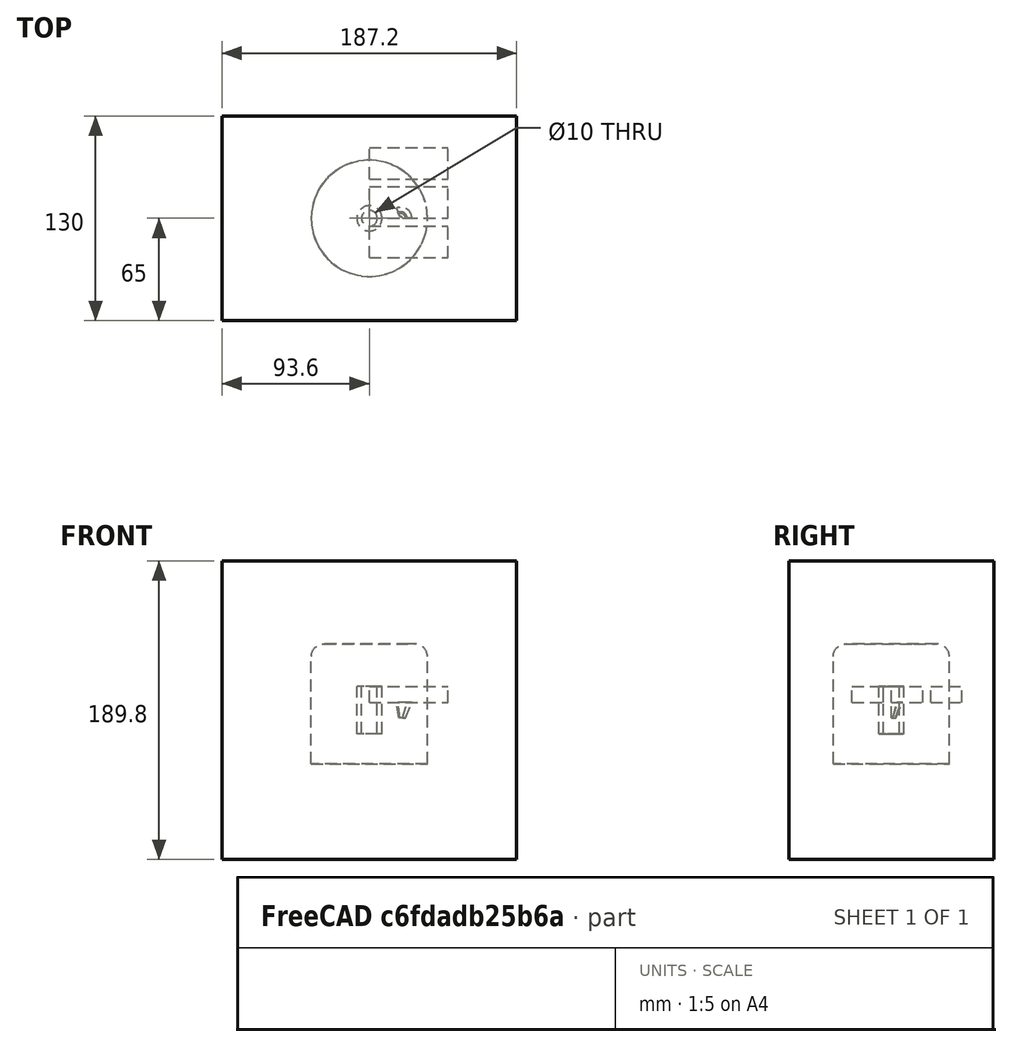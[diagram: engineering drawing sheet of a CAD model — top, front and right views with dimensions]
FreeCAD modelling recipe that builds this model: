
FCSTD DOCUMENT  (FreeCAD 1.0R39109 (Git))
Label: AssemblyTest
License: All rights reserved
LicenseURL: http://en.wikipedia.org/wiki/All_rights_reserved
objects: App::DocumentObjectGroupPython×1251, Part::FeaturePython×6, App::Part×5, Part::Box×3, Part::Fuse×2
note: 11 computed .brp shape members not serialized (recipe doc carries the construction recipe); baked Part::Feature solids carry a one-line shape summary decoded from their .brp

FEATURE [App::DocumentObjectGroupPython] HALFPI  # scripted group (container) (typed FeaturePython)
  name = HALFPI
  value = pi/2.
FEATURE [App::DocumentObjectGroupPython] PI  # scripted group (container) (typed FeaturePython)
  name = PI
  value = 1.*pi
FEATURE [App::DocumentObjectGroupPython] TWOPI  # scripted group (container) (typed FeaturePython)
  name = TWOPI
  value = 2.*pi
FEATURE [App::DocumentObjectGroupPython] Constants  # scripted group (container) (typed FeaturePython)
  Group = -> [HALFPI,PI,TWOPI]
FEATURE [App::DocumentObjectGroupPython] Variables  # scripted group (container) (typed FeaturePython)
FEATURE [App::DocumentObjectGroupPython] Quantities  # scripted group (container) (typed FeaturePython)
FEATURE [App::DocumentObjectGroupPython] Isotopes  # scripted group (container) (typed FeaturePython)
FEATURE [App::DocumentObjectGroupPython] Elements  # scripted group (container) (typed FeaturePython)
FEATURE [App::DocumentObjectGroupPython] Matrix  # scripted group (container) (typed FeaturePython)
FEATURE [App::DocumentObjectGroupPython] Surfaces  # scripted group (container) (typed FeaturePython)
FEATURE [App::DocumentObjectGroupPython] Opticals  # scripted group (container) (typed FeaturePython)
  Group = -> [Matrix,Surfaces]
FEATURE [App::DocumentObjectGroupPython] G4Isotopes  # scripted group (container) (typed FeaturePython)
FEATURE [App::DocumentObjectGroupPython] H_element  # scripted group (container) (typed FeaturePython)
  Z = 1
  atom_value = 1.008
  formula = H
  name = H_element
FEATURE [App::DocumentObjectGroupPython] He_element  # scripted group (container) (typed FeaturePython)
  Z = 2
  atom_value = 4.0026
  formula = He
  name = He_element
FEATURE [App::DocumentObjectGroupPython] Li_element  # scripted group (container) (typed FeaturePython)
  Z = 3
  atom_value = 6.94
  formula = Li
  name = Li_element
FEATURE [App::DocumentObjectGroupPython] Be_element  # scripted group (container) (typed FeaturePython)
  Z = 4
  atom_value = 9.01218
  formula = Be
  name = Be_element
FEATURE [App::DocumentObjectGroupPython] B_element  # scripted group (container) (typed FeaturePython)
  Z = 5
  atom_value = 10.81
  formula = B
  name = B_element
FEATURE [App::DocumentObjectGroupPython] C_element  # scripted group (container) (typed FeaturePython)
  Z = 6
  atom_value = 12.011
  formula = C
  name = C_element
FEATURE [App::DocumentObjectGroupPython] N_element  # scripted group (container) (typed FeaturePython)
  Z = 7
  atom_value = 14.007
  formula = N
  name = N_element
FEATURE [App::DocumentObjectGroupPython] O_element  # scripted group (container) (typed FeaturePython)
  Z = 8
  atom_value = 15.999
  formula = O
  name = O_element
FEATURE [App::DocumentObjectGroupPython] F_element  # scripted group (container) (typed FeaturePython)
  Z = 9
  atom_value = 18.9984
  formula = F
  name = F_element
FEATURE [App::DocumentObjectGroupPython] Ne_element  # scripted group (container) (typed FeaturePython)
  Z = 10
  atom_value = 20.1797
  formula = Ne
  name = Ne_element
FEATURE [App::DocumentObjectGroupPython] Na_element  # scripted group (container) (typed FeaturePython)
  Z = 11
  atom_value = 22.9898
  formula = Na
  name = Na_element
FEATURE [App::DocumentObjectGroupPython] Mg_element  # scripted group (container) (typed FeaturePython)
  Z = 12
  atom_value = 24.305
  formula = Mg
  name = Mg_element
FEATURE [App::DocumentObjectGroupPython] Al_element  # scripted group (container) (typed FeaturePython)
  Z = 13
  atom_value = 26.9815
  formula = Al
  name = Al_element
FEATURE [App::DocumentObjectGroupPython] Si_element  # scripted group (container) (typed FeaturePython)
  Z = 14
  atom_value = 28.085
  formula = Si
  name = Si_element
FEATURE [App::DocumentObjectGroupPython] P_element  # scripted group (container) (typed FeaturePython)
  Z = 15
  atom_value = 30.9738
  formula = P
  name = P_element
FEATURE [App::DocumentObjectGroupPython] S_element  # scripted group (container) (typed FeaturePython)
  Z = 16
  atom_value = 32.06
  formula = S
  name = S_element
FEATURE [App::DocumentObjectGroupPython] Cl_element  # scripted group (container) (typed FeaturePython)
  Z = 17
  atom_value = 35.45
  formula = Cl
  name = Cl_element
FEATURE [App::DocumentObjectGroupPython] Ar_element  # scripted group (container) (typed FeaturePython)
  Z = 18
  atom_value = 39.95
  formula = Ar
  name = Ar_element
FEATURE [App::DocumentObjectGroupPython] K_element  # scripted group (container) (typed FeaturePython)
  Z = 19
  atom_value = 39.0983
  formula = K
  name = K_element
FEATURE [App::DocumentObjectGroupPython] Ca_element  # scripted group (container) (typed FeaturePython)
  Z = 20
  atom_value = 40.078
  formula = Ca
  name = Ca_element
FEATURE [App::DocumentObjectGroupPython] Sc_element  # scripted group (container) (typed FeaturePython)
  Z = 21
  atom_value = 44.9559
  formula = Sc
  name = Sc_element
FEATURE [App::DocumentObjectGroupPython] Ti_element  # scripted group (container) (typed FeaturePython)
  Z = 22
  atom_value = 47.867
  formula = Ti
  name = Ti_element
FEATURE [App::DocumentObjectGroupPython] V_element  # scripted group (container) (typed FeaturePython)
  Z = 23
  atom_value = 50.9415
  formula = V
  name = V_element
FEATURE [App::DocumentObjectGroupPython] Cr_element  # scripted group (container) (typed FeaturePython)
  Z = 24
  atom_value = 51.9961
  formula = Cr
  name = Cr_element
FEATURE [App::DocumentObjectGroupPython] Mn_element  # scripted group (container) (typed FeaturePython)
  Z = 25
  atom_value = 54.938
  formula = Mn
  name = Mn_element
FEATURE [App::DocumentObjectGroupPython] Fe_element  # scripted group (container) (typed FeaturePython)
  Z = 26
  atom_value = 55.845
  formula = Fe
  name = Fe_element
FEATURE [App::DocumentObjectGroupPython] Co_element  # scripted group (container) (typed FeaturePython)
  Z = 27
  atom_value = 58.9332
  formula = Co
  name = Co_element
FEATURE [App::DocumentObjectGroupPython] Ni_element  # scripted group (container) (typed FeaturePython)
  Z = 28
  atom_value = 58.6934
  formula = Ni
  name = Ni_element
FEATURE [App::DocumentObjectGroupPython] Cu_element  # scripted group (container) (typed FeaturePython)
  Z = 29
  atom_value = 63.546
  formula = Cu
  name = Cu_element
FEATURE [App::DocumentObjectGroupPython] Zn_element  # scripted group (container) (typed FeaturePython)
  Z = 30
  atom_value = 65.38
  formula = Zn
  name = Zn_element
FEATURE [App::DocumentObjectGroupPython] Ga_element  # scripted group (container) (typed FeaturePython)
  Z = 31
  atom_value = 69.723
  formula = Ga
  name = Ga_element
FEATURE [App::DocumentObjectGroupPython] Ge_element  # scripted group (container) (typed FeaturePython)
  Z = 32
  atom_value = 72.63
  formula = Ge
  name = Ge_element
FEATURE [App::DocumentObjectGroupPython] As_element  # scripted group (container) (typed FeaturePython)
  Z = 33
  atom_value = 74.9216
  formula = As
  name = As_element
FEATURE [App::DocumentObjectGroupPython] Se_element  # scripted group (container) (typed FeaturePython)
  Z = 34
  atom_value = 78.971
  formula = Se
  name = Se_element
FEATURE [App::DocumentObjectGroupPython] Br_element  # scripted group (container) (typed FeaturePython)
  Z = 35
  atom_value = 79.904
  formula = Br
  name = Br_element
FEATURE [App::DocumentObjectGroupPython] Kr_element  # scripted group (container) (typed FeaturePython)
  Z = 36
  atom_value = 83.798
  formula = Kr
  name = Kr_element
FEATURE [App::DocumentObjectGroupPython] Rb_element  # scripted group (container) (typed FeaturePython)
  Z = 37
  atom_value = 85.4678
  formula = Rb
  name = Rb_element
FEATURE [App::DocumentObjectGroupPython] Sr_element  # scripted group (container) (typed FeaturePython)
  Z = 38
  atom_value = 87.62
  formula = Sr
  name = Sr_element
FEATURE [App::DocumentObjectGroupPython] Y_element  # scripted group (container) (typed FeaturePython)
  Z = 39
  atom_value = 88.9058
  formula = Y
  name = Y_element
FEATURE [App::DocumentObjectGroupPython] Zr_element  # scripted group (container) (typed FeaturePython)
  Z = 40
  atom_value = 91.224
  formula = Zr
  name = Zr_element
FEATURE [App::DocumentObjectGroupPython] Nb_element  # scripted group (container) (typed FeaturePython)
  Z = 41
  atom_value = 92.9064
  formula = Nb
  name = Nb_element
FEATURE [App::DocumentObjectGroupPython] Mo_element  # scripted group (container) (typed FeaturePython)
  Z = 42
  atom_value = 95.95
  formula = Mo
  name = Mo_element
FEATURE [App::DocumentObjectGroupPython] Tc_element  # scripted group (container) (typed FeaturePython)
  Z = 43
  atom_value = 97
  formula = Tc
  name = Tc_element
FEATURE [App::DocumentObjectGroupPython] Ru_element  # scripted group (container) (typed FeaturePython)
  Z = 44
  atom_value = 101.07
  formula = Ru
  name = Ru_element
FEATURE [App::DocumentObjectGroupPython] Rh_element  # scripted group (container) (typed FeaturePython)
  Z = 45
  atom_value = 102.905
  formula = Rh
  name = Rh_element
FEATURE [App::DocumentObjectGroupPython] Pd_element  # scripted group (container) (typed FeaturePython)
  Z = 46
  atom_value = 106.42
  formula = Pd
  name = Pd_element
FEATURE [App::DocumentObjectGroupPython] Ag_element  # scripted group (container) (typed FeaturePython)
  Z = 47
  atom_value = 107.868
  formula = Ag
  name = Ag_element
FEATURE [App::DocumentObjectGroupPython] Cd_element  # scripted group (container) (typed FeaturePython)
  Z = 48
  atom_value = 112.414
  formula = Cd
  name = Cd_element
FEATURE [App::DocumentObjectGroupPython] In_element  # scripted group (container) (typed FeaturePython)
  Z = 49
  atom_value = 114.818
  formula = In
  name = In_element
FEATURE [App::DocumentObjectGroupPython] Sn_element  # scripted group (container) (typed FeaturePython)
  Z = 50
  atom_value = 118.71
  formula = Sn
  name = Sn_element
FEATURE [App::DocumentObjectGroupPython] Sb_element  # scripted group (container) (typed FeaturePython)
  Z = 51
  atom_value = 121.76
  formula = Sb
  name = Sb_element
FEATURE [App::DocumentObjectGroupPython] Te_element  # scripted group (container) (typed FeaturePython)
  Z = 52
  atom_value = 127.6
  formula = Te
  name = Te_element
FEATURE [App::DocumentObjectGroupPython] I_element  # scripted group (container) (typed FeaturePython)
  Z = 53
  atom_value = 126.904
  formula = I
  name = I_element
FEATURE [App::DocumentObjectGroupPython] Xe_element  # scripted group (container) (typed FeaturePython)
  Z = 54
  atom_value = 131.293
  formula = Xe
  name = Xe_element
FEATURE [App::DocumentObjectGroupPython] Cs_element  # scripted group (container) (typed FeaturePython)
  Z = 55
  atom_value = 132.905
  formula = Cs
  name = Cs_element
FEATURE [App::DocumentObjectGroupPython] Ba_element  # scripted group (container) (typed FeaturePython)
  Z = 56
  atom_value = 137.327
  formula = Ba
  name = Ba_element
FEATURE [App::DocumentObjectGroupPython] La_element  # scripted group (container) (typed FeaturePython)
  Z = 57
  atom_value = 138.905
  formula = La
  name = La_element
FEATURE [App::DocumentObjectGroupPython] Ce_element  # scripted group (container) (typed FeaturePython)
  Z = 58
  atom_value = 140.116
  formula = Ce
  name = Ce_element
FEATURE [App::DocumentObjectGroupPython] Pr_element  # scripted group (container) (typed FeaturePython)
  Z = 59
  atom_value = 140.908
  formula = Pr
  name = Pr_element
FEATURE [App::DocumentObjectGroupPython] Nd_element  # scripted group (container) (typed FeaturePython)
  Z = 60
  atom_value = 144.242
  formula = Nd
  name = Nd_element
FEATURE [App::DocumentObjectGroupPython] Pm_element  # scripted group (container) (typed FeaturePython)
  Z = 61
  atom_value = 145
  formula = Pm
  name = Pm_element
FEATURE [App::DocumentObjectGroupPython] Sm_element  # scripted group (container) (typed FeaturePython)
  Z = 62
  atom_value = 150.36
  formula = Sm
  name = Sm_element
FEATURE [App::DocumentObjectGroupPython] Eu_element  # scripted group (container) (typed FeaturePython)
  Z = 63
  atom_value = 151.964
  formula = Eu
  name = Eu_element
FEATURE [App::DocumentObjectGroupPython] Gd_element  # scripted group (container) (typed FeaturePython)
  Z = 64
  atom_value = 157.25
  formula = Gd
  name = Gd_element
FEATURE [App::DocumentObjectGroupPython] Tb_element  # scripted group (container) (typed FeaturePython)
  Z = 65
  atom_value = 158.925
  formula = Tb
  name = Tb_element
FEATURE [App::DocumentObjectGroupPython] Dy_element  # scripted group (container) (typed FeaturePython)
  Z = 66
  atom_value = 162.5
  formula = Dy
  name = Dy_element
FEATURE [App::DocumentObjectGroupPython] Ho_element  # scripted group (container) (typed FeaturePython)
  Z = 67
  atom_value = 164.93
  formula = Ho
  name = Ho_element
FEATURE [App::DocumentObjectGroupPython] Er_element  # scripted group (container) (typed FeaturePython)
  Z = 68
  atom_value = 167.259
  formula = Er
  name = Er_element
FEATURE [App::DocumentObjectGroupPython] Tm_element  # scripted group (container) (typed FeaturePython)
  Z = 69
  atom_value = 168.934
  formula = Tm
  name = Tm_element
FEATURE [App::DocumentObjectGroupPython] Yb_element  # scripted group (container) (typed FeaturePython)
  Z = 70
  atom_value = 173.045
  formula = Yb
  name = Yb_element
FEATURE [App::DocumentObjectGroupPython] Lu_element  # scripted group (container) (typed FeaturePython)
  Z = 71
  atom_value = 174.967
  formula = Lu
  name = Lu_element
FEATURE [App::DocumentObjectGroupPython] Hf_element  # scripted group (container) (typed FeaturePython)
  Z = 72
  atom_value = 178.49
  formula = Hf
  name = Hf_element
FEATURE [App::DocumentObjectGroupPython] Ta_element  # scripted group (container) (typed FeaturePython)
  Z = 73
  atom_value = 180.948
  formula = Ta
  name = Ta_element
FEATURE [App::DocumentObjectGroupPython] W_element  # scripted group (container) (typed FeaturePython)
  Z = 74
  atom_value = 183.84
  formula = W
  name = W_element
FEATURE [App::DocumentObjectGroupPython] Re_element  # scripted group (container) (typed FeaturePython)
  Z = 75
  atom_value = 186.207
  formula = Re
  name = Re_element
FEATURE [App::DocumentObjectGroupPython] Os_element  # scripted group (container) (typed FeaturePython)
  Z = 76
  atom_value = 190.23
  formula = Os
  name = Os_element
FEATURE [App::DocumentObjectGroupPython] Ir_element  # scripted group (container) (typed FeaturePython)
  Z = 77
  atom_value = 192.217
  formula = Ir
  name = Ir_element
FEATURE [App::DocumentObjectGroupPython] Pt_element  # scripted group (container) (typed FeaturePython)
  Z = 78
  atom_value = 195.084
  formula = Pt
  name = Pt_element
FEATURE [App::DocumentObjectGroupPython] Au_element  # scripted group (container) (typed FeaturePython)
  Z = 79
  atom_value = 196.967
  formula = Au
  name = Au_element
FEATURE [App::DocumentObjectGroupPython] Hg_element  # scripted group (container) (typed FeaturePython)
  Z = 80
  atom_value = 200.592
  formula = Hg
  name = Hg_element
FEATURE [App::DocumentObjectGroupPython] Tl_element  # scripted group (container) (typed FeaturePython)
  Z = 81
  atom_value = 204.38
  formula = Tl
  name = Tl_element
FEATURE [App::DocumentObjectGroupPython] Pb_element  # scripted group (container) (typed FeaturePython)
  Z = 82
  atom_value = 207.2
  formula = Pb
  name = Pb_element
FEATURE [App::DocumentObjectGroupPython] Bi_element  # scripted group (container) (typed FeaturePython)
  Z = 83
  atom_value = 208.98
  formula = Bi
  name = Bi_element
FEATURE [App::DocumentObjectGroupPython] Po_element  # scripted group (container) (typed FeaturePython)
  Z = 84
  atom_value = 209
  formula = Po
  name = Po_element
FEATURE [App::DocumentObjectGroupPython] At_element  # scripted group (container) (typed FeaturePython)
  Z = 85
  atom_value = 210
  formula = At
  name = At_element
FEATURE [App::DocumentObjectGroupPython] Rn_element  # scripted group (container) (typed FeaturePython)
  Z = 86
  atom_value = 222
  formula = Rn
  name = Rn_element
FEATURE [App::DocumentObjectGroupPython] Fr_element  # scripted group (container) (typed FeaturePython)
  Z = 87
  atom_value = 223
  formula = Fr
  name = Fr_element
FEATURE [App::DocumentObjectGroupPython] Ra_element  # scripted group (container) (typed FeaturePython)
  Z = 88
  atom_value = 226
  formula = Ra
  name = Ra_element
FEATURE [App::DocumentObjectGroupPython] Ac_element  # scripted group (container) (typed FeaturePython)
  Z = 89
  atom_value = 227
  formula = Ac
  name = Ac_element
FEATURE [App::DocumentObjectGroupPython] Th_element  # scripted group (container) (typed FeaturePython)
  Z = 90
  atom_value = 232.038
  formula = Th
  name = Th_element
FEATURE [App::DocumentObjectGroupPython] Pa_element  # scripted group (container) (typed FeaturePython)
  Z = 91
  atom_value = 231.036
  formula = Pa
  name = Pa_element
FEATURE [App::DocumentObjectGroupPython] U_element  # scripted group (container) (typed FeaturePython)
  Z = 92
  atom_value = 238.029
  formula = U
  name = U_element
FEATURE [App::DocumentObjectGroupPython] Np_element  # scripted group (container) (typed FeaturePython)
  Z = 93
  atom_value = 237
  formula = Np
  name = Np_element
FEATURE [App::DocumentObjectGroupPython] Pu_element  # scripted group (container) (typed FeaturePython)
  Z = 94
  atom_value = 244
  formula = Pu
  name = Pu_element
FEATURE [App::DocumentObjectGroupPython] Am_element  # scripted group (container) (typed FeaturePython)
  Z = 95
  atom_value = 243
  formula = Am
  name = Am_element
FEATURE [App::DocumentObjectGroupPython] Cm_element  # scripted group (container) (typed FeaturePython)
  Z = 96
  atom_value = 247
  formula = Cm
  name = Cm_element
FEATURE [App::DocumentObjectGroupPython] Bk_element  # scripted group (container) (typed FeaturePython)
  Z = 97
  atom_value = 247
  formula = Bk
  name = Bk_element
FEATURE [App::DocumentObjectGroupPython] Cf_element  # scripted group (container) (typed FeaturePython)
  Z = 98
  atom_value = 251
  formula = Cf
  name = Cf_element
FEATURE [App::DocumentObjectGroupPython] G4Elements  # scripted group (container) (typed FeaturePython)
  Group = -> [H_element,He_element,Li_element,Be_element,B_element,C_element,N_element,O_element,F_element,Ne_element,Na_element,Mg_element,Al_element,Si_element,P_element,S_element,Cl_element,Ar_element,K_element,Ca_element,Sc_element,Ti_element,V_element,Cr_element,Mn_element,Fe_element,Co_element,Ni_element,Cu_element,Zn_element,Ga_element,Ge_element,As_element,Se_element,Br_element,Kr_element,Rb_element,+61 more]
FEATURE [App::DocumentObjectGroupPython] H_element001  label="H_element : 0.101"  # scripted group (container) (typed FeaturePython)
  n = 0.101327
FEATURE [App::DocumentObjectGroupPython] C_element001  label="C_element : 0.775"  # scripted group (container) (typed FeaturePython)
  n = 0.7755
FEATURE [App::DocumentObjectGroupPython] N_element001  label="N_element : 0.035"  # scripted group (container) (typed FeaturePython)
  n = 0.035057
FEATURE [App::DocumentObjectGroupPython] O_element001  label="O_element : 0.052"  # scripted group (container) (typed FeaturePython)
  n = 0.0523159
FEATURE [App::DocumentObjectGroupPython] F_element001  label="F_element : 0.017"  # scripted group (container) (typed FeaturePython)
  n = 0.017422
FEATURE [App::DocumentObjectGroupPython] Ca_element001  label="Ca_element : 0.018"  # scripted group (container) (typed FeaturePython)
  n = 0.018378
FEATURE [App::DocumentObjectGroupPython] G4_A_150_TISSUE  label="G4_A-150_TISSUE"  # scripted group (container) (typed FeaturePython)
  Dunit = g/cm3
  Dvalue = 1.127
  Group = -> [H_element001,C_element001,N_element001,O_element001,F_element001,Ca_element001]
  conduct = 2
  density = 1
  expand = 3
  formula = G4_A-150_TISSUE
  name = G4_A-150_TISSUE
  specific = 4
FEATURE [App::DocumentObjectGroupPython] C_element002  label="C_element : 3"  # scripted group (container) (typed FeaturePython)
  n = 3
  ref = C_element
FEATURE [App::DocumentObjectGroupPython] H_element002  label="H_element : 6"  # scripted group (container) (typed FeaturePython)
  n = 6
  ref = H_element
FEATURE [App::DocumentObjectGroupPython] O_element002  label="O_element : 1"  # scripted group (container) (typed FeaturePython)
  n = 1
  ref = O_element
FEATURE [App::DocumentObjectGroupPython] G4_ACETONE  # scripted group (container) (typed FeaturePython)
  Dunit = g/cm3
  Dvalue = 0.7899
  Group = -> [C_element002,H_element002,O_element002]
  conduct = 2
  density = 1
  expand = 3
  formula = G4_ACETONE
  name = G4_ACETONE
  specific = 4
FEATURE [App::DocumentObjectGroupPython] C_element003  label="C_element : 2"  # scripted group (container) (typed FeaturePython)
  n = 2
  ref = C_element
FEATURE [App::DocumentObjectGroupPython] H_element003  label="H_element : 2"  # scripted group (container) (typed FeaturePython)
  n = 2
  ref = H_element
FEATURE [App::DocumentObjectGroupPython] G4_ACETYLENE  # scripted group (container) (typed FeaturePython)
  Dunit = g/cm3
  Dvalue = 0.0010967
  Group = -> [C_element003,H_element003]
  conduct = 2
  density = 1
  expand = 3
  formula = G4_ACETYLENE
  name = G4_ACETYLENE
  specific = 4
FEATURE [App::DocumentObjectGroupPython] C_element004  label="C_element : 5"  # scripted group (container) (typed FeaturePython)
  n = 5
  ref = C_element
FEATURE [App::DocumentObjectGroupPython] H_element004  label="H_element : 5"  # scripted group (container) (typed FeaturePython)
  n = 5
  ref = H_element
FEATURE [App::DocumentObjectGroupPython] N_element002  label="N_element : 5"  # scripted group (container) (typed FeaturePython)
  n = 5
  ref = N_element
FEATURE [App::DocumentObjectGroupPython] G4_ADENINE  # scripted group (container) (typed FeaturePython)
  Dunit = g/cm3
  Dvalue = 1.6
  Group = -> [C_element004,H_element004,N_element002]
  conduct = 2
  density = 1
  expand = 3
  formula = G4_ADENINE
  name = G4_ADENINE
  specific = 4
FEATURE [App::DocumentObjectGroupPython] H_element005  label="H_element : 0.114"  # scripted group (container) (typed FeaturePython)
  n = 0.114
FEATURE [App::DocumentObjectGroupPython] C_element005  label="C_element : 0.598"  # scripted group (container) (typed FeaturePython)
  n = 0.598
FEATURE [App::DocumentObjectGroupPython] N_element003  label="N_element : 0.007"  # scripted group (container) (typed FeaturePython)
  n = 0.007
FEATURE [App::DocumentObjectGroupPython] O_element003  label="O_element : 0.278"  # scripted group (container) (typed FeaturePython)
  n = 0.278
FEATURE [App::DocumentObjectGroupPython] Na_element001  label="Na_element : 0.001"  # scripted group (container) (typed FeaturePython)
  n = 0.001
FEATURE [App::DocumentObjectGroupPython] S_element001  label="S_element : 0.001"  # scripted group (container) (typed FeaturePython)
  n = 0.001
FEATURE [App::DocumentObjectGroupPython] Cl_element001  label="Cl_element : 0.001"  # scripted group (container) (typed FeaturePython)
  n = 0.001
FEATURE [App::DocumentObjectGroupPython] G4_ADIPOSE_TISSUE_ICRP  # scripted group (container) (typed FeaturePython)
  Dunit = g/cm3
  Dvalue = 0.95
  Group = -> [H_element005,C_element005,N_element003,O_element003,Na_element001,S_element001,Cl_element001]
  conduct = 2
  density = 1
  expand = 3
  formula = G4_ADIPOSE_TISSUE_ICRP
  name = G4_ADIPOSE_TISSUE_ICRP
  specific = 4
FEATURE [App::DocumentObjectGroupPython] C_element006  label="C_element : 0.000"  # scripted group (container) (typed FeaturePython)
  n = 0.000124
FEATURE [App::DocumentObjectGroupPython] N_element004  label="N_element : 0.755"  # scripted group (container) (typed FeaturePython)
  n = 0.755268
FEATURE [App::DocumentObjectGroupPython] O_element004  label="O_element : 0.232"  # scripted group (container) (typed FeaturePython)
  n = 0.231781
FEATURE [App::DocumentObjectGroupPython] Ar_element001  label="Ar_element : 0.013"  # scripted group (container) (typed FeaturePython)
  n = 0.012827
FEATURE [App::DocumentObjectGroupPython] G4_AIR  # scripted group (container) (typed FeaturePython)
  Dunit = g/cm3
  Dvalue = 0.00120479
  Group = -> [C_element006,N_element004,O_element004,Ar_element001]
  conduct = 2
  density = 1
  expand = 3
  formula = G4_AIR
  name = G4_AIR
  specific = 4
FEATURE [App::DocumentObjectGroupPython] C_element007  label="C_element : 006"  # scripted group (container) (typed FeaturePython)
  n = 3
  ref = C_element
FEATURE [App::DocumentObjectGroupPython] H_element006  label="H_element : 7"  # scripted group (container) (typed FeaturePython)
  n = 7
  ref = H_element
FEATURE [App::DocumentObjectGroupPython] N_element005  label="N_element : 1"  # scripted group (container) (typed FeaturePython)
  n = 1
  ref = N_element
FEATURE [App::DocumentObjectGroupPython] O_element005  label="O_element : 2"  # scripted group (container) (typed FeaturePython)
  n = 2
  ref = O_element
FEATURE [App::DocumentObjectGroupPython] G4_ALANINE  # scripted group (container) (typed FeaturePython)
  Dunit = g/cm3
  Dvalue = 1.42
  Group = -> [C_element007,H_element006,N_element005,O_element005]
  conduct = 2
  density = 1
  expand = 3
  formula = G4_ALANINE
  name = G4_ALANINE
  specific = 4
FEATURE [App::DocumentObjectGroupPython] Al_element001  label="Al_element : 2"  # scripted group (container) (typed FeaturePython)
  n = 2
  ref = Al_element
FEATURE [App::DocumentObjectGroupPython] O_element006  label="O_element : 3"  # scripted group (container) (typed FeaturePython)
  n = 3
  ref = O_element
FEATURE [App::DocumentObjectGroupPython] G4_ALUMINUM_OXIDE  # scripted group (container) (typed FeaturePython)
  Dunit = g/cm3
  Dvalue = 3.97
  Group = -> [Al_element001,O_element006]
  conduct = 2
  density = 1
  expand = 3
  formula = G4_ALUMINUM_OXIDE
  name = G4_ALUMINUM_OXIDE
  specific = 4
FEATURE [App::DocumentObjectGroupPython] H_element007  label="H_element : 0.106"  # scripted group (container) (typed FeaturePython)
  n = 0.10593
FEATURE [App::DocumentObjectGroupPython] C_element008  label="C_element : 0.789"  # scripted group (container) (typed FeaturePython)
  n = 0.788974
FEATURE [App::DocumentObjectGroupPython] O_element007  label="O_element : 0.105"  # scripted group (container) (typed FeaturePython)
  n = 0.105096
FEATURE [App::DocumentObjectGroupPython] G4_AMBER  # scripted group (container) (typed FeaturePython)
  Dunit = g/cm3
  Dvalue = 1.1
  Group = -> [H_element007,C_element008,O_element007]
  conduct = 2
  density = 1
  expand = 3
  formula = G4_AMBER
  name = G4_AMBER
  specific = 4
FEATURE [App::DocumentObjectGroupPython] N_element006  label="N_element : 006"  # scripted group (container) (typed FeaturePython)
  n = 1
  ref = N_element
FEATURE [App::DocumentObjectGroupPython] H_element008  label="H_element : 3"  # scripted group (container) (typed FeaturePython)
  n = 3
  ref = H_element
FEATURE [App::DocumentObjectGroupPython] G4_AMMONIA  # scripted group (container) (typed FeaturePython)
  Dunit = g/cm3
  Dvalue = 0.000826019
  Group = -> [N_element006,H_element008]
  conduct = 2
  density = 1
  expand = 3
  formula = G4_AMMONIA
  name = G4_AMMONIA
  specific = 4
FEATURE [App::DocumentObjectGroupPython] C_element009  label="C_element : 6"  # scripted group (container) (typed FeaturePython)
  n = 6
  ref = C_element
FEATURE [App::DocumentObjectGroupPython] H_element009  label="H_element : 008"  # scripted group (container) (typed FeaturePython)
  n = 7
  ref = H_element
FEATURE [App::DocumentObjectGroupPython] N_element007  label="N_element : 007"  # scripted group (container) (typed FeaturePython)
  n = 1
  ref = N_element
FEATURE [App::DocumentObjectGroupPython] G4_ANILINE  # scripted group (container) (typed FeaturePython)
  Dunit = g/cm3
  Dvalue = 1.0235
  Group = -> [C_element009,H_element009,N_element007]
  conduct = 2
  density = 1
  expand = 3
  formula = G4_ANILINE
  name = G4_ANILINE
  specific = 4
FEATURE [App::DocumentObjectGroupPython] C_element010  label="C_element : 14"  # scripted group (container) (typed FeaturePython)
  n = 14
  ref = C_element
FEATURE [App::DocumentObjectGroupPython] H_element010  label="H_element : 10"  # scripted group (container) (typed FeaturePython)
  n = 10
  ref = H_element
FEATURE [App::DocumentObjectGroupPython] G4_ANTHRACENE  # scripted group (container) (typed FeaturePython)
  Dunit = g/cm3
  Dvalue = 1.283
  Group = -> [C_element010,H_element010]
  conduct = 2
  density = 1
  expand = 3
  formula = G4_ANTHRACENE
  name = G4_ANTHRACENE
  specific = 4
FEATURE [App::DocumentObjectGroupPython] H_element011  label="H_element : 0.065"  # scripted group (container) (typed FeaturePython)
  n = 0.0654709
FEATURE [App::DocumentObjectGroupPython] C_element011  label="C_element : 0.537"  # scripted group (container) (typed FeaturePython)
  n = 0.536944
FEATURE [App::DocumentObjectGroupPython] N_element008  label="N_element : 0.021"  # scripted group (container) (typed FeaturePython)
  n = 0.0215
FEATURE [App::DocumentObjectGroupPython] O_element008  label="O_element : 0.032"  # scripted group (container) (typed FeaturePython)
  n = 0.032085
FEATURE [App::DocumentObjectGroupPython] F_element002  label="F_element : 0.167"  # scripted group (container) (typed FeaturePython)
  n = 0.167411
FEATURE [App::DocumentObjectGroupPython] Ca_element002  label="Ca_element : 0.177"  # scripted group (container) (typed FeaturePython)
  n = 0.176589
FEATURE [App::DocumentObjectGroupPython] G4_B_100_BONE  label="G4_B-100_BONE"  # scripted group (container) (typed FeaturePython)
  Dunit = g/cm3
  Dvalue = 1.45
  Group = -> [H_element011,C_element011,N_element008,O_element008,F_element002,Ca_element002]
  conduct = 2
  density = 1
  expand = 3
  formula = G4_B-100_BONE
  name = G4_B-100_BONE
  specific = 4
FEATURE [App::DocumentObjectGroupPython] H_element012  label="H_element : 0.057"  # scripted group (container) (typed FeaturePython)
  n = 0.057441
FEATURE [App::DocumentObjectGroupPython] C_element012  label="C_element : 0.790"  # scripted group (container) (typed FeaturePython)
  n = 0.774591
FEATURE [App::DocumentObjectGroupPython] O_element009  label="O_element : 0.168"  # scripted group (container) (typed FeaturePython)
  n = 0.167968
FEATURE [App::DocumentObjectGroupPython] G4_BAKELITE  # scripted group (container) (typed FeaturePython)
  Dunit = g/cm3
  Dvalue = 1.25
  Group = -> [H_element012,C_element012,O_element009]
  conduct = 2
  density = 1
  expand = 3
  formula = G4_BAKELITE
  name = G4_BAKELITE
  specific = 4
FEATURE [App::DocumentObjectGroupPython] Ba_element001  label="Ba_element : 1"  # scripted group (container) (typed FeaturePython)
  n = 1
  ref = Ba_element
FEATURE [App::DocumentObjectGroupPython] F_element003  label="F_element : 2"  # scripted group (container) (typed FeaturePython)
  n = 2
  ref = F_element
FEATURE [App::DocumentObjectGroupPython] G4_BARIUM_FLUORIDE  # scripted group (container) (typed FeaturePython)
  Dunit = g/cm3
  Dvalue = 4.89
  Group = -> [Ba_element001,F_element003]
  conduct = 2
  density = 1
  expand = 3
  formula = G4_BARIUM_FLUORIDE
  name = G4_BARIUM_FLUORIDE
  specific = 4
FEATURE [App::DocumentObjectGroupPython] Ba_element002  label="Ba_element : 002"  # scripted group (container) (typed FeaturePython)
  n = 1
  ref = Ba_element
FEATURE [App::DocumentObjectGroupPython] S_element002  label="S_element : 1"  # scripted group (container) (typed FeaturePython)
  n = 1
  ref = S_element
FEATURE [App::DocumentObjectGroupPython] O_element010  label="O_element : 4"  # scripted group (container) (typed FeaturePython)
  n = 4
  ref = O_element
FEATURE [App::DocumentObjectGroupPython] G4_BARIUM_SULFATE  # scripted group (container) (typed FeaturePython)
  Dunit = g/cm3
  Dvalue = 4.5
  Group = -> [Ba_element002,S_element002,O_element010]
  conduct = 2
  density = 1
  expand = 3
  formula = G4_BARIUM_SULFATE
  name = G4_BARIUM_SULFATE
  specific = 4
FEATURE [App::DocumentObjectGroupPython] C_element013  label="C_element : 007"  # scripted group (container) (typed FeaturePython)
  n = 6
  ref = C_element
FEATURE [App::DocumentObjectGroupPython] H_element013  label="H_element : 009"  # scripted group (container) (typed FeaturePython)
  n = 6
  ref = H_element
FEATURE [App::DocumentObjectGroupPython] G4_BENZENE  # scripted group (container) (typed FeaturePython)
  Dunit = g/cm3
  Dvalue = 0.87865
  Group = -> [C_element013,H_element013]
  conduct = 2
  density = 1
  expand = 3
  formula = G4_BENZENE
  name = G4_BENZENE
  specific = 4
FEATURE [App::DocumentObjectGroupPython] Be_element001  label="Be_element : 1"  # scripted group (container) (typed FeaturePython)
  n = 1
  ref = Be_element
FEATURE [App::DocumentObjectGroupPython] O_element011  label="O_element : 005"  # scripted group (container) (typed FeaturePython)
  n = 1
  ref = O_element
FEATURE [App::DocumentObjectGroupPython] G4_BERYLLIUM_OXIDE  # scripted group (container) (typed FeaturePython)
  Dunit = g/cm3
  Dvalue = 3.01
  Group = -> [Be_element001,O_element011]
  conduct = 2
  density = 1
  expand = 3
  formula = G4_BERYLLIUM_OXIDE
  name = G4_BERYLLIUM_OXIDE
  specific = 4
FEATURE [App::DocumentObjectGroupPython] Bi_element001  label="Bi_element : 4"  # scripted group (container) (typed FeaturePython)
  n = 4
  ref = Bi_element
FEATURE [App::DocumentObjectGroupPython] Ge_element001  label="Ge_element : 3"  # scripted group (container) (typed FeaturePython)
  n = 3
  ref = Ge_element
FEATURE [App::DocumentObjectGroupPython] O_element012  label="O_element : 12"  # scripted group (container) (typed FeaturePython)
  n = 12
  ref = O_element
FEATURE [App::DocumentObjectGroupPython] G4_BGO  # scripted group (container) (typed FeaturePython)
  Dunit = g/cm3
  Dvalue = 7.13
  Group = -> [Bi_element001,Ge_element001,O_element012]
  conduct = 2
  density = 1
  expand = 3
  formula = G4_BGO
  name = G4_BGO
  specific = 4
FEATURE [App::DocumentObjectGroupPython] H_element014  label="H_element : 0.102"  # scripted group (container) (typed FeaturePython)
  n = 0.102
FEATURE [App::DocumentObjectGroupPython] C_element014  label="C_element : 0.110"  # scripted group (container) (typed FeaturePython)
  n = 0.11
FEATURE [App::DocumentObjectGroupPython] N_element009  label="N_element : 0.033"  # scripted group (container) (typed FeaturePython)
  n = 0.033
FEATURE [App::DocumentObjectGroupPython] O_element013  label="O_element : 0.745"  # scripted group (container) (typed FeaturePython)
  n = 0.745
FEATURE [App::DocumentObjectGroupPython] Na_element002  label="Na_element : 0.002"  # scripted group (container) (typed FeaturePython)
  n = 0.001
FEATURE [App::DocumentObjectGroupPython] P_element001  label="P_element : 0.001"  # scripted group (container) (typed FeaturePython)
  n = 0.001
FEATURE [App::DocumentObjectGroupPython] S_element003  label="S_element : 0.002"  # scripted group (container) (typed FeaturePython)
  n = 0.002
FEATURE [App::DocumentObjectGroupPython] Cl_element002  label="Cl_element : 0.003"  # scripted group (container) (typed FeaturePython)
  n = 0.003
FEATURE [App::DocumentObjectGroupPython] K_element001  label="K_element : 0.002"  # scripted group (container) (typed FeaturePython)
  n = 0.002
FEATURE [App::DocumentObjectGroupPython] Fe_element001  label="Fe_element : 0.001"  # scripted group (container) (typed FeaturePython)
  n = 0.001
FEATURE [App::DocumentObjectGroupPython] G4_BLOOD_ICRP  # scripted group (container) (typed FeaturePython)
  Dunit = g/cm3
  Dvalue = 1.06
  Group = -> [H_element014,C_element014,N_element009,O_element013,Na_element002,P_element001,S_element003,Cl_element002,K_element001,Fe_element001]
  conduct = 2
  density = 1
  expand = 3
  formula = G4_BLOOD_ICRP
  name = G4_BLOOD_ICRP
  specific = 4
FEATURE [App::DocumentObjectGroupPython] H_element015  label="H_element : 0.064"  # scripted group (container) (typed FeaturePython)
  n = 0.064
FEATURE [App::DocumentObjectGroupPython] C_element015  label="C_element : 0.278"  # scripted group (container) (typed FeaturePython)
  n = 0.278
FEATURE [App::DocumentObjectGroupPython] N_element010  label="N_element : 0.027"  # scripted group (container) (typed FeaturePython)
  n = 0.027
FEATURE [App::DocumentObjectGroupPython] O_element014  label="O_element : 0.410"  # scripted group (container) (typed FeaturePython)
  n = 0.41
FEATURE [App::DocumentObjectGroupPython] Mg_element001  label="Mg_element : 0.002"  # scripted group (container) (typed FeaturePython)
  n = 0.002
FEATURE [App::DocumentObjectGroupPython] P_element002  label="P_element : 0.070"  # scripted group (container) (typed FeaturePython)
  n = 0.07
FEATURE [App::DocumentObjectGroupPython] S_element004  label="S_element : 0.003"  # scripted group (container) (typed FeaturePython)
  n = 0.002
FEATURE [App::DocumentObjectGroupPython] Ca_element003  label="Ca_element : 0.147"  # scripted group (container) (typed FeaturePython)
  n = 0.147
FEATURE [App::DocumentObjectGroupPython] G4_BONE_COMPACT_ICRU  # scripted group (container) (typed FeaturePython)
  Dunit = g/cm3
  Dvalue = 1.85
  Group = -> [H_element015,C_element015,N_element010,O_element014,Mg_element001,P_element002,S_element004,Ca_element003]
  conduct = 2
  density = 1
  expand = 3
  formula = G4_BONE_COMPACT_ICRU
  name = G4_BONE_COMPACT_ICRU
  specific = 4
FEATURE [App::DocumentObjectGroupPython] H_element016  label="H_element : 0.034"  # scripted group (container) (typed FeaturePython)
  n = 0.034
FEATURE [App::DocumentObjectGroupPython] C_element016  label="C_element : 0.155"  # scripted group (container) (typed FeaturePython)
  n = 0.155
FEATURE [App::DocumentObjectGroupPython] N_element011  label="N_element : 0.042"  # scripted group (container) (typed FeaturePython)
  n = 0.042
FEATURE [App::DocumentObjectGroupPython] O_element015  label="O_element : 0.435"  # scripted group (container) (typed FeaturePython)
  n = 0.435
FEATURE [App::DocumentObjectGroupPython] Na_element003  label="Na_element : 0.003"  # scripted group (container) (typed FeaturePython)
  n = 0.001
FEATURE [App::DocumentObjectGroupPython] Mg_element002  label="Mg_element : 0.003"  # scripted group (container) (typed FeaturePython)
  n = 0.002
FEATURE [App::DocumentObjectGroupPython] P_element003  label="P_element : 0.103"  # scripted group (container) (typed FeaturePython)
  n = 0.103
FEATURE [App::DocumentObjectGroupPython] S_element005  label="S_element : 0.004"  # scripted group (container) (typed FeaturePython)
  n = 0.003
FEATURE [App::DocumentObjectGroupPython] Ca_element004  label="Ca_element : 0.225"  # scripted group (container) (typed FeaturePython)
  n = 0.225
FEATURE [App::DocumentObjectGroupPython] G4_BONE_CORTICAL_ICRP  # scripted group (container) (typed FeaturePython)
  Dunit = g/cm3
  Dvalue = 1.92
  Group = -> [H_element016,C_element016,N_element011,O_element015,Na_element003,Mg_element002,P_element003,S_element005,Ca_element004]
  conduct = 2
  density = 1
  expand = 3
  formula = G4_BONE_CORTICAL_ICRP
  name = G4_BONE_CORTICAL_ICRP
  specific = 4
FEATURE [App::DocumentObjectGroupPython] B_element001  label="B_element : 4"  # scripted group (container) (typed FeaturePython)
  n = 4
  ref = B_element
FEATURE [App::DocumentObjectGroupPython] C_element017  label="C_element : 1"  # scripted group (container) (typed FeaturePython)
  n = 1
  ref = C_element
FEATURE [App::DocumentObjectGroupPython] G4_BORON_CARBIDE  # scripted group (container) (typed FeaturePython)
  Dunit = g/cm3
  Dvalue = 2.52
  Group = -> [B_element001,C_element017]
  conduct = 2
  density = 1
  expand = 3
  formula = G4_BORON_CARBIDE
  name = G4_BORON_CARBIDE
  specific = 4
FEATURE [App::DocumentObjectGroupPython] B_element002  label="B_element : 2"  # scripted group (container) (typed FeaturePython)
  n = 2
  ref = B_element
FEATURE [App::DocumentObjectGroupPython] O_element016  label="O_element : 006"  # scripted group (container) (typed FeaturePython)
  n = 3
  ref = O_element
FEATURE [App::DocumentObjectGroupPython] G4_BORON_OXIDE  # scripted group (container) (typed FeaturePython)
  Dunit = g/cm3
  Dvalue = 1.812
  Group = -> [B_element002,O_element016]
  conduct = 2
  density = 1
  expand = 3
  formula = G4_BORON_OXIDE
  name = G4_BORON_OXIDE
  specific = 4
FEATURE [App::DocumentObjectGroupPython] H_element017  label="H_element : 0.107"  # scripted group (container) (typed FeaturePython)
  n = 0.107
FEATURE [App::DocumentObjectGroupPython] C_element018  label="C_element : 0.145"  # scripted group (container) (typed FeaturePython)
  n = 0.145
FEATURE [App::DocumentObjectGroupPython] N_element012  label="N_element : 0.022"  # scripted group (container) (typed FeaturePython)
  n = 0.022
FEATURE [App::DocumentObjectGroupPython] O_element017  label="O_element : 0.712"  # scripted group (container) (typed FeaturePython)
  n = 0.712
FEATURE [App::DocumentObjectGroupPython] Na_element004  label="Na_element : 0.004"  # scripted group (container) (typed FeaturePython)
  n = 0.002
FEATURE [App::DocumentObjectGroupPython] P_element004  label="P_element : 0.004"  # scripted group (container) (typed FeaturePython)
  n = 0.004
FEATURE [App::DocumentObjectGroupPython] S_element006  label="S_element : 0.005"  # scripted group (container) (typed FeaturePython)
  n = 0.002
FEATURE [App::DocumentObjectGroupPython] Cl_element003  label="Cl_element : 0.004"  # scripted group (container) (typed FeaturePython)
  n = 0.003
FEATURE [App::DocumentObjectGroupPython] K_element002  label="K_element : 0.003"  # scripted group (container) (typed FeaturePython)
  n = 0.003
FEATURE [App::DocumentObjectGroupPython] G4_BRAIN_ICRP  # scripted group (container) (typed FeaturePython)
  Dunit = g/cm3
  Dvalue = 1.04
  Group = -> [H_element017,C_element018,N_element012,O_element017,Na_element004,P_element004,S_element006,Cl_element003,K_element002]
  conduct = 2
  density = 1
  expand = 3
  formula = G4_BRAIN_ICRP
  name = G4_BRAIN_ICRP
  specific = 4
FEATURE [App::DocumentObjectGroupPython] C_element019  label="C_element : 4"  # scripted group (container) (typed FeaturePython)
  n = 4
  ref = C_element
FEATURE [App::DocumentObjectGroupPython] H_element018  label="H_element : 010"  # scripted group (container) (typed FeaturePython)
  n = 10
  ref = H_element
FEATURE [App::DocumentObjectGroupPython] G4_BUTANE  # scripted group (container) (typed FeaturePython)
  Dunit = g/cm3
  Dvalue = 0.00249343
  Group = -> [C_element019,H_element018]
  conduct = 2
  density = 1
  expand = 3
  formula = G4_BUTANE
  name = G4_BUTANE
  specific = 4
FEATURE [App::DocumentObjectGroupPython] C_element020  label="C_element : 008"  # scripted group (container) (typed FeaturePython)
  n = 4
  ref = C_element
FEATURE [App::DocumentObjectGroupPython] H_element019  label="H_element : 011"  # scripted group (container) (typed FeaturePython)
  n = 10
  ref = H_element
FEATURE [App::DocumentObjectGroupPython] O_element018  label="O_element : 007"  # scripted group (container) (typed FeaturePython)
  n = 1
  ref = O_element
FEATURE [App::DocumentObjectGroupPython] G4_N_BUTYL_ALCOHOL  label="G4_N-BUTYL_ALCOHOL"  # scripted group (container) (typed FeaturePython)
  Dunit = g/cm3
  Dvalue = 0.8098
  Group = -> [C_element020,H_element019,O_element018]
  conduct = 2
  density = 1
  expand = 3
  formula = G4_N-BUTYL_ALCOHOL
  name = G4_N-BUTYL_ALCOHOL
  specific = 4
FEATURE [App::DocumentObjectGroupPython] H_element020  label="H_element : 0.025"  # scripted group (container) (typed FeaturePython)
  n = 0.02468
FEATURE [App::DocumentObjectGroupPython] C_element021  label="C_element : 0.502"  # scripted group (container) (typed FeaturePython)
  n = 0.501611
FEATURE [App::DocumentObjectGroupPython] O_element019  label="O_element : 0.005"  # scripted group (container) (typed FeaturePython)
  n = 0.004527
FEATURE [App::DocumentObjectGroupPython] F_element004  label="F_element : 0.465"  # scripted group (container) (typed FeaturePython)
  n = 0.465209
FEATURE [App::DocumentObjectGroupPython] Si_element001  label="Si_element : 0.004"  # scripted group (container) (typed FeaturePython)
  n = 0.003973
FEATURE [App::DocumentObjectGroupPython] G4_C_552  label="G4_C-552"  # scripted group (container) (typed FeaturePython)
  Dunit = g/cm3
  Dvalue = 1.76
  Group = -> [H_element020,C_element021,O_element019,F_element004,Si_element001]
  conduct = 2
  density = 1
  expand = 3
  formula = G4_C-552
  name = G4_C-552
  specific = 4
FEATURE [App::DocumentObjectGroupPython] Cd_element001  label="Cd_element : 1"  # scripted group (container) (typed FeaturePython)
  n = 1
  ref = Cd_element
FEATURE [App::DocumentObjectGroupPython] Te_element001  label="Te_element : 1"  # scripted group (container) (typed FeaturePython)
  n = 1
  ref = Te_element
FEATURE [App::DocumentObjectGroupPython] G4_CADMIUM_TELLURIDE  # scripted group (container) (typed FeaturePython)
  Dunit = g/cm3
  Dvalue = 6.2
  Group = -> [Cd_element001,Te_element001]
  conduct = 2
  density = 1
  expand = 3
  formula = G4_CADMIUM_TELLURIDE
  name = G4_CADMIUM_TELLURIDE
  specific = 4
FEATURE [App::DocumentObjectGroupPython] Cd_element002  label="Cd_element : 002"  # scripted group (container) (typed FeaturePython)
  n = 1
  ref = Cd_element
FEATURE [App::DocumentObjectGroupPython] W_element001  label="W_element : 1"  # scripted group (container) (typed FeaturePython)
  n = 1
  ref = W_element
FEATURE [App::DocumentObjectGroupPython] O_element020  label="O_element : 008"  # scripted group (container) (typed FeaturePython)
  n = 4
  ref = O_element
FEATURE [App::DocumentObjectGroupPython] G4_CADMIUM_TUNGSTATE  # scripted group (container) (typed FeaturePython)
  Dunit = g/cm3
  Dvalue = 7.9
  Group = -> [Cd_element002,W_element001,O_element020]
  conduct = 2
  density = 1
  expand = 3
  formula = G4_CADMIUM_TUNGSTATE
  name = G4_CADMIUM_TUNGSTATE
  specific = 4
FEATURE [App::DocumentObjectGroupPython] Ca_element005  label="Ca_element : 1"  # scripted group (container) (typed FeaturePython)
  n = 1
  ref = Ca_element
FEATURE [App::DocumentObjectGroupPython] C_element022  label="C_element : 009"  # scripted group (container) (typed FeaturePython)
  n = 1
  ref = C_element
FEATURE [App::DocumentObjectGroupPython] O_element021  label="O_element : 009"  # scripted group (container) (typed FeaturePython)
  n = 3
  ref = O_element
FEATURE [App::DocumentObjectGroupPython] G4_CALCIUM_CARBONATE  # scripted group (container) (typed FeaturePython)
  Dunit = g/cm3
  Dvalue = 2.8
  Group = -> [Ca_element005,C_element022,O_element021]
  conduct = 2
  density = 1
  expand = 3
  formula = G4_CALCIUM_CARBONATE
  name = G4_CALCIUM_CARBONATE
  specific = 4
FEATURE [App::DocumentObjectGroupPython] Ca_element006  label="Ca_element : 002"  # scripted group (container) (typed FeaturePython)
  n = 1
  ref = Ca_element
FEATURE [App::DocumentObjectGroupPython] F_element005  label="F_element : 003"  # scripted group (container) (typed FeaturePython)
  n = 2
  ref = F_element
FEATURE [App::DocumentObjectGroupPython] G4_CALCIUM_FLUORIDE  # scripted group (container) (typed FeaturePython)
  Dunit = g/cm3
  Dvalue = 3.18
  Group = -> [Ca_element006,F_element005]
  conduct = 2
  density = 1
  expand = 3
  formula = G4_CALCIUM_FLUORIDE
  name = G4_CALCIUM_FLUORIDE
  specific = 4
FEATURE [App::DocumentObjectGroupPython] Ca_element007  label="Ca_element : 003"  # scripted group (container) (typed FeaturePython)
  n = 1
  ref = Ca_element
FEATURE [App::DocumentObjectGroupPython] O_element022  label="O_element : 010"  # scripted group (container) (typed FeaturePython)
  n = 1
  ref = O_element
FEATURE [App::DocumentObjectGroupPython] G4_CALCIUM_OXIDE  # scripted group (container) (typed FeaturePython)
  Dunit = g/cm3
  Dvalue = 3.3
  Group = -> [Ca_element007,O_element022]
  conduct = 2
  density = 1
  expand = 3
  formula = G4_CALCIUM_OXIDE
  name = G4_CALCIUM_OXIDE
  specific = 4
FEATURE [App::DocumentObjectGroupPython] Ca_element008  label="Ca_element : 004"  # scripted group (container) (typed FeaturePython)
  n = 1
  ref = Ca_element
FEATURE [App::DocumentObjectGroupPython] S_element007  label="S_element : 002"  # scripted group (container) (typed FeaturePython)
  n = 1
  ref = S_element
FEATURE [App::DocumentObjectGroupPython] O_element023  label="O_element : 011"  # scripted group (container) (typed FeaturePython)
  n = 4
  ref = O_element
FEATURE [App::DocumentObjectGroupPython] G4_CALCIUM_SULFATE  # scripted group (container) (typed FeaturePython)
  Dunit = g/cm3
  Dvalue = 2.96
  Group = -> [Ca_element008,S_element007,O_element023]
  conduct = 2
  density = 1
  expand = 3
  formula = G4_CALCIUM_SULFATE
  name = G4_CALCIUM_SULFATE
  specific = 4
FEATURE [App::DocumentObjectGroupPython] Ca_element009  label="Ca_element : 005"  # scripted group (container) (typed FeaturePython)
  n = 1
  ref = Ca_element
FEATURE [App::DocumentObjectGroupPython] W_element002  label="W_element : 002"  # scripted group (container) (typed FeaturePython)
  n = 1
  ref = W_element
FEATURE [App::DocumentObjectGroupPython] O_element024  label="O_element : 012"  # scripted group (container) (typed FeaturePython)
  n = 4
  ref = O_element
FEATURE [App::DocumentObjectGroupPython] G4_CALCIUM_TUNGSTATE  # scripted group (container) (typed FeaturePython)
  Dunit = g/cm3
  Dvalue = 6.062
  Group = -> [Ca_element009,W_element002,O_element024]
  conduct = 2
  density = 1
  expand = 3
  formula = G4_CALCIUM_TUNGSTATE
  name = G4_CALCIUM_TUNGSTATE
  specific = 4
FEATURE [App::DocumentObjectGroupPython] C_element023  label="C_element : 010"  # scripted group (container) (typed FeaturePython)
  n = 1
  ref = C_element
FEATURE [App::DocumentObjectGroupPython] O_element025  label="O_element : 013"  # scripted group (container) (typed FeaturePython)
  n = 2
  ref = O_element
FEATURE [App::DocumentObjectGroupPython] G4_CARBON_DIOXIDE  # scripted group (container) (typed FeaturePython)
  Dunit = g/cm3
  Dvalue = 0.00184212
  Group = -> [C_element023,O_element025]
  conduct = 2
  density = 1
  expand = 3
  formula = G4_CARBON_DIOXIDE
  name = G4_CARBON_DIOXIDE
  specific = 4
FEATURE [App::DocumentObjectGroupPython] C_element024  label="C_element : 011"  # scripted group (container) (typed FeaturePython)
  n = 1
  ref = C_element
FEATURE [App::DocumentObjectGroupPython] Cl_element004  label="Cl_element : 4"  # scripted group (container) (typed FeaturePython)
  n = 4
  ref = Cl_element
FEATURE [App::DocumentObjectGroupPython] G4_CARBON_TETRACHLORIDE  # scripted group (container) (typed FeaturePython)
  Dunit = g/cm3
  Dvalue = 1.594
  Group = -> [C_element024,Cl_element004]
  conduct = 2
  density = 1
  expand = 3
  formula = G4_CARBON_TETRACHLORIDE
  name = G4_CARBON_TETRACHLORIDE
  specific = 4
FEATURE [App::DocumentObjectGroupPython] C_element025  label="C_element : 012"  # scripted group (container) (typed FeaturePython)
  n = 6
  ref = C_element
FEATURE [App::DocumentObjectGroupPython] H_element021  label="H_element : 012"  # scripted group (container) (typed FeaturePython)
  n = 10
  ref = H_element
FEATURE [App::DocumentObjectGroupPython] O_element026  label="O_element : 5"  # scripted group (container) (typed FeaturePython)
  n = 5
  ref = O_element
FEATURE [App::DocumentObjectGroupPython] G4_CELLULOSE_CELLOPHANE  # scripted group (container) (typed FeaturePython)
  Dunit = g/cm3
  Dvalue = 1.42
  Group = -> [C_element025,H_element021,O_element026]
  conduct = 2
  density = 1
  expand = 3
  formula = G4_CELLULOSE_CELLOPHANE
  name = G4_CELLULOSE_CELLOPHANE
  specific = 4
FEATURE [App::DocumentObjectGroupPython] H_element022  label="H_element : 0.067"  # scripted group (container) (typed FeaturePython)
  n = 0.067125
FEATURE [App::DocumentObjectGroupPython] C_element026  label="C_element : 0.545"  # scripted group (container) (typed FeaturePython)
  n = 0.545403
FEATURE [App::DocumentObjectGroupPython] O_element027  label="O_element : 0.387"  # scripted group (container) (typed FeaturePython)
  n = 0.387472
FEATURE [App::DocumentObjectGroupPython] G4_CELLULOSE_BUTYRATE  # scripted group (container) (typed FeaturePython)
  Dunit = g/cm3
  Dvalue = 1.2
  Group = -> [H_element022,C_element026,O_element027]
  conduct = 2
  density = 1
  expand = 3
  formula = G4_CELLULOSE_BUTYRATE
  name = G4_CELLULOSE_BUTYRATE
  specific = 4
FEATURE [App::DocumentObjectGroupPython] H_element023  label="H_element : 0.029"  # scripted group (container) (typed FeaturePython)
  n = 0.029216
FEATURE [App::DocumentObjectGroupPython] C_element027  label="C_element : 0.271"  # scripted group (container) (typed FeaturePython)
  n = 0.271296
FEATURE [App::DocumentObjectGroupPython] N_element013  label="N_element : 0.121"  # scripted group (container) (typed FeaturePython)
  n = 0.121276
FEATURE [App::DocumentObjectGroupPython] O_element028  label="O_element : 0.578"  # scripted group (container) (typed FeaturePython)
  n = 0.578212
FEATURE [App::DocumentObjectGroupPython] G4_CELLULOSE_NITRATE  # scripted group (container) (typed FeaturePython)
  Dunit = g/cm3
  Dvalue = 1.49
  Group = -> [H_element023,C_element027,N_element013,O_element028]
  conduct = 2
  density = 1
  expand = 3
  formula = G4_CELLULOSE_NITRATE
  name = G4_CELLULOSE_NITRATE
  specific = 4
FEATURE [App::DocumentObjectGroupPython] H_element024  label="H_element : 0.108"  # scripted group (container) (typed FeaturePython)
  n = 0.107596
FEATURE [App::DocumentObjectGroupPython] N_element014  label="N_element : 0.001"  # scripted group (container) (typed FeaturePython)
  n = 0.0008
FEATURE [App::DocumentObjectGroupPython] O_element029  label="O_element : 0.875"  # scripted group (container) (typed FeaturePython)
  n = 0.874976
FEATURE [App::DocumentObjectGroupPython] S_element008  label="S_element : 0.015"  # scripted group (container) (typed FeaturePython)
  n = 0.014627
FEATURE [App::DocumentObjectGroupPython] Ce_element001  label="Ce_element : 0.002"  # scripted group (container) (typed FeaturePython)
  n = 0.002001
FEATURE [App::DocumentObjectGroupPython] G4_CERIC_SULFATE  # scripted group (container) (typed FeaturePython)
  Dunit = g/cm3
  Dvalue = 1.03
  Group = -> [H_element024,N_element014,O_element029,S_element008,Ce_element001]
  conduct = 2
  density = 1
  expand = 3
  formula = G4_CERIC_SULFATE
  name = G4_CERIC_SULFATE
  specific = 4
FEATURE [App::DocumentObjectGroupPython] Cs_element001  label="Cs_element : 1"  # scripted group (container) (typed FeaturePython)
  n = 1
  ref = Cs_element
FEATURE [App::DocumentObjectGroupPython] F_element006  label="F_element : 1"  # scripted group (container) (typed FeaturePython)
  n = 1
  ref = F_element
FEATURE [App::DocumentObjectGroupPython] G4_CESIUM_FLUORIDE  # scripted group (container) (typed FeaturePython)
  Dunit = g/cm3
  Dvalue = 4.115
  Group = -> [Cs_element001,F_element006]
  conduct = 2
  density = 1
  expand = 3
  formula = G4_CESIUM_FLUORIDE
  name = G4_CESIUM_FLUORIDE
  specific = 4
FEATURE [App::DocumentObjectGroupPython] Cs_element002  label="Cs_element : 002"  # scripted group (container) (typed FeaturePython)
  n = 1
  ref = Cs_element
FEATURE [App::DocumentObjectGroupPython] I_element001  label="I_element : 1"  # scripted group (container) (typed FeaturePython)
  n = 1
  ref = I_element
FEATURE [App::DocumentObjectGroupPython] G4_CESIUM_IODIDE  # scripted group (container) (typed FeaturePython)
  Dunit = g/cm3
  Dvalue = 4.51
  Group = -> [Cs_element002,I_element001]
  conduct = 2
  density = 1
  expand = 3
  formula = G4_CESIUM_IODIDE
  name = G4_CESIUM_IODIDE
  specific = 4
FEATURE [App::DocumentObjectGroupPython] C_element028  label="C_element : 013"  # scripted group (container) (typed FeaturePython)
  n = 6
  ref = C_element
FEATURE [App::DocumentObjectGroupPython] H_element025  label="H_element : 013"  # scripted group (container) (typed FeaturePython)
  n = 5
  ref = H_element
FEATURE [App::DocumentObjectGroupPython] Cl_element005  label="Cl_element : 1"  # scripted group (container) (typed FeaturePython)
  n = 1
  ref = Cl_element
FEATURE [App::DocumentObjectGroupPython] G4_CHLOROBENZENE  # scripted group (container) (typed FeaturePython)
  Dunit = g/cm3
  Dvalue = 1.1058
  Group = -> [C_element028,H_element025,Cl_element005]
  conduct = 2
  density = 1
  expand = 3
  formula = G4_CHLOROBENZENE
  name = G4_CHLOROBENZENE
  specific = 4
FEATURE [App::DocumentObjectGroupPython] C_element029  label="C_element : 014"  # scripted group (container) (typed FeaturePython)
  n = 1
  ref = C_element
FEATURE [App::DocumentObjectGroupPython] H_element026  label="H_element : 1"  # scripted group (container) (typed FeaturePython)
  n = 1
  ref = H_element
FEATURE [App::DocumentObjectGroupPython] Cl_element006  label="Cl_element : 3"  # scripted group (container) (typed FeaturePython)
  n = 3
  ref = Cl_element
FEATURE [App::DocumentObjectGroupPython] G4_CHLOROFORM  # scripted group (container) (typed FeaturePython)
  Dunit = g/cm3
  Dvalue = 1.4832
  Group = -> [C_element029,H_element026,Cl_element006]
  conduct = 2
  density = 1
  expand = 3
  formula = G4_CHLOROFORM
  name = G4_CHLOROFORM
  specific = 4
FEATURE [App::DocumentObjectGroupPython] H_element027  label="H_element : 0.010"  # scripted group (container) (typed FeaturePython)
  n = 0.01
FEATURE [App::DocumentObjectGroupPython] C_element030  label="C_element : 0.001"  # scripted group (container) (typed FeaturePython)
  n = 0.001
FEATURE [App::DocumentObjectGroupPython] O_element030  label="O_element : 0.529"  # scripted group (container) (typed FeaturePython)
  n = 0.529107
FEATURE [App::DocumentObjectGroupPython] Na_element005  label="Na_element : 0.016"  # scripted group (container) (typed FeaturePython)
  n = 0.016
FEATURE [App::DocumentObjectGroupPython] Mg_element003  label="Mg_element : 0.004"  # scripted group (container) (typed FeaturePython)
  n = 0.002
FEATURE [App::DocumentObjectGroupPython] Al_element002  label="Al_element : 0.034"  # scripted group (container) (typed FeaturePython)
  n = 0.033872
FEATURE [App::DocumentObjectGroupPython] Si_element002  label="Si_element : 0.337"  # scripted group (container) (typed FeaturePython)
  n = 0.337021
FEATURE [App::DocumentObjectGroupPython] K_element003  label="K_element : 0.013"  # scripted group (container) (typed FeaturePython)
  n = 0.013
FEATURE [App::DocumentObjectGroupPython] Ca_element010  label="Ca_element : 0.044"  # scripted group (container) (typed FeaturePython)
  n = 0.044
FEATURE [App::DocumentObjectGroupPython] Fe_element002  label="Fe_element : 0.014"  # scripted group (container) (typed FeaturePython)
  n = 0.014
FEATURE [App::DocumentObjectGroupPython] G4_CONCRETE  # scripted group (container) (typed FeaturePython)
  Dunit = g/cm3
  Dvalue = 2.3
  Group = -> [H_element027,C_element030,O_element030,Na_element005,Mg_element003,Al_element002,Si_element002,K_element003,Ca_element010,Fe_element002]
  conduct = 2
  density = 1
  expand = 3
  formula = G4_CONCRETE
  name = G4_CONCRETE
  specific = 4
FEATURE [App::DocumentObjectGroupPython] C_element031  label="C_element : 015"  # scripted group (container) (typed FeaturePython)
  n = 6
  ref = C_element
FEATURE [App::DocumentObjectGroupPython] H_element028  label="H_element : 12"  # scripted group (container) (typed FeaturePython)
  n = 12
  ref = H_element
FEATURE [App::DocumentObjectGroupPython] G4_CYCLOHEXANE  # scripted group (container) (typed FeaturePython)
  Dunit = g/cm3
  Dvalue = 0.779
  Group = -> [C_element031,H_element028]
  conduct = 2
  density = 1
  expand = 3
  formula = G4_CYCLOHEXANE
  name = G4_CYCLOHEXANE
  specific = 4
FEATURE [App::DocumentObjectGroupPython] C_element032  label="C_element : 016"  # scripted group (container) (typed FeaturePython)
  n = 6
  ref = C_element
FEATURE [App::DocumentObjectGroupPython] H_element029  label="H_element : 4"  # scripted group (container) (typed FeaturePython)
  n = 4
  ref = H_element
FEATURE [App::DocumentObjectGroupPython] Cl_element007  label="Cl_element : 2"  # scripted group (container) (typed FeaturePython)
  n = 2
  ref = Cl_element
FEATURE [App::DocumentObjectGroupPython] G4_1_2_DICHLOROBENZENE  label="G4_1.2-DICHLOROBENZENE"  # scripted group (container) (typed FeaturePython)
  Dunit = g/cm3
  Dvalue = 1.3048
  Group = -> [C_element032,H_element029,Cl_element007]
  conduct = 2
  density = 1
  expand = 3
  formula = G4_1.2-DICHLOROBENZENE
  name = G4_1.2-DICHLOROBENZENE
  specific = 4
FEATURE [App::DocumentObjectGroupPython] C_element033  label="C_element : 017"  # scripted group (container) (typed FeaturePython)
  n = 4
  ref = C_element
FEATURE [App::DocumentObjectGroupPython] H_element030  label="H_element : 8"  # scripted group (container) (typed FeaturePython)
  n = 8
  ref = H_element
FEATURE [App::DocumentObjectGroupPython] O_element031  label="O_element : 014"  # scripted group (container) (typed FeaturePython)
  n = 1
  ref = O_element
FEATURE [App::DocumentObjectGroupPython] Cl_element008  label="Cl_element : 005"  # scripted group (container) (typed FeaturePython)
  n = 2
  ref = Cl_element
FEATURE [App::DocumentObjectGroupPython] G4_DICHLORODIETHYL_ETHER  # scripted group (container) (typed FeaturePython)
  Dunit = g/cm3
  Dvalue = 1.2199
  Group = -> [C_element033,H_element030,O_element031,Cl_element008]
  conduct = 2
  density = 1
  expand = 3
  formula = G4_DICHLORODIETHYL_ETHER
  name = G4_DICHLORODIETHYL_ETHER
  specific = 4
FEATURE [App::DocumentObjectGroupPython] C_element034  label="C_element : 018"  # scripted group (container) (typed FeaturePython)
  n = 2
  ref = C_element
FEATURE [App::DocumentObjectGroupPython] H_element031  label="H_element : 014"  # scripted group (container) (typed FeaturePython)
  n = 4
  ref = H_element
FEATURE [App::DocumentObjectGroupPython] Cl_element009  label="Cl_element : 006"  # scripted group (container) (typed FeaturePython)
  n = 2
  ref = Cl_element
FEATURE [App::DocumentObjectGroupPython] G4_1_2_DICHLOROETHANE  label="G4_1.2-DICHLOROETHANE"  # scripted group (container) (typed FeaturePython)
  Dunit = g/cm3
  Dvalue = 1.2351
  Group = -> [C_element034,H_element031,Cl_element009]
  conduct = 2
  density = 1
  expand = 3
  formula = G4_1.2-DICHLOROETHANE
  name = G4_1.2-DICHLOROETHANE
  specific = 4
FEATURE [App::DocumentObjectGroupPython] C_element035  label="C_element : 019"  # scripted group (container) (typed FeaturePython)
  n = 4
  ref = C_element
FEATURE [App::DocumentObjectGroupPython] H_element032  label="H_element : 015"  # scripted group (container) (typed FeaturePython)
  n = 10
  ref = H_element
FEATURE [App::DocumentObjectGroupPython] O_element032  label="O_element : 015"  # scripted group (container) (typed FeaturePython)
  n = 1
  ref = O_element
FEATURE [App::DocumentObjectGroupPython] G4_DIETHYL_ETHER  # scripted group (container) (typed FeaturePython)
  Dunit = g/cm3
  Dvalue = 0.71378
  Group = -> [C_element035,H_element032,O_element032]
  conduct = 2
  density = 1
  expand = 3
  formula = G4_DIETHYL_ETHER
  name = G4_DIETHYL_ETHER
  specific = 4
FEATURE [App::DocumentObjectGroupPython] C_element036  label="C_element : 020"  # scripted group (container) (typed FeaturePython)
  n = 3
  ref = C_element
FEATURE [App::DocumentObjectGroupPython] H_element033  label="H_element : 016"  # scripted group (container) (typed FeaturePython)
  n = 7
  ref = H_element
FEATURE [App::DocumentObjectGroupPython] N_element015  label="N_element : 008"  # scripted group (container) (typed FeaturePython)
  n = 1
  ref = N_element
FEATURE [App::DocumentObjectGroupPython] O_element033  label="O_element : 016"  # scripted group (container) (typed FeaturePython)
  n = 1
  ref = O_element
FEATURE [App::DocumentObjectGroupPython] G4_N_N_DIMETHYL_FORMAMIDE  label="G4_N.N-DIMETHYL_FORMAMIDE"  # scripted group (container) (typed FeaturePython)
  Dunit = g/cm3
  Dvalue = 0.9487
  Group = -> [C_element036,H_element033,N_element015,O_element033]
  conduct = 2
  density = 1
  expand = 3
  formula = G4_N.N-DIMETHYL_FORMAMIDE
  name = G4_N.N-DIMETHYL_FORMAMIDE
  specific = 4
FEATURE [App::DocumentObjectGroupPython] C_element037  label="C_element : 021"  # scripted group (container) (typed FeaturePython)
  n = 2
  ref = C_element
FEATURE [App::DocumentObjectGroupPython] H_element034  label="H_element : 017"  # scripted group (container) (typed FeaturePython)
  n = 6
  ref = H_element
FEATURE [App::DocumentObjectGroupPython] O_element034  label="O_element : 017"  # scripted group (container) (typed FeaturePython)
  n = 1
  ref = O_element
FEATURE [App::DocumentObjectGroupPython] S_element009  label="S_element : 003"  # scripted group (container) (typed FeaturePython)
  n = 1
  ref = S_element
FEATURE [App::DocumentObjectGroupPython] G4_DIMETHYL_SULFOXIDE  # scripted group (container) (typed FeaturePython)
  Dunit = g/cm3
  Dvalue = 1.1014
  Group = -> [C_element037,H_element034,O_element034,S_element009]
  conduct = 2
  density = 1
  expand = 3
  formula = G4_DIMETHYL_SULFOXIDE
  name = G4_DIMETHYL_SULFOXIDE
  specific = 4
FEATURE [App::DocumentObjectGroupPython] C_element038  label="C_element : 022"  # scripted group (container) (typed FeaturePython)
  n = 2
  ref = C_element
FEATURE [App::DocumentObjectGroupPython] H_element035  label="H_element : 018"  # scripted group (container) (typed FeaturePython)
  n = 6
  ref = H_element
FEATURE [App::DocumentObjectGroupPython] G4_ETHANE  # scripted group (container) (typed FeaturePython)
  Dunit = g/cm3
  Dvalue = 0.00125324
  Group = -> [C_element038,H_element035]
  conduct = 2
  density = 1
  expand = 3
  formula = G4_ETHANE
  name = G4_ETHANE
  specific = 4
FEATURE [App::DocumentObjectGroupPython] C_element039  label="C_element : 023"  # scripted group (container) (typed FeaturePython)
  n = 2
  ref = C_element
FEATURE [App::DocumentObjectGroupPython] H_element036  label="H_element : 019"  # scripted group (container) (typed FeaturePython)
  n = 6
  ref = H_element
FEATURE [App::DocumentObjectGroupPython] O_element035  label="O_element : 018"  # scripted group (container) (typed FeaturePython)
  n = 1
  ref = O_element
FEATURE [App::DocumentObjectGroupPython] G4_ETHYL_ALCOHOL  # scripted group (container) (typed FeaturePython)
  Dunit = g/cm3
  Dvalue = 0.7893
  Group = -> [C_element039,H_element036,O_element035]
  conduct = 2
  density = 1
  expand = 3
  formula = G4_ETHYL_ALCOHOL
  name = G4_ETHYL_ALCOHOL
  specific = 4
FEATURE [App::DocumentObjectGroupPython] H_element037  label="H_element : 0.090"  # scripted group (container) (typed FeaturePython)
  n = 0.090027
FEATURE [App::DocumentObjectGroupPython] C_element040  label="C_element : 0.585"  # scripted group (container) (typed FeaturePython)
  n = 0.585182
FEATURE [App::DocumentObjectGroupPython] O_element036  label="O_element : 0.325"  # scripted group (container) (typed FeaturePython)
  n = 0.324791
FEATURE [App::DocumentObjectGroupPython] G4_ETHYL_CELLULOSE  # scripted group (container) (typed FeaturePython)
  Dunit = g/cm3
  Dvalue = 1.13
  Group = -> [H_element037,C_element040,O_element036]
  conduct = 2
  density = 1
  expand = 3
  formula = G4_ETHYL_CELLULOSE
  name = G4_ETHYL_CELLULOSE
  specific = 4
FEATURE [App::DocumentObjectGroupPython] C_element041  label="C_element : 024"  # scripted group (container) (typed FeaturePython)
  n = 2
  ref = C_element
FEATURE [App::DocumentObjectGroupPython] H_element038  label="H_element : 020"  # scripted group (container) (typed FeaturePython)
  n = 4
  ref = H_element
FEATURE [App::DocumentObjectGroupPython] G4_ETHYLENE  # scripted group (container) (typed FeaturePython)
  Dunit = g/cm3
  Dvalue = 0.00117497
  Group = -> [C_element041,H_element038]
  conduct = 2
  density = 1
  expand = 3
  formula = G4_ETHYLENE
  name = G4_ETHYLENE
  specific = 4
FEATURE [App::DocumentObjectGroupPython] H_element039  label="H_element : 0.096"  # scripted group (container) (typed FeaturePython)
  n = 0.096
FEATURE [App::DocumentObjectGroupPython] C_element042  label="C_element : 0.195"  # scripted group (container) (typed FeaturePython)
  n = 0.195
FEATURE [App::DocumentObjectGroupPython] N_element016  label="N_element : 0.057"  # scripted group (container) (typed FeaturePython)
  n = 0.057
FEATURE [App::DocumentObjectGroupPython] O_element037  label="O_element : 0.646"  # scripted group (container) (typed FeaturePython)
  n = 0.646
FEATURE [App::DocumentObjectGroupPython] Na_element006  label="Na_element : 0.017"  # scripted group (container) (typed FeaturePython)
  n = 0.001
FEATURE [App::DocumentObjectGroupPython] P_element005  label="P_element : 0.104"  # scripted group (container) (typed FeaturePython)
  n = 0.001
FEATURE [App::DocumentObjectGroupPython] S_element010  label="S_element : 0.016"  # scripted group (container) (typed FeaturePython)
  n = 0.003
FEATURE [App::DocumentObjectGroupPython] Cl_element010  label="Cl_element : 0.005"  # scripted group (container) (typed FeaturePython)
  n = 0.001
FEATURE [App::DocumentObjectGroupPython] G4_EYE_LENS_ICRP  # scripted group (container) (typed FeaturePython)
  Dunit = g/cm3
  Dvalue = 1.07
  Group = -> [H_element039,C_element042,N_element016,O_element037,Na_element006,P_element005,S_element010,Cl_element010]
  conduct = 2
  density = 1
  expand = 3
  formula = G4_EYE_LENS_ICRP
  name = G4_EYE_LENS_ICRP
  specific = 4
FEATURE [App::DocumentObjectGroupPython] Fe_element003  label="Fe_element : 2"  # scripted group (container) (typed FeaturePython)
  n = 2
  ref = Fe_element
FEATURE [App::DocumentObjectGroupPython] O_element038  label="O_element : 019"  # scripted group (container) (typed FeaturePython)
  n = 3
  ref = O_element
FEATURE [App::DocumentObjectGroupPython] G4_FERRIC_OXIDE  # scripted group (container) (typed FeaturePython)
  Dunit = g/cm3
  Dvalue = 5.2
  Group = -> [Fe_element003,O_element038]
  conduct = 2
  density = 1
  expand = 3
  formula = G4_FERRIC_OXIDE
  name = G4_FERRIC_OXIDE
  specific = 4
FEATURE [App::DocumentObjectGroupPython] Fe_element004  label="Fe_element : 1"  # scripted group (container) (typed FeaturePython)
  n = 1
  ref = Fe_element
FEATURE [App::DocumentObjectGroupPython] B_element003  label="B_element : 1"  # scripted group (container) (typed FeaturePython)
  n = 1
  ref = B_element
FEATURE [App::DocumentObjectGroupPython] G4_FERROBORIDE  # scripted group (container) (typed FeaturePython)
  Dunit = g/cm3
  Dvalue = 7.15
  Group = -> [Fe_element004,B_element003]
  conduct = 2
  density = 1
  expand = 3
  formula = G4_FERROBORIDE
  name = G4_FERROBORIDE
  specific = 4
FEATURE [App::DocumentObjectGroupPython] Fe_element005  label="Fe_element : 003"  # scripted group (container) (typed FeaturePython)
  n = 1
  ref = Fe_element
FEATURE [App::DocumentObjectGroupPython] O_element039  label="O_element : 020"  # scripted group (container) (typed FeaturePython)
  n = 1
  ref = O_element
FEATURE [App::DocumentObjectGroupPython] G4_FERROUS_OXIDE  # scripted group (container) (typed FeaturePython)
  Dunit = g/cm3
  Dvalue = 5.7
  Group = -> [Fe_element005,O_element039]
  conduct = 2
  density = 1
  expand = 3
  formula = G4_FERROUS_OXIDE
  name = G4_FERROUS_OXIDE
  specific = 4
FEATURE [App::DocumentObjectGroupPython] H_element040  label="H_element : 0.115"  # scripted group (container) (typed FeaturePython)
  n = 0.108259
FEATURE [App::DocumentObjectGroupPython] N_element017  label="N_element : 0.000"  # scripted group (container) (typed FeaturePython)
  n = 2.7e-05
FEATURE [App::DocumentObjectGroupPython] O_element040  label="O_element : 0.879"  # scripted group (container) (typed FeaturePython)
  n = 0.878636
FEATURE [App::DocumentObjectGroupPython] Na_element007  label="Na_element : 0.000"  # scripted group (container) (typed FeaturePython)
  n = 2.2e-05
FEATURE [App::DocumentObjectGroupPython] S_element011  label="S_element : 0.013"  # scripted group (container) (typed FeaturePython)
  n = 0.012968
FEATURE [App::DocumentObjectGroupPython] Cl_element011  label="Cl_element : 0.000"  # scripted group (container) (typed FeaturePython)
  n = 3.4e-05
FEATURE [App::DocumentObjectGroupPython] Fe_element006  label="Fe_element : 0.000"  # scripted group (container) (typed FeaturePython)
  n = 5.4e-05
FEATURE [App::DocumentObjectGroupPython] G4_FERROUS_SULFATE  # scripted group (container) (typed FeaturePython)
  Dunit = g/cm3
  Dvalue = 1.024
  Group = -> [H_element040,N_element017,O_element040,Na_element007,S_element011,Cl_element011,Fe_element006]
  conduct = 2
  density = 1
  expand = 3
  formula = G4_FERROUS_SULFATE
  name = G4_FERROUS_SULFATE
  specific = 4
FEATURE [App::DocumentObjectGroupPython] C_element043  label="C_element : 0.099"  # scripted group (container) (typed FeaturePython)
  n = 0.099335
FEATURE [App::DocumentObjectGroupPython] F_element007  label="F_element : 0.314"  # scripted group (container) (typed FeaturePython)
  n = 0.314247
FEATURE [App::DocumentObjectGroupPython] Cl_element012  label="Cl_element : 0.586"  # scripted group (container) (typed FeaturePython)
  n = 0.586418
FEATURE [App::DocumentObjectGroupPython] G4_FREON_12  label="G4_FREON-12"  # scripted group (container) (typed FeaturePython)
  Dunit = g/cm3
  Dvalue = 1.12
  Group = -> [C_element043,F_element007,Cl_element012]
  conduct = 2
  density = 1
  expand = 3
  formula = G4_FREON-12
  name = G4_FREON-12
  specific = 4
FEATURE [App::DocumentObjectGroupPython] C_element044  label="C_element : 0.057"  # scripted group (container) (typed FeaturePython)
  n = 0.057245
FEATURE [App::DocumentObjectGroupPython] F_element008  label="F_element : 0.181"  # scripted group (container) (typed FeaturePython)
  n = 0.181096
FEATURE [App::DocumentObjectGroupPython] Br_element001  label="Br_element : 0.762"  # scripted group (container) (typed FeaturePython)
  n = 0.761659
FEATURE [App::DocumentObjectGroupPython] G4_FREON_12B2  label="G4_FREON-12B2"  # scripted group (container) (typed FeaturePython)
  Dunit = g/cm3
  Dvalue = 1.8
  Group = -> [C_element044,F_element008,Br_element001]
  conduct = 2
  density = 1
  expand = 3
  formula = G4_FREON-12B2
  name = G4_FREON-12B2
  specific = 4
FEATURE [App::DocumentObjectGroupPython] C_element045  label="C_element : 0.115"  # scripted group (container) (typed FeaturePython)
  n = 0.114983
FEATURE [App::DocumentObjectGroupPython] F_element009  label="F_element : 0.546"  # scripted group (container) (typed FeaturePython)
  n = 0.545621
FEATURE [App::DocumentObjectGroupPython] Cl_element013  label="Cl_element : 0.339"  # scripted group (container) (typed FeaturePython)
  n = 0.339396
FEATURE [App::DocumentObjectGroupPython] G4_FREON_13  label="G4_FREON-13"  # scripted group (container) (typed FeaturePython)
  Dunit = g/cm3
  Dvalue = 0.95
  Group = -> [C_element045,F_element009,Cl_element013]
  conduct = 2
  density = 1
  expand = 3
  formula = G4_FREON-13
  name = G4_FREON-13
  specific = 4
FEATURE [App::DocumentObjectGroupPython] C_element046  label="C_element : 025"  # scripted group (container) (typed FeaturePython)
  n = 1
  ref = C_element
FEATURE [App::DocumentObjectGroupPython] F_element010  label="F_element : 3"  # scripted group (container) (typed FeaturePython)
  n = 3
  ref = F_element
FEATURE [App::DocumentObjectGroupPython] Br_element002  label="Br_element : 1"  # scripted group (container) (typed FeaturePython)
  n = 1
  ref = Br_element
FEATURE [App::DocumentObjectGroupPython] G4_FREON_13B1  label="G4_FREON-13B1"  # scripted group (container) (typed FeaturePython)
  Dunit = g/cm3
  Dvalue = 1.5
  Group = -> [C_element046,F_element010,Br_element002]
  conduct = 2
  density = 1
  expand = 3
  formula = G4_FREON-13B1
  name = G4_FREON-13B1
  specific = 4
FEATURE [App::DocumentObjectGroupPython] C_element047  label="C_element : 0.061"  # scripted group (container) (typed FeaturePython)
  n = 0.061309
FEATURE [App::DocumentObjectGroupPython] F_element011  label="F_element : 0.291"  # scripted group (container) (typed FeaturePython)
  n = 0.290924
FEATURE [App::DocumentObjectGroupPython] I_element002  label="I_element : 0.648"  # scripted group (container) (typed FeaturePython)
  n = 0.647767
FEATURE [App::DocumentObjectGroupPython] G4_FREON_13I1  label="G4_FREON-13I1"  # scripted group (container) (typed FeaturePython)
  Dunit = g/cm3
  Dvalue = 1.8
  Group = -> [C_element047,F_element011,I_element002]
  conduct = 2
  density = 1
  expand = 3
  formula = G4_FREON-13I1
  name = G4_FREON-13I1
  specific = 4
FEATURE [App::DocumentObjectGroupPython] Gd_element001  label="Gd_element : 2"  # scripted group (container) (typed FeaturePython)
  n = 2
  ref = Gd_element
FEATURE [App::DocumentObjectGroupPython] O_element041  label="O_element : 021"  # scripted group (container) (typed FeaturePython)
  n = 2
  ref = O_element
FEATURE [App::DocumentObjectGroupPython] S_element012  label="S_element : 004"  # scripted group (container) (typed FeaturePython)
  n = 1
  ref = S_element
FEATURE [App::DocumentObjectGroupPython] G4_GADOLINIUM_OXYSULFIDE  # scripted group (container) (typed FeaturePython)
  Dunit = g/cm3
  Dvalue = 7.44
  Group = -> [Gd_element001,O_element041,S_element012]
  conduct = 2
  density = 1
  expand = 3
  formula = G4_GADOLINIUM_OXYSULFIDE
  name = G4_GADOLINIUM_OXYSULFIDE
  specific = 4
FEATURE [App::DocumentObjectGroupPython] Ga_element001  label="Ga_element : 1"  # scripted group (container) (typed FeaturePython)
  n = 1
  ref = Ga_element
FEATURE [App::DocumentObjectGroupPython] As_element001  label="As_element : 1"  # scripted group (container) (typed FeaturePython)
  n = 1
  ref = As_element
FEATURE [App::DocumentObjectGroupPython] G4_GALLIUM_ARSENIDE  # scripted group (container) (typed FeaturePython)
  Dunit = g/cm3
  Dvalue = 5.31
  Group = -> [Ga_element001,As_element001]
  conduct = 2
  density = 1
  expand = 3
  formula = G4_GALLIUM_ARSENIDE
  name = G4_GALLIUM_ARSENIDE
  specific = 4
FEATURE [App::DocumentObjectGroupPython] H_element041  label="H_element : 0.081"  # scripted group (container) (typed FeaturePython)
  n = 0.08118
FEATURE [App::DocumentObjectGroupPython] C_element048  label="C_element : 0.416"  # scripted group (container) (typed FeaturePython)
  n = 0.41606
FEATURE [App::DocumentObjectGroupPython] N_element018  label="N_element : 0.111"  # scripted group (container) (typed FeaturePython)
  n = 0.11124
FEATURE [App::DocumentObjectGroupPython] O_element042  label="O_element : 0.381"  # scripted group (container) (typed FeaturePython)
  n = 0.38064
FEATURE [App::DocumentObjectGroupPython] S_element013  label="S_element : 0.011"  # scripted group (container) (typed FeaturePython)
  n = 0.01088
FEATURE [App::DocumentObjectGroupPython] G4_GEL_PHOTO_EMULSION  # scripted group (container) (typed FeaturePython)
  Dunit = g/cm3
  Dvalue = 1.2914
  Group = -> [H_element041,C_element048,N_element018,O_element042,S_element013]
  conduct = 2
  density = 1
  expand = 3
  formula = G4_GEL_PHOTO_EMULSION
  name = G4_GEL_PHOTO_EMULSION
  specific = 4
FEATURE [App::DocumentObjectGroupPython] B_element004  label="B_element : 0.040"  # scripted group (container) (typed FeaturePython)
  n = 0.0400639
FEATURE [App::DocumentObjectGroupPython] O_element043  label="O_element : 0.540"  # scripted group (container) (typed FeaturePython)
  n = 0.539561
FEATURE [App::DocumentObjectGroupPython] Na_element008  label="Na_element : 0.028"  # scripted group (container) (typed FeaturePython)
  n = 0.0281909
FEATURE [App::DocumentObjectGroupPython] Al_element003  label="Al_element : 0.012"  # scripted group (container) (typed FeaturePython)
  n = 0.011644
FEATURE [App::DocumentObjectGroupPython] Si_element003  label="Si_element : 0.377"  # scripted group (container) (typed FeaturePython)
  n = 0.377219
FEATURE [App::DocumentObjectGroupPython] K_element004  label="K_element : 0.014"  # scripted group (container) (typed FeaturePython)
  n = 0.00332099
FEATURE [App::DocumentObjectGroupPython] G4_Pyrex_Glass  # scripted group (container) (typed FeaturePython)
  Dunit = g/cm3
  Dvalue = 2.23
  Group = -> [B_element004,O_element043,Na_element008,Al_element003,Si_element003,K_element004]
  conduct = 2
  density = 1
  expand = 3
  formula = G4_Pyrex_Glass
  name = G4_Pyrex_Glass
  specific = 4
FEATURE [App::DocumentObjectGroupPython] O_element044  label="O_element : 0.156"  # scripted group (container) (typed FeaturePython)
  n = 0.156453
FEATURE [App::DocumentObjectGroupPython] Si_element004  label="Si_element : 0.081"  # scripted group (container) (typed FeaturePython)
  n = 0.080866
FEATURE [App::DocumentObjectGroupPython] Ti_element001  label="Ti_element : 0.008"  # scripted group (container) (typed FeaturePython)
  n = 0.008092
FEATURE [App::DocumentObjectGroupPython] As_element002  label="As_element : 0.003"  # scripted group (container) (typed FeaturePython)
  n = 0.002651
FEATURE [App::DocumentObjectGroupPython] Pb_element001  label="Pb_element : 0.752"  # scripted group (container) (typed FeaturePython)
  n = 0.751938
FEATURE [App::DocumentObjectGroupPython] G4_GLASS_LEAD  # scripted group (container) (typed FeaturePython)
  Dunit = g/cm3
  Dvalue = 6.22
  Group = -> [O_element044,Si_element004,Ti_element001,As_element002,Pb_element001]
  conduct = 2
  density = 1
  expand = 3
  formula = G4_GLASS_LEAD
  name = G4_GLASS_LEAD
  specific = 4
FEATURE [App::DocumentObjectGroupPython] O_element045  label="O_element : 0.460"  # scripted group (container) (typed FeaturePython)
  n = 0.4598
FEATURE [App::DocumentObjectGroupPython] Na_element009  label="Na_element : 0.096"  # scripted group (container) (typed FeaturePython)
  n = 0.0964411
FEATURE [App::DocumentObjectGroupPython] Si_element005  label="Si_element : 0.378"  # scripted group (container) (typed FeaturePython)
  n = 0.336553
FEATURE [App::DocumentObjectGroupPython] Ca_element011  label="Ca_element : 0.107"  # scripted group (container) (typed FeaturePython)
  n = 0.107205
FEATURE [App::DocumentObjectGroupPython] G4_GLASS_PLATE  # scripted group (container) (typed FeaturePython)
  Dunit = g/cm3
  Dvalue = 2.4
  Group = -> [O_element045,Na_element009,Si_element005,Ca_element011]
  conduct = 2
  density = 1
  expand = 3
  formula = G4_GLASS_PLATE
  name = G4_GLASS_PLATE
  specific = 4
FEATURE [App::DocumentObjectGroupPython] C_element049  label="C_element : 026"  # scripted group (container) (typed FeaturePython)
  n = 5
  ref = C_element
FEATURE [App::DocumentObjectGroupPython] H_element042  label="H_element : 021"  # scripted group (container) (typed FeaturePython)
  n = 10
  ref = H_element
FEATURE [App::DocumentObjectGroupPython] N_element019  label="N_element : 2"  # scripted group (container) (typed FeaturePython)
  n = 2
  ref = N_element
FEATURE [App::DocumentObjectGroupPython] O_element046  label="O_element : 022"  # scripted group (container) (typed FeaturePython)
  n = 3
  ref = O_element
FEATURE [App::DocumentObjectGroupPython] G4_GLUTAMINE  # scripted group (container) (typed FeaturePython)
  Dunit = g/cm3
  Dvalue = 1.46
  Group = -> [C_element049,H_element042,N_element019,O_element046]
  conduct = 2
  density = 1
  expand = 3
  formula = G4_GLUTAMINE
  name = G4_GLUTAMINE
  specific = 4
FEATURE [App::DocumentObjectGroupPython] C_element050  label="C_element : 027"  # scripted group (container) (typed FeaturePython)
  n = 3
  ref = C_element
FEATURE [App::DocumentObjectGroupPython] H_element043  label="H_element : 022"  # scripted group (container) (typed FeaturePython)
  n = 8
  ref = H_element
FEATURE [App::DocumentObjectGroupPython] O_element047  label="O_element : 023"  # scripted group (container) (typed FeaturePython)
  n = 3
  ref = O_element
FEATURE [App::DocumentObjectGroupPython] G4_GLYCEROL  # scripted group (container) (typed FeaturePython)
  Dunit = g/cm3
  Dvalue = 1.2613
  Group = -> [C_element050,H_element043,O_element047]
  conduct = 2
  density = 1
  expand = 3
  formula = G4_GLYCEROL
  name = G4_GLYCEROL
  specific = 4
FEATURE [App::DocumentObjectGroupPython] C_element051  label="C_element : 028"  # scripted group (container) (typed FeaturePython)
  n = 5
  ref = C_element
FEATURE [App::DocumentObjectGroupPython] H_element044  label="H_element : 023"  # scripted group (container) (typed FeaturePython)
  n = 5
  ref = H_element
FEATURE [App::DocumentObjectGroupPython] N_element020  label="N_element : 009"  # scripted group (container) (typed FeaturePython)
  n = 5
  ref = N_element
FEATURE [App::DocumentObjectGroupPython] O_element048  label="O_element : 024"  # scripted group (container) (typed FeaturePython)
  n = 1
  ref = O_element
FEATURE [App::DocumentObjectGroupPython] G4_GUANINE  # scripted group (container) (typed FeaturePython)
  Dunit = g/cm3
  Dvalue = 2.2
  Group = -> [C_element051,H_element044,N_element020,O_element048]
  conduct = 2
  density = 1
  expand = 3
  formula = G4_GUANINE
  name = G4_GUANINE
  specific = 4
FEATURE [App::DocumentObjectGroupPython] Ca_element012  label="Ca_element : 006"  # scripted group (container) (typed FeaturePython)
  n = 1
  ref = Ca_element
FEATURE [App::DocumentObjectGroupPython] S_element014  label="S_element : 005"  # scripted group (container) (typed FeaturePython)
  n = 1
  ref = S_element
FEATURE [App::DocumentObjectGroupPython] O_element049  label="O_element : 6"  # scripted group (container) (typed FeaturePython)
  n = 6
  ref = O_element
FEATURE [App::DocumentObjectGroupPython] H_element045  label="H_element : 024"  # scripted group (container) (typed FeaturePython)
  n = 4
  ref = H_element
FEATURE [App::DocumentObjectGroupPython] G4_GYPSUM  # scripted group (container) (typed FeaturePython)
  Dunit = g/cm3
  Dvalue = 2.32
  Group = -> [Ca_element012,S_element014,O_element049,H_element045]
  conduct = 2
  density = 1
  expand = 3
  formula = G4_GYPSUM
  name = G4_GYPSUM
  specific = 4
FEATURE [App::DocumentObjectGroupPython] C_element052  label="C_element : 7"  # scripted group (container) (typed FeaturePython)
  n = 7
  ref = C_element
FEATURE [App::DocumentObjectGroupPython] H_element046  label="H_element : 16"  # scripted group (container) (typed FeaturePython)
  n = 16
  ref = H_element
FEATURE [App::DocumentObjectGroupPython] G4_N_HEPTANE  label="G4_N-HEPTANE"  # scripted group (container) (typed FeaturePython)
  Dunit = g/cm3
  Dvalue = 0.68376
  Group = -> [C_element052,H_element046]
  conduct = 2
  density = 1
  expand = 3
  formula = G4_N-HEPTANE
  name = G4_N-HEPTANE
  specific = 4
FEATURE [App::DocumentObjectGroupPython] C_element053  label="C_element : 029"  # scripted group (container) (typed FeaturePython)
  n = 6
  ref = C_element
FEATURE [App::DocumentObjectGroupPython] H_element047  label="H_element : 14"  # scripted group (container) (typed FeaturePython)
  n = 14
  ref = H_element
FEATURE [App::DocumentObjectGroupPython] G4_N_HEXANE  label="G4_N-HEXANE"  # scripted group (container) (typed FeaturePython)
  Dunit = g/cm3
  Dvalue = 0.6603
  Group = -> [C_element053,H_element047]
  conduct = 2
  density = 1
  expand = 3
  formula = G4_N-HEXANE
  name = G4_N-HEXANE
  specific = 4
FEATURE [App::DocumentObjectGroupPython] C_element054  label="C_element : 22"  # scripted group (container) (typed FeaturePython)
  n = 22
  ref = C_element
FEATURE [App::DocumentObjectGroupPython] H_element048  label="H_element : 025"  # scripted group (container) (typed FeaturePython)
  n = 10
  ref = H_element
FEATURE [App::DocumentObjectGroupPython] N_element021  label="N_element : 010"  # scripted group (container) (typed FeaturePython)
  n = 2
  ref = N_element
FEATURE [App::DocumentObjectGroupPython] O_element050  label="O_element : 025"  # scripted group (container) (typed FeaturePython)
  n = 5
  ref = O_element
FEATURE [App::DocumentObjectGroupPython] G4_KAPTON  # scripted group (container) (typed FeaturePython)
  Dunit = g/cm3
  Dvalue = 1.42
  Group = -> [C_element054,H_element048,N_element021,O_element050]
  conduct = 2
  density = 1
  expand = 3
  formula = G4_KAPTON
  name = G4_KAPTON
  specific = 4
FEATURE [App::DocumentObjectGroupPython] La_element001  label="La_element : 1"  # scripted group (container) (typed FeaturePython)
  n = 1
  ref = La_element
FEATURE [App::DocumentObjectGroupPython] Br_element003  label="Br_element : 002"  # scripted group (container) (typed FeaturePython)
  n = 1
  ref = Br_element
FEATURE [App::DocumentObjectGroupPython] O_element051  label="O_element : 026"  # scripted group (container) (typed FeaturePython)
  n = 1
  ref = O_element
FEATURE [App::DocumentObjectGroupPython] G4_LANTHANUM_OXYBROMIDE  # scripted group (container) (typed FeaturePython)
  Dunit = g/cm3
  Dvalue = 6.28
  Group = -> [La_element001,Br_element003,O_element051]
  conduct = 2
  density = 1
  expand = 3
  formula = G4_LANTHANUM_OXYBROMIDE
  name = G4_LANTHANUM_OXYBROMIDE
  specific = 4
FEATURE [App::DocumentObjectGroupPython] La_element002  label="La_element : 2"  # scripted group (container) (typed FeaturePython)
  n = 2
  ref = La_element
FEATURE [App::DocumentObjectGroupPython] O_element052  label="O_element : 027"  # scripted group (container) (typed FeaturePython)
  n = 2
  ref = O_element
FEATURE [App::DocumentObjectGroupPython] S_element015  label="S_element : 006"  # scripted group (container) (typed FeaturePython)
  n = 1
  ref = S_element
FEATURE [App::DocumentObjectGroupPython] G4_LANTHANUM_OXYSULFIDE  # scripted group (container) (typed FeaturePython)
  Dunit = g/cm3
  Dvalue = 5.86
  Group = -> [La_element002,O_element052,S_element015]
  conduct = 2
  density = 1
  expand = 3
  formula = G4_LANTHANUM_OXYSULFIDE
  name = G4_LANTHANUM_OXYSULFIDE
  specific = 4
FEATURE [App::DocumentObjectGroupPython] O_element053  label="O_element : 0.072"  # scripted group (container) (typed FeaturePython)
  n = 0.071682
FEATURE [App::DocumentObjectGroupPython] Pb_element002  label="Pb_element : 0.928"  # scripted group (container) (typed FeaturePython)
  n = 0.928318
FEATURE [App::DocumentObjectGroupPython] G4_LEAD_OXIDE  # scripted group (container) (typed FeaturePython)
  Dunit = g/cm3
  Dvalue = 9.53
  Group = -> [O_element053,Pb_element002]
  conduct = 2
  density = 1
  expand = 3
  formula = G4_LEAD_OXIDE
  name = G4_LEAD_OXIDE
  specific = 4
FEATURE [App::DocumentObjectGroupPython] Li_element001  label="Li_element : 1"  # scripted group (container) (typed FeaturePython)
  n = 1
  ref = Li_element
FEATURE [App::DocumentObjectGroupPython] N_element022  label="N_element : 011"  # scripted group (container) (typed FeaturePython)
  n = 1
  ref = N_element
FEATURE [App::DocumentObjectGroupPython] H_element049  label="H_element : 026"  # scripted group (container) (typed FeaturePython)
  n = 2
  ref = H_element
FEATURE [App::DocumentObjectGroupPython] G4_LITHIUM_AMIDE  # scripted group (container) (typed FeaturePython)
  Dunit = g/cm3
  Dvalue = 1.178
  Group = -> [Li_element001,N_element022,H_element049]
  conduct = 2
  density = 1
  expand = 3
  formula = G4_LITHIUM_AMIDE
  name = G4_LITHIUM_AMIDE
  specific = 4
FEATURE [App::DocumentObjectGroupPython] Li_element002  label="Li_element : 2"  # scripted group (container) (typed FeaturePython)
  n = 2
  ref = Li_element
FEATURE [App::DocumentObjectGroupPython] C_element055  label="C_element : 030"  # scripted group (container) (typed FeaturePython)
  n = 1
  ref = C_element
FEATURE [App::DocumentObjectGroupPython] O_element054  label="O_element : 028"  # scripted group (container) (typed FeaturePython)
  n = 3
  ref = O_element
FEATURE [App::DocumentObjectGroupPython] G4_LITHIUM_CARBONATE  # scripted group (container) (typed FeaturePython)
  Dunit = g/cm3
  Dvalue = 2.11
  Group = -> [Li_element002,C_element055,O_element054]
  conduct = 2
  density = 1
  expand = 3
  formula = G4_LITHIUM_CARBONATE
  name = G4_LITHIUM_CARBONATE
  specific = 4
FEATURE [App::DocumentObjectGroupPython] Li_element003  label="Li_element : 003"  # scripted group (container) (typed FeaturePython)
  n = 1
  ref = Li_element
FEATURE [App::DocumentObjectGroupPython] F_element012  label="F_element : 004"  # scripted group (container) (typed FeaturePython)
  n = 1
  ref = F_element
FEATURE [App::DocumentObjectGroupPython] G4_LITHIUM_FLUORIDE  # scripted group (container) (typed FeaturePython)
  Dunit = g/cm3
  Dvalue = 2.635
  Group = -> [Li_element003,F_element012]
  conduct = 2
  density = 1
  expand = 3
  formula = G4_LITHIUM_FLUORIDE
  name = G4_LITHIUM_FLUORIDE
  specific = 4
FEATURE [App::DocumentObjectGroupPython] Li_element004  label="Li_element : 004"  # scripted group (container) (typed FeaturePython)
  n = 1
  ref = Li_element
FEATURE [App::DocumentObjectGroupPython] H_element050  label="H_element : 027"  # scripted group (container) (typed FeaturePython)
  n = 1
  ref = H_element
FEATURE [App::DocumentObjectGroupPython] G4_LITHIUM_HYDRIDE  # scripted group (container) (typed FeaturePython)
  Dunit = g/cm3
  Dvalue = 0.82
  Group = -> [Li_element004,H_element050]
  conduct = 2
  density = 1
  expand = 3
  formula = G4_LITHIUM_HYDRIDE
  name = G4_LITHIUM_HYDRIDE
  specific = 4
FEATURE [App::DocumentObjectGroupPython] Li_element005  label="Li_element : 005"  # scripted group (container) (typed FeaturePython)
  n = 1
  ref = Li_element
FEATURE [App::DocumentObjectGroupPython] I_element003  label="I_element : 002"  # scripted group (container) (typed FeaturePython)
  n = 1
  ref = I_element
FEATURE [App::DocumentObjectGroupPython] G4_LITHIUM_IODIDE  # scripted group (container) (typed FeaturePython)
  Dunit = g/cm3
  Dvalue = 3.494
  Group = -> [Li_element005,I_element003]
  conduct = 2
  density = 1
  expand = 3
  formula = G4_LITHIUM_IODIDE
  name = G4_LITHIUM_IODIDE
  specific = 4
FEATURE [App::DocumentObjectGroupPython] Li_element006  label="Li_element : 006"  # scripted group (container) (typed FeaturePython)
  n = 2
  ref = Li_element
FEATURE [App::DocumentObjectGroupPython] O_element055  label="O_element : 029"  # scripted group (container) (typed FeaturePython)
  n = 1
  ref = O_element
FEATURE [App::DocumentObjectGroupPython] G4_LITHIUM_OXIDE  # scripted group (container) (typed FeaturePython)
  Dunit = g/cm3
  Dvalue = 2.013
  Group = -> [Li_element006,O_element055]
  conduct = 2
  density = 1
  expand = 3
  formula = G4_LITHIUM_OXIDE
  name = G4_LITHIUM_OXIDE
  specific = 4
FEATURE [App::DocumentObjectGroupPython] Li_element007  label="Li_element : 007"  # scripted group (container) (typed FeaturePython)
  n = 2
  ref = Li_element
FEATURE [App::DocumentObjectGroupPython] B_element005  label="B_element : 005"  # scripted group (container) (typed FeaturePython)
  n = 4
  ref = B_element
FEATURE [App::DocumentObjectGroupPython] O_element056  label="O_element : 7"  # scripted group (container) (typed FeaturePython)
  n = 7
  ref = O_element
FEATURE [App::DocumentObjectGroupPython] G4_LITHIUM_TETRABORATE  # scripted group (container) (typed FeaturePython)
  Dunit = g/cm3
  Dvalue = 2.44
  Group = -> [Li_element007,B_element005,O_element056]
  conduct = 2
  density = 1
  expand = 3
  formula = G4_LITHIUM_TETRABORATE
  name = G4_LITHIUM_TETRABORATE
  specific = 4
FEATURE [App::DocumentObjectGroupPython] H_element051  label="H_element : 0.105"  # scripted group (container) (typed FeaturePython)
  n = 0.105
FEATURE [App::DocumentObjectGroupPython] C_element056  label="C_element : 0.083"  # scripted group (container) (typed FeaturePython)
  n = 0.083
FEATURE [App::DocumentObjectGroupPython] N_element023  label="N_element : 0.023"  # scripted group (container) (typed FeaturePython)
  n = 0.023
FEATURE [App::DocumentObjectGroupPython] O_element057  label="O_element : 0.779"  # scripted group (container) (typed FeaturePython)
  n = 0.779
FEATURE [App::DocumentObjectGroupPython] Na_element010  label="Na_element : 0.097"  # scripted group (container) (typed FeaturePython)
  n = 0.002
FEATURE [App::DocumentObjectGroupPython] P_element006  label="P_element : 0.105"  # scripted group (container) (typed FeaturePython)
  n = 0.001
FEATURE [App::DocumentObjectGroupPython] S_element016  label="S_element : 0.017"  # scripted group (container) (typed FeaturePython)
  n = 0.002
FEATURE [App::DocumentObjectGroupPython] Cl_element014  label="Cl_element : 0.587"  # scripted group (container) (typed FeaturePython)
  n = 0.003
FEATURE [App::DocumentObjectGroupPython] K_element005  label="K_element : 0.015"  # scripted group (container) (typed FeaturePython)
  n = 0.002
FEATURE [App::DocumentObjectGroupPython] G4_LUNG_ICRP  # scripted group (container) (typed FeaturePython)
  Dunit = g/cm3
  Dvalue = 1.04
  Group = -> [H_element051,C_element056,N_element023,O_element057,Na_element010,P_element006,S_element016,Cl_element014,K_element005]
  conduct = 2
  density = 1
  expand = 3
  formula = G4_LUNG_ICRP
  name = G4_LUNG_ICRP
  specific = 4
FEATURE [App::DocumentObjectGroupPython] H_element052  label="H_element : 0.116"  # scripted group (container) (typed FeaturePython)
  n = 0.114318
FEATURE [App::DocumentObjectGroupPython] C_element057  label="C_element : 0.656"  # scripted group (container) (typed FeaturePython)
  n = 0.655824
FEATURE [App::DocumentObjectGroupPython] O_element058  label="O_element : 0.092"  # scripted group (container) (typed FeaturePython)
  n = 0.0921831
FEATURE [App::DocumentObjectGroupPython] Mg_element004  label="Mg_element : 0.135"  # scripted group (container) (typed FeaturePython)
  n = 0.134792
FEATURE [App::DocumentObjectGroupPython] Ca_element013  label="Ca_element : 0.003"  # scripted group (container) (typed FeaturePython)
  n = 0.002883
FEATURE [App::DocumentObjectGroupPython] G4_M3_WAX  # scripted group (container) (typed FeaturePython)
  Dunit = g/cm3
  Dvalue = 1.05
  Group = -> [H_element052,C_element057,O_element058,Mg_element004,Ca_element013]
  conduct = 2
  density = 1
  expand = 3
  formula = G4_M3_WAX
  name = G4_M3_WAX
  specific = 4
FEATURE [App::DocumentObjectGroupPython] Mg_element005  label="Mg_element : 1"  # scripted group (container) (typed FeaturePython)
  n = 1
  ref = Mg_element
FEATURE [App::DocumentObjectGroupPython] C_element058  label="C_element : 031"  # scripted group (container) (typed FeaturePython)
  n = 1
  ref = C_element
FEATURE [App::DocumentObjectGroupPython] O_element059  label="O_element : 030"  # scripted group (container) (typed FeaturePython)
  n = 3
  ref = O_element
FEATURE [App::DocumentObjectGroupPython] G4_MAGNESIUM_CARBONATE  # scripted group (container) (typed FeaturePython)
  Dunit = g/cm3
  Dvalue = 2.958
  Group = -> [Mg_element005,C_element058,O_element059]
  conduct = 2
  density = 1
  expand = 3
  formula = G4_MAGNESIUM_CARBONATE
  name = G4_MAGNESIUM_CARBONATE
  specific = 4
FEATURE [App::DocumentObjectGroupPython] Mg_element006  label="Mg_element : 002"  # scripted group (container) (typed FeaturePython)
  n = 1
  ref = Mg_element
FEATURE [App::DocumentObjectGroupPython] F_element013  label="F_element : 005"  # scripted group (container) (typed FeaturePython)
  n = 2
  ref = F_element
FEATURE [App::DocumentObjectGroupPython] G4_MAGNESIUM_FLUORIDE  # scripted group (container) (typed FeaturePython)
  Dunit = g/cm3
  Dvalue = 3
  Group = -> [Mg_element006,F_element013]
  conduct = 2
  density = 1
  expand = 3
  formula = G4_MAGNESIUM_FLUORIDE
  name = G4_MAGNESIUM_FLUORIDE
  specific = 4
FEATURE [App::DocumentObjectGroupPython] Mg_element007  label="Mg_element : 003"  # scripted group (container) (typed FeaturePython)
  n = 1
  ref = Mg_element
FEATURE [App::DocumentObjectGroupPython] O_element060  label="O_element : 031"  # scripted group (container) (typed FeaturePython)
  n = 1
  ref = O_element
FEATURE [App::DocumentObjectGroupPython] G4_MAGNESIUM_OXIDE  # scripted group (container) (typed FeaturePython)
  Dunit = g/cm3
  Dvalue = 3.58
  Group = -> [Mg_element007,O_element060]
  conduct = 2
  density = 1
  expand = 3
  formula = G4_MAGNESIUM_OXIDE
  name = G4_MAGNESIUM_OXIDE
  specific = 4
FEATURE [App::DocumentObjectGroupPython] Mg_element008  label="Mg_element : 004"  # scripted group (container) (typed FeaturePython)
  n = 1
  ref = Mg_element
FEATURE [App::DocumentObjectGroupPython] B_element006  label="B_element : 006"  # scripted group (container) (typed FeaturePython)
  n = 4
  ref = B_element
FEATURE [App::DocumentObjectGroupPython] O_element061  label="O_element : 032"  # scripted group (container) (typed FeaturePython)
  n = 7
  ref = O_element
FEATURE [App::DocumentObjectGroupPython] G4_MAGNESIUM_TETRABORATE  # scripted group (container) (typed FeaturePython)
  Dunit = g/cm3
  Dvalue = 2.53
  Group = -> [Mg_element008,B_element006,O_element061]
  conduct = 2
  density = 1
  expand = 3
  formula = G4_MAGNESIUM_TETRABORATE
  name = G4_MAGNESIUM_TETRABORATE
  specific = 4
FEATURE [App::DocumentObjectGroupPython] Hg_element001  label="Hg_element : 1"  # scripted group (container) (typed FeaturePython)
  n = 1
  ref = Hg_element
FEATURE [App::DocumentObjectGroupPython] I_element004  label="I_element : 2"  # scripted group (container) (typed FeaturePython)
  n = 2
  ref = I_element
FEATURE [App::DocumentObjectGroupPython] G4_MERCURIC_IODIDE  # scripted group (container) (typed FeaturePython)
  Dunit = g/cm3
  Dvalue = 6.36
  Group = -> [Hg_element001,I_element004]
  conduct = 2
  density = 1
  expand = 3
  formula = G4_MERCURIC_IODIDE
  name = G4_MERCURIC_IODIDE
  specific = 4
FEATURE [App::DocumentObjectGroupPython] C_element059  label="C_element : 032"  # scripted group (container) (typed FeaturePython)
  n = 1
  ref = C_element
FEATURE [App::DocumentObjectGroupPython] H_element053  label="H_element : 028"  # scripted group (container) (typed FeaturePython)
  n = 4
  ref = H_element
FEATURE [App::DocumentObjectGroupPython] G4_METHANE  # scripted group (container) (typed FeaturePython)
  Dunit = g/cm3
  Dvalue = 0.000667151
  Group = -> [C_element059,H_element053]
  conduct = 2
  density = 1
  expand = 3
  formula = G4_METHANE
  name = G4_METHANE
  specific = 4
FEATURE [App::DocumentObjectGroupPython] C_element060  label="C_element : 033"  # scripted group (container) (typed FeaturePython)
  n = 1
  ref = C_element
FEATURE [App::DocumentObjectGroupPython] H_element054  label="H_element : 029"  # scripted group (container) (typed FeaturePython)
  n = 4
  ref = H_element
FEATURE [App::DocumentObjectGroupPython] O_element062  label="O_element : 033"  # scripted group (container) (typed FeaturePython)
  n = 1
  ref = O_element
FEATURE [App::DocumentObjectGroupPython] G4_METHANOL  # scripted group (container) (typed FeaturePython)
  Dunit = g/cm3
  Dvalue = 0.7914
  Group = -> [C_element060,H_element054,O_element062]
  conduct = 2
  density = 1
  expand = 3
  formula = G4_METHANOL
  name = G4_METHANOL
  specific = 4
FEATURE [App::DocumentObjectGroupPython] H_element055  label="H_element : 0.134"  # scripted group (container) (typed FeaturePython)
  n = 0.13404
FEATURE [App::DocumentObjectGroupPython] C_element061  label="C_element : 0.778"  # scripted group (container) (typed FeaturePython)
  n = 0.77796
FEATURE [App::DocumentObjectGroupPython] O_element063  label="O_element : 0.035"  # scripted group (container) (typed FeaturePython)
  n = 0.03502
FEATURE [App::DocumentObjectGroupPython] Mg_element009  label="Mg_element : 0.039"  # scripted group (container) (typed FeaturePython)
  n = 0.038594
FEATURE [App::DocumentObjectGroupPython] Ti_element002  label="Ti_element : 0.014"  # scripted group (container) (typed FeaturePython)
  n = 0.014386
FEATURE [App::DocumentObjectGroupPython] G4_MIX_D_WAX  # scripted group (container) (typed FeaturePython)
  Dunit = g/cm3
  Dvalue = 0.99
  Group = -> [H_element055,C_element061,O_element063,Mg_element009,Ti_element002]
  conduct = 2
  density = 1
  expand = 3
  formula = G4_MIX_D_WAX
  name = G4_MIX_D_WAX
  specific = 4
FEATURE [App::DocumentObjectGroupPython] H_element056  label="H_element : 0.135"  # scripted group (container) (typed FeaturePython)
  n = 0.081192
FEATURE [App::DocumentObjectGroupPython] C_element062  label="C_element : 0.583"  # scripted group (container) (typed FeaturePython)
  n = 0.583442
FEATURE [App::DocumentObjectGroupPython] N_element024  label="N_element : 0.018"  # scripted group (container) (typed FeaturePython)
  n = 0.017798
FEATURE [App::DocumentObjectGroupPython] O_element064  label="O_element : 0.186"  # scripted group (container) (typed FeaturePython)
  n = 0.186381
FEATURE [App::DocumentObjectGroupPython] Mg_element010  label="Mg_element : 0.130"  # scripted group (container) (typed FeaturePython)
  n = 0.130287
FEATURE [App::DocumentObjectGroupPython] Cl_element015  label="Cl_element : 0.588"  # scripted group (container) (typed FeaturePython)
  n = 0.0009
FEATURE [App::DocumentObjectGroupPython] G4_MS20_TISSUE  # scripted group (container) (typed FeaturePython)
  Dunit = g/cm3
  Dvalue = 1
  Group = -> [H_element056,C_element062,N_element024,O_element064,Mg_element010,Cl_element015]
  conduct = 2
  density = 1
  expand = 3
  formula = G4_MS20_TISSUE
  name = G4_MS20_TISSUE
  specific = 4
FEATURE [App::DocumentObjectGroupPython] H_element057  label="H_element : 0.136"  # scripted group (container) (typed FeaturePython)
  n = 0.102
FEATURE [App::DocumentObjectGroupPython] C_element063  label="C_element : 0.143"  # scripted group (container) (typed FeaturePython)
  n = 0.143
FEATURE [App::DocumentObjectGroupPython] N_element025  label="N_element : 0.034"  # scripted group (container) (typed FeaturePython)
  n = 0.034
FEATURE [App::DocumentObjectGroupPython] O_element065  label="O_element : 0.710"  # scripted group (container) (typed FeaturePython)
  n = 0.71
FEATURE [App::DocumentObjectGroupPython] Na_element011  label="Na_element : 0.098"  # scripted group (container) (typed FeaturePython)
  n = 0.001
FEATURE [App::DocumentObjectGroupPython] P_element007  label="P_element : 0.002"  # scripted group (container) (typed FeaturePython)
  n = 0.002
FEATURE [App::DocumentObjectGroupPython] S_element017  label="S_element : 0.018"  # scripted group (container) (typed FeaturePython)
  n = 0.003
FEATURE [App::DocumentObjectGroupPython] Cl_element016  label="Cl_element : 0.589"  # scripted group (container) (typed FeaturePython)
  n = 0.001
FEATURE [App::DocumentObjectGroupPython] K_element006  label="K_element : 0.004"  # scripted group (container) (typed FeaturePython)
  n = 0.004
FEATURE [App::DocumentObjectGroupPython] G4_MUSCLE_SKELETAL_ICRP  # scripted group (container) (typed FeaturePython)
  Dunit = g/cm3
  Dvalue = 1.05
  Group = -> [H_element057,C_element063,N_element025,O_element065,Na_element011,P_element007,S_element017,Cl_element016,K_element006]
  conduct = 2
  density = 1
  expand = 3
  formula = G4_MUSCLE_SKELETAL_ICRP
  name = G4_MUSCLE_SKELETAL_ICRP
  specific = 4
FEATURE [App::DocumentObjectGroupPython] H_element058  label="H_element : 0.137"  # scripted group (container) (typed FeaturePython)
  n = 0.102102
FEATURE [App::DocumentObjectGroupPython] C_element064  label="C_element : 0.123"  # scripted group (container) (typed FeaturePython)
  n = 0.123123
FEATURE [App::DocumentObjectGroupPython] N_element026  label="N_element : 0.756"  # scripted group (container) (typed FeaturePython)
  n = 0.035035
FEATURE [App::DocumentObjectGroupPython] O_element066  label="O_element : 0.730"  # scripted group (container) (typed FeaturePython)
  n = 0.72973
FEATURE [App::DocumentObjectGroupPython] Na_element012  label="Na_element : 0.099"  # scripted group (container) (typed FeaturePython)
  n = 0.001001
FEATURE [App::DocumentObjectGroupPython] P_element008  label="P_element : 0.106"  # scripted group (container) (typed FeaturePython)
  n = 0.002002
FEATURE [App::DocumentObjectGroupPython] S_element018  label="S_element : 0.019"  # scripted group (container) (typed FeaturePython)
  n = 0.004004
FEATURE [App::DocumentObjectGroupPython] K_element007  label="K_element : 0.016"  # scripted group (container) (typed FeaturePython)
  n = 0.003003
FEATURE [App::DocumentObjectGroupPython] G4_MUSCLE_STRIATED_ICRU  # scripted group (container) (typed FeaturePython)
  Dunit = g/cm3
  Dvalue = 1.04
  Group = -> [H_element058,C_element064,N_element026,O_element066,Na_element012,P_element008,S_element018,K_element007]
  conduct = 2
  density = 1
  expand = 3
  formula = G4_MUSCLE_STRIATED_ICRU
  name = G4_MUSCLE_STRIATED_ICRU
  specific = 4
FEATURE [App::DocumentObjectGroupPython] H_element059  label="H_element : 0.098"  # scripted group (container) (typed FeaturePython)
  n = 0.0982341
FEATURE [App::DocumentObjectGroupPython] C_element065  label="C_element : 0.156"  # scripted group (container) (typed FeaturePython)
  n = 0.156214
FEATURE [App::DocumentObjectGroupPython] N_element027  label="N_element : 0.757"  # scripted group (container) (typed FeaturePython)
  n = 0.035451
FEATURE [App::DocumentObjectGroupPython] O_element067  label="O_element : 0.880"  # scripted group (container) (typed FeaturePython)
  n = 0.710101
FEATURE [App::DocumentObjectGroupPython] G4_MUSCLE_WITH_SUCROSE  # scripted group (container) (typed FeaturePython)
  Dunit = g/cm3
  Dvalue = 1.11
  Group = -> [H_element059,C_element065,N_element027,O_element067]
  conduct = 2
  density = 1
  expand = 3
  formula = G4_MUSCLE_WITH_SUCROSE
  name = G4_MUSCLE_WITH_SUCROSE
  specific = 4
FEATURE [App::DocumentObjectGroupPython] H_element060  label="H_element : 0.138"  # scripted group (container) (typed FeaturePython)
  n = 0.101969
FEATURE [App::DocumentObjectGroupPython] C_element066  label="C_element : 0.120"  # scripted group (container) (typed FeaturePython)
  n = 0.120058
FEATURE [App::DocumentObjectGroupPython] N_element028  label="N_element : 0.758"  # scripted group (container) (typed FeaturePython)
  n = 0.035451
FEATURE [App::DocumentObjectGroupPython] O_element068  label="O_element : 0.743"  # scripted group (container) (typed FeaturePython)
  n = 0.742522
FEATURE [App::DocumentObjectGroupPython] G4_MUSCLE_WITHOUT_SUCROSE  # scripted group (container) (typed FeaturePython)
  Dunit = g/cm3
  Dvalue = 1.07
  Group = -> [H_element060,C_element066,N_element028,O_element068]
  conduct = 2
  density = 1
  expand = 3
  formula = G4_MUSCLE_WITHOUT_SUCROSE
  name = G4_MUSCLE_WITHOUT_SUCROSE
  specific = 4
FEATURE [App::DocumentObjectGroupPython] C_element067  label="C_element : 10"  # scripted group (container) (typed FeaturePython)
  n = 10
  ref = C_element
FEATURE [App::DocumentObjectGroupPython] H_element061  label="H_element : 030"  # scripted group (container) (typed FeaturePython)
  n = 8
  ref = H_element
FEATURE [App::DocumentObjectGroupPython] G4_NAPHTHALENE  # scripted group (container) (typed FeaturePython)
  Dunit = g/cm3
  Dvalue = 1.145
  Group = -> [C_element067,H_element061]
  conduct = 2
  density = 1
  expand = 3
  formula = G4_NAPHTHALENE
  name = G4_NAPHTHALENE
  specific = 4
FEATURE [App::DocumentObjectGroupPython] C_element068  label="C_element : 034"  # scripted group (container) (typed FeaturePython)
  n = 6
  ref = C_element
FEATURE [App::DocumentObjectGroupPython] H_element062  label="H_element : 031"  # scripted group (container) (typed FeaturePython)
  n = 5
  ref = H_element
FEATURE [App::DocumentObjectGroupPython] N_element029  label="N_element : 012"  # scripted group (container) (typed FeaturePython)
  n = 1
  ref = N_element
FEATURE [App::DocumentObjectGroupPython] O_element069  label="O_element : 034"  # scripted group (container) (typed FeaturePython)
  n = 2
  ref = O_element
FEATURE [App::DocumentObjectGroupPython] G4_NITROBENZENE  # scripted group (container) (typed FeaturePython)
  Dunit = g/cm3
  Dvalue = 1.19867
  Group = -> [C_element068,H_element062,N_element029,O_element069]
  conduct = 2
  density = 1
  expand = 3
  formula = G4_NITROBENZENE
  name = G4_NITROBENZENE
  specific = 4
FEATURE [App::DocumentObjectGroupPython] N_element030  label="N_element : 013"  # scripted group (container) (typed FeaturePython)
  n = 2
  ref = N_element
FEATURE [App::DocumentObjectGroupPython] O_element070  label="O_element : 035"  # scripted group (container) (typed FeaturePython)
  n = 1
  ref = O_element
FEATURE [App::DocumentObjectGroupPython] G4_NITROUS_OXIDE  # scripted group (container) (typed FeaturePython)
  Dunit = g/cm3
  Dvalue = 0.00183094
  Group = -> [N_element030,O_element070]
  conduct = 2
  density = 1
  expand = 3
  formula = G4_NITROUS_OXIDE
  name = G4_NITROUS_OXIDE
  specific = 4
FEATURE [App::DocumentObjectGroupPython] H_element063  label="H_element : 0.104"  # scripted group (container) (typed FeaturePython)
  n = 0.103509
FEATURE [App::DocumentObjectGroupPython] C_element069  label="C_element : 0.648"  # scripted group (container) (typed FeaturePython)
  n = 0.648416
FEATURE [App::DocumentObjectGroupPython] N_element031  label="N_element : 0.100"  # scripted group (container) (typed FeaturePython)
  n = 0.0995361
FEATURE [App::DocumentObjectGroupPython] O_element071  label="O_element : 0.149"  # scripted group (container) (typed FeaturePython)
  n = 0.148539
FEATURE [App::DocumentObjectGroupPython] G4_NYLON_8062  label="G4_NYLON-8062"  # scripted group (container) (typed FeaturePython)
  Dunit = g/cm3
  Dvalue = 1.08
  Group = -> [H_element063,C_element069,N_element031,O_element071]
  conduct = 2
  density = 1
  expand = 3
  formula = G4_NYLON-8062
  name = G4_NYLON-8062
  specific = 4
FEATURE [App::DocumentObjectGroupPython] C_element070  label="C_element : 035"  # scripted group (container) (typed FeaturePython)
  n = 6
  ref = C_element
FEATURE [App::DocumentObjectGroupPython] H_element064  label="H_element : 11"  # scripted group (container) (typed FeaturePython)
  n = 11
  ref = H_element
FEATURE [App::DocumentObjectGroupPython] N_element032  label="N_element : 014"  # scripted group (container) (typed FeaturePython)
  n = 1
  ref = N_element
FEATURE [App::DocumentObjectGroupPython] O_element072  label="O_element : 036"  # scripted group (container) (typed FeaturePython)
  n = 1
  ref = O_element
FEATURE [App::DocumentObjectGroupPython] G4_NYLON_6_6  label="G4_NYLON-6-6"  # scripted group (container) (typed FeaturePython)
  Dunit = g/cm3
  Dvalue = 1.14
  Group = -> [C_element070,H_element064,N_element032,O_element072]
  conduct = 2
  density = 1
  expand = 3
  formula = G4_NYLON-6-6
  name = G4_NYLON-6-6
  specific = 4
FEATURE [App::DocumentObjectGroupPython] H_element065  label="H_element : 0.139"  # scripted group (container) (typed FeaturePython)
  n = 0.107062
FEATURE [App::DocumentObjectGroupPython] C_element071  label="C_element : 0.680"  # scripted group (container) (typed FeaturePython)
  n = 0.680449
FEATURE [App::DocumentObjectGroupPython] N_element033  label="N_element : 0.099"  # scripted group (container) (typed FeaturePython)
  n = 0.099189
FEATURE [App::DocumentObjectGroupPython] O_element073  label="O_element : 0.113"  # scripted group (container) (typed FeaturePython)
  n = 0.1133
FEATURE [App::DocumentObjectGroupPython] G4_NYLON_6_10  label="G4_NYLON-6-10"  # scripted group (container) (typed FeaturePython)
  Dunit = g/cm3
  Dvalue = 1.14
  Group = -> [H_element065,C_element071,N_element033,O_element073]
  conduct = 2
  density = 1
  expand = 3
  formula = G4_NYLON-6-10
  name = G4_NYLON-6-10
  specific = 4
FEATURE [App::DocumentObjectGroupPython] H_element066  label="H_element : 0.140"  # scripted group (container) (typed FeaturePython)
  n = 0.115476
FEATURE [App::DocumentObjectGroupPython] C_element072  label="C_element : 0.721"  # scripted group (container) (typed FeaturePython)
  n = 0.720818
FEATURE [App::DocumentObjectGroupPython] N_element034  label="N_element : 0.076"  # scripted group (container) (typed FeaturePython)
  n = 0.0764169
FEATURE [App::DocumentObjectGroupPython] O_element074  label="O_element : 0.087"  # scripted group (container) (typed FeaturePython)
  n = 0.0872889
FEATURE [App::DocumentObjectGroupPython] G4_NYLON_11_RILSAN  label="G4_NYLON-11_RILSAN"  # scripted group (container) (typed FeaturePython)
  Dunit = g/cm3
  Dvalue = 1.425
  Group = -> [H_element066,C_element072,N_element034,O_element074]
  conduct = 2
  density = 1
  expand = 3
  formula = G4_NYLON-11_RILSAN
  name = G4_NYLON-11_RILSAN
  specific = 4
FEATURE [App::DocumentObjectGroupPython] C_element073  label="C_element : 8"  # scripted group (container) (typed FeaturePython)
  n = 8
  ref = C_element
FEATURE [App::DocumentObjectGroupPython] H_element067  label="H_element : 18"  # scripted group (container) (typed FeaturePython)
  n = 18
  ref = H_element
FEATURE [App::DocumentObjectGroupPython] G4_OCTANE  # scripted group (container) (typed FeaturePython)
  Dunit = g/cm3
  Dvalue = 0.7026
  Group = -> [C_element073,H_element067]
  conduct = 2
  density = 1
  expand = 3
  formula = G4_OCTANE
  name = G4_OCTANE
  specific = 4
FEATURE [App::DocumentObjectGroupPython] C_element074  label="C_element : 25"  # scripted group (container) (typed FeaturePython)
  n = 25
  ref = C_element
FEATURE [App::DocumentObjectGroupPython] H_element068  label="H_element : 52"  # scripted group (container) (typed FeaturePython)
  n = 52
  ref = H_element
FEATURE [App::DocumentObjectGroupPython] G4_PARAFFIN  # scripted group (container) (typed FeaturePython)
  Dunit = g/cm3
  Dvalue = 0.93
  Group = -> [C_element074,H_element068]
  conduct = 2
  density = 1
  expand = 3
  formula = G4_PARAFFIN
  name = G4_PARAFFIN
  specific = 4
FEATURE [App::DocumentObjectGroupPython] C_element075  label="C_element : 036"  # scripted group (container) (typed FeaturePython)
  n = 5
  ref = C_element
FEATURE [App::DocumentObjectGroupPython] H_element069  label="H_element : 032"  # scripted group (container) (typed FeaturePython)
  n = 12
  ref = H_element
FEATURE [App::DocumentObjectGroupPython] G4_N_PENTANE  label="G4_N-PENTANE"  # scripted group (container) (typed FeaturePython)
  Dunit = g/cm3
  Dvalue = 0.6262
  Group = -> [C_element075,H_element069]
  conduct = 2
  density = 1
  expand = 3
  formula = G4_N-PENTANE
  name = G4_N-PENTANE
  specific = 4
FEATURE [App::DocumentObjectGroupPython] H_element070  label="H_element : 0.014"  # scripted group (container) (typed FeaturePython)
  n = 0.0141
FEATURE [App::DocumentObjectGroupPython] C_element076  label="C_element : 0.072"  # scripted group (container) (typed FeaturePython)
  n = 0.072261
FEATURE [App::DocumentObjectGroupPython] N_element035  label="N_element : 0.019"  # scripted group (container) (typed FeaturePython)
  n = 0.01932
FEATURE [App::DocumentObjectGroupPython] O_element075  label="O_element : 0.066"  # scripted group (container) (typed FeaturePython)
  n = 0.066101
FEATURE [App::DocumentObjectGroupPython] S_element019  label="S_element : 0.020"  # scripted group (container) (typed FeaturePython)
  n = 0.00189
FEATURE [App::DocumentObjectGroupPython] Br_element004  label="Br_element : 0.349"  # scripted group (container) (typed FeaturePython)
  n = 0.349103
FEATURE [App::DocumentObjectGroupPython] Ag_element001  label="Ag_element : 0.474"  # scripted group (container) (typed FeaturePython)
  n = 0.474105
FEATURE [App::DocumentObjectGroupPython] I_element005  label="I_element : 0.003"  # scripted group (container) (typed FeaturePython)
  n = 0.00312
FEATURE [App::DocumentObjectGroupPython] G4_PHOTO_EMULSION  # scripted group (container) (typed FeaturePython)
  Dunit = g/cm3
  Dvalue = 3.815
  Group = -> [H_element070,C_element076,N_element035,O_element075,S_element019,Br_element004,Ag_element001,I_element005]
  conduct = 2
  density = 1
  expand = 3
  formula = G4_PHOTO_EMULSION
  name = G4_PHOTO_EMULSION
  specific = 4
FEATURE [App::DocumentObjectGroupPython] C_element077  label="C_element : 9"  # scripted group (container) (typed FeaturePython)
  n = 9
  ref = C_element
FEATURE [App::DocumentObjectGroupPython] H_element071  label="H_element : 033"  # scripted group (container) (typed FeaturePython)
  n = 10
  ref = H_element
FEATURE [App::DocumentObjectGroupPython] G4_PLASTIC_SC_VINYLTOLUENE  # scripted group (container) (typed FeaturePython)
  Dunit = g/cm3
  Dvalue = 1.032
  Group = -> [C_element077,H_element071]
  conduct = 2
  density = 1
  expand = 3
  formula = G4_PLASTIC_SC_VINYLTOLUENE
  name = G4_PLASTIC_SC_VINYLTOLUENE
  specific = 4
FEATURE [App::DocumentObjectGroupPython] Pu_element001  label="Pu_element : 1"  # scripted group (container) (typed FeaturePython)
  n = 1
  ref = Pu_element
FEATURE [App::DocumentObjectGroupPython] O_element076  label="O_element : 037"  # scripted group (container) (typed FeaturePython)
  n = 2
  ref = O_element
FEATURE [App::DocumentObjectGroupPython] G4_PLUTONIUM_DIOXIDE  # scripted group (container) (typed FeaturePython)
  Dunit = g/cm3
  Dvalue = 11.46
  Group = -> [Pu_element001,O_element076]
  conduct = 2
  density = 1
  expand = 3
  formula = G4_PLUTONIUM_DIOXIDE
  name = G4_PLUTONIUM_DIOXIDE
  specific = 4
FEATURE [App::DocumentObjectGroupPython] C_element078  label="C_element : 037"  # scripted group (container) (typed FeaturePython)
  n = 3
  ref = C_element
FEATURE [App::DocumentObjectGroupPython] H_element072  label="H_element : 034"  # scripted group (container) (typed FeaturePython)
  n = 3
  ref = H_element
FEATURE [App::DocumentObjectGroupPython] N_element036  label="N_element : 015"  # scripted group (container) (typed FeaturePython)
  n = 1
  ref = N_element
FEATURE [App::DocumentObjectGroupPython] G4_POLYACRYLONITRILE  # scripted group (container) (typed FeaturePython)
  Dunit = g/cm3
  Dvalue = 1.17
  Group = -> [C_element078,H_element072,N_element036]
  conduct = 2
  density = 1
  expand = 3
  formula = G4_POLYACRYLONITRILE
  name = G4_POLYACRYLONITRILE
  specific = 4
FEATURE [App::DocumentObjectGroupPython] C_element079  label="C_element : 16"  # scripted group (container) (typed FeaturePython)
  n = 16
  ref = C_element
FEATURE [App::DocumentObjectGroupPython] H_element073  label="H_element : 035"  # scripted group (container) (typed FeaturePython)
  n = 14
  ref = H_element
FEATURE [App::DocumentObjectGroupPython] O_element077  label="O_element : 038"  # scripted group (container) (typed FeaturePython)
  n = 3
  ref = O_element
FEATURE [App::DocumentObjectGroupPython] G4_POLYCARBONATE  # scripted group (container) (typed FeaturePython)
  Dunit = g/cm3
  Dvalue = 1.2
  Group = -> [C_element079,H_element073,O_element077]
  conduct = 2
  density = 1
  expand = 3
  formula = G4_POLYCARBONATE
  name = G4_POLYCARBONATE
  specific = 4
FEATURE [App::DocumentObjectGroupPython] C_element080  label="C_element : 038"  # scripted group (container) (typed FeaturePython)
  n = 8
  ref = C_element
FEATURE [App::DocumentObjectGroupPython] H_element074  label="H_element : 036"  # scripted group (container) (typed FeaturePython)
  n = 7
  ref = H_element
FEATURE [App::DocumentObjectGroupPython] Cl_element017  label="Cl_element : 007"  # scripted group (container) (typed FeaturePython)
  n = 1
  ref = Cl_element
FEATURE [App::DocumentObjectGroupPython] G4_POLYCHLOROSTYRENE  # scripted group (container) (typed FeaturePython)
  Dunit = g/cm3
  Dvalue = 1.3
  Group = -> [C_element080,H_element074,Cl_element017]
  conduct = 2
  density = 1
  expand = 3
  formula = G4_POLYCHLOROSTYRENE
  name = G4_POLYCHLOROSTYRENE
  specific = 4
FEATURE [App::DocumentObjectGroupPython] C_element081  label="C_element : 039"  # scripted group (container) (typed FeaturePython)
  n = 1
  ref = C_element
FEATURE [App::DocumentObjectGroupPython] H_element075  label="H_element : 037"  # scripted group (container) (typed FeaturePython)
  n = 2
  ref = H_element
FEATURE [App::DocumentObjectGroupPython] G4_POLYETHYLENE  # scripted group (container) (typed FeaturePython)
  Dunit = g/cm3
  Dvalue = 0.94
  Group = -> [C_element081,H_element075]
  conduct = 2
  density = 1
  expand = 3
  formula = G4_POLYETHYLENE
  name = G4_POLYETHYLENE
  specific = 4
FEATURE [App::DocumentObjectGroupPython] C_element082  label="C_element : 040"  # scripted group (container) (typed FeaturePython)
  n = 10
  ref = C_element
FEATURE [App::DocumentObjectGroupPython] H_element076  label="H_element : 038"  # scripted group (container) (typed FeaturePython)
  n = 8
  ref = H_element
FEATURE [App::DocumentObjectGroupPython] O_element078  label="O_element : 039"  # scripted group (container) (typed FeaturePython)
  n = 4
  ref = O_element
FEATURE [App::DocumentObjectGroupPython] G4_MYLAR  # scripted group (container) (typed FeaturePython)
  Dunit = g/cm3
  Dvalue = 1.4
  Group = -> [C_element082,H_element076,O_element078]
  conduct = 2
  density = 1
  expand = 3
  formula = G4_MYLAR
  name = G4_MYLAR
  specific = 4
FEATURE [App::DocumentObjectGroupPython] C_element083  label="C_element : 041"  # scripted group (container) (typed FeaturePython)
  n = 5
  ref = C_element
FEATURE [App::DocumentObjectGroupPython] H_element077  label="H_element : 039"  # scripted group (container) (typed FeaturePython)
  n = 8
  ref = H_element
FEATURE [App::DocumentObjectGroupPython] O_element079  label="O_element : 040"  # scripted group (container) (typed FeaturePython)
  n = 2
  ref = O_element
FEATURE [App::DocumentObjectGroupPython] G4_PLEXIGLASS  # scripted group (container) (typed FeaturePython)
  Dunit = g/cm3
  Dvalue = 1.19
  Group = -> [C_element083,H_element077,O_element079]
  conduct = 2
  density = 1
  expand = 3
  formula = G4_PLEXIGLASS
  name = G4_PLEXIGLASS
  specific = 4
FEATURE [App::DocumentObjectGroupPython] C_element084  label="C_element : 042"  # scripted group (container) (typed FeaturePython)
  n = 1
  ref = C_element
FEATURE [App::DocumentObjectGroupPython] H_element078  label="H_element : 040"  # scripted group (container) (typed FeaturePython)
  n = 2
  ref = H_element
FEATURE [App::DocumentObjectGroupPython] O_element080  label="O_element : 041"  # scripted group (container) (typed FeaturePython)
  n = 1
  ref = O_element
FEATURE [App::DocumentObjectGroupPython] G4_POLYOXYMETHYLENE  # scripted group (container) (typed FeaturePython)
  Dunit = g/cm3
  Dvalue = 1.425
  Group = -> [C_element084,H_element078,O_element080]
  conduct = 2
  density = 1
  expand = 3
  formula = G4_POLYOXYMETHYLENE
  name = G4_POLYOXYMETHYLENE
  specific = 4
FEATURE [App::DocumentObjectGroupPython] C_element085  label="C_element : 043"  # scripted group (container) (typed FeaturePython)
  n = 2
  ref = C_element
FEATURE [App::DocumentObjectGroupPython] H_element079  label="H_element : 041"  # scripted group (container) (typed FeaturePython)
  n = 4
  ref = H_element
FEATURE [App::DocumentObjectGroupPython] G4_POLYPROPYLENE  # scripted group (container) (typed FeaturePython)
  Dunit = g/cm3
  Dvalue = 0.9
  Group = -> [C_element085,H_element079]
  conduct = 2
  density = 1
  expand = 3
  formula = G4_POLYPROPYLENE
  name = G4_POLYPROPYLENE
  specific = 4
FEATURE [App::DocumentObjectGroupPython] C_element086  label="C_element : 044"  # scripted group (container) (typed FeaturePython)
  n = 8
  ref = C_element
FEATURE [App::DocumentObjectGroupPython] H_element080  label="H_element : 042"  # scripted group (container) (typed FeaturePython)
  n = 8
  ref = H_element
FEATURE [App::DocumentObjectGroupPython] G4_POLYSTYRENE  # scripted group (container) (typed FeaturePython)
  Dunit = g/cm3
  Dvalue = 1.06
  Group = -> [C_element086,H_element080]
  conduct = 2
  density = 1
  expand = 3
  formula = G4_POLYSTYRENE
  name = G4_POLYSTYRENE
  specific = 4
FEATURE [App::DocumentObjectGroupPython] C_element087  label="C_element : 045"  # scripted group (container) (typed FeaturePython)
  n = 2
  ref = C_element
FEATURE [App::DocumentObjectGroupPython] F_element014  label="F_element : 4"  # scripted group (container) (typed FeaturePython)
  n = 4
  ref = F_element
FEATURE [App::DocumentObjectGroupPython] G4_TEFLON  # scripted group (container) (typed FeaturePython)
  Dunit = g/cm3
  Dvalue = 2.2
  Group = -> [C_element087,F_element014]
  conduct = 2
  density = 1
  expand = 3
  formula = G4_TEFLON
  name = G4_TEFLON
  specific = 4
FEATURE [App::DocumentObjectGroupPython] C_element088  label="C_element : 046"  # scripted group (container) (typed FeaturePython)
  n = 2
  ref = C_element
FEATURE [App::DocumentObjectGroupPython] F_element015  label="F_element : 006"  # scripted group (container) (typed FeaturePython)
  n = 3
  ref = F_element
FEATURE [App::DocumentObjectGroupPython] Cl_element018  label="Cl_element : 008"  # scripted group (container) (typed FeaturePython)
  n = 1
  ref = Cl_element
FEATURE [App::DocumentObjectGroupPython] G4_POLYTRIFLUOROCHLOROETHYLENE  # scripted group (container) (typed FeaturePython)
  Dunit = g/cm3
  Dvalue = 2.1
  Group = -> [C_element088,F_element015,Cl_element018]
  conduct = 2
  density = 1
  expand = 3
  formula = G4_POLYTRIFLUOROCHLOROETHYLENE
  name = G4_POLYTRIFLUOROCHLOROETHYLENE
  specific = 4
FEATURE [App::DocumentObjectGroupPython] C_element089  label="C_element : 047"  # scripted group (container) (typed FeaturePython)
  n = 4
  ref = C_element
FEATURE [App::DocumentObjectGroupPython] H_element081  label="H_element : 043"  # scripted group (container) (typed FeaturePython)
  n = 6
  ref = H_element
FEATURE [App::DocumentObjectGroupPython] O_element081  label="O_element : 042"  # scripted group (container) (typed FeaturePython)
  n = 2
  ref = O_element
FEATURE [App::DocumentObjectGroupPython] G4_POLYVINYL_ACETATE  # scripted group (container) (typed FeaturePython)
  Dunit = g/cm3
  Dvalue = 1.19
  Group = -> [C_element089,H_element081,O_element081]
  conduct = 2
  density = 1
  expand = 3
  formula = G4_POLYVINYL_ACETATE
  name = G4_POLYVINYL_ACETATE
  specific = 4
FEATURE [App::DocumentObjectGroupPython] C_element090  label="C_element : 048"  # scripted group (container) (typed FeaturePython)
  n = 2
  ref = C_element
FEATURE [App::DocumentObjectGroupPython] H_element082  label="H_element : 044"  # scripted group (container) (typed FeaturePython)
  n = 4
  ref = H_element
FEATURE [App::DocumentObjectGroupPython] O_element082  label="O_element : 043"  # scripted group (container) (typed FeaturePython)
  n = 1
  ref = O_element
FEATURE [App::DocumentObjectGroupPython] G4_POLYVINYL_ALCOHOL  # scripted group (container) (typed FeaturePython)
  Dunit = g/cm3
  Dvalue = 1.3
  Group = -> [C_element090,H_element082,O_element082]
  conduct = 2
  density = 1
  expand = 3
  formula = G4_POLYVINYL_ALCOHOL
  name = G4_POLYVINYL_ALCOHOL
  specific = 4
FEATURE [App::DocumentObjectGroupPython] C_element091  label="C_element : 049"  # scripted group (container) (typed FeaturePython)
  n = 8
  ref = C_element
FEATURE [App::DocumentObjectGroupPython] H_element083  label="H_element : 045"  # scripted group (container) (typed FeaturePython)
  n = 14
  ref = H_element
FEATURE [App::DocumentObjectGroupPython] O_element083  label="O_element : 044"  # scripted group (container) (typed FeaturePython)
  n = 2
  ref = O_element
FEATURE [App::DocumentObjectGroupPython] G4_POLYVINYL_BUTYRAL  # scripted group (container) (typed FeaturePython)
  Dunit = g/cm3
  Dvalue = 1.12
  Group = -> [C_element091,H_element083,O_element083]
  conduct = 2
  density = 1
  expand = 3
  formula = G4_POLYVINYL_BUTYRAL
  name = G4_POLYVINYL_BUTYRAL
  specific = 4
FEATURE [App::DocumentObjectGroupPython] C_element092  label="C_element : 050"  # scripted group (container) (typed FeaturePython)
  n = 2
  ref = C_element
FEATURE [App::DocumentObjectGroupPython] H_element084  label="H_element : 046"  # scripted group (container) (typed FeaturePython)
  n = 3
  ref = H_element
FEATURE [App::DocumentObjectGroupPython] Cl_element019  label="Cl_element : 009"  # scripted group (container) (typed FeaturePython)
  n = 1
  ref = Cl_element
FEATURE [App::DocumentObjectGroupPython] G4_POLYVINYL_CHLORIDE  # scripted group (container) (typed FeaturePython)
  Dunit = g/cm3
  Dvalue = 1.3
  Group = -> [C_element092,H_element084,Cl_element019]
  conduct = 2
  density = 1
  expand = 3
  formula = G4_POLYVINYL_CHLORIDE
  name = G4_POLYVINYL_CHLORIDE
  specific = 4
FEATURE [App::DocumentObjectGroupPython] C_element093  label="C_element : 051"  # scripted group (container) (typed FeaturePython)
  n = 2
  ref = C_element
FEATURE [App::DocumentObjectGroupPython] H_element085  label="H_element : 047"  # scripted group (container) (typed FeaturePython)
  n = 2
  ref = H_element
FEATURE [App::DocumentObjectGroupPython] Cl_element020  label="Cl_element : 010"  # scripted group (container) (typed FeaturePython)
  n = 2
  ref = Cl_element
FEATURE [App::DocumentObjectGroupPython] G4_POLYVINYLIDENE_CHLORIDE  # scripted group (container) (typed FeaturePython)
  Dunit = g/cm3
  Dvalue = 1.7
  Group = -> [C_element093,H_element085,Cl_element020]
  conduct = 2
  density = 1
  expand = 3
  formula = G4_POLYVINYLIDENE_CHLORIDE
  name = G4_POLYVINYLIDENE_CHLORIDE
  specific = 4
FEATURE [App::DocumentObjectGroupPython] C_element094  label="C_element : 052"  # scripted group (container) (typed FeaturePython)
  n = 2
  ref = C_element
FEATURE [App::DocumentObjectGroupPython] H_element086  label="H_element : 048"  # scripted group (container) (typed FeaturePython)
  n = 2
  ref = H_element
FEATURE [App::DocumentObjectGroupPython] F_element016  label="F_element : 007"  # scripted group (container) (typed FeaturePython)
  n = 2
  ref = F_element
FEATURE [App::DocumentObjectGroupPython] G4_POLYVINYLIDENE_FLUORIDE  # scripted group (container) (typed FeaturePython)
  Dunit = g/cm3
  Dvalue = 1.76
  Group = -> [C_element094,H_element086,F_element016]
  conduct = 2
  density = 1
  expand = 3
  formula = G4_POLYVINYLIDENE_FLUORIDE
  name = G4_POLYVINYLIDENE_FLUORIDE
  specific = 4
FEATURE [App::DocumentObjectGroupPython] C_element095  label="C_element : 053"  # scripted group (container) (typed FeaturePython)
  n = 6
  ref = C_element
FEATURE [App::DocumentObjectGroupPython] H_element087  label="H_element : 9"  # scripted group (container) (typed FeaturePython)
  n = 9
  ref = H_element
FEATURE [App::DocumentObjectGroupPython] N_element037  label="N_element : 016"  # scripted group (container) (typed FeaturePython)
  n = 1
  ref = N_element
FEATURE [App::DocumentObjectGroupPython] O_element084  label="O_element : 045"  # scripted group (container) (typed FeaturePython)
  n = 1
  ref = O_element
FEATURE [App::DocumentObjectGroupPython] G4_POLYVINYL_PYRROLIDONE  # scripted group (container) (typed FeaturePython)
  Dunit = g/cm3
  Dvalue = 1.25
  Group = -> [C_element095,H_element087,N_element037,O_element084]
  conduct = 2
  density = 1
  expand = 3
  formula = G4_POLYVINYL_PYRROLIDONE
  name = G4_POLYVINYL_PYRROLIDONE
  specific = 4
FEATURE [App::DocumentObjectGroupPython] K_element008  label="K_element : 1"  # scripted group (container) (typed FeaturePython)
  n = 1
  ref = K_element
FEATURE [App::DocumentObjectGroupPython] I_element006  label="I_element : 003"  # scripted group (container) (typed FeaturePython)
  n = 1
  ref = I_element
FEATURE [App::DocumentObjectGroupPython] G4_POTASSIUM_IODIDE  # scripted group (container) (typed FeaturePython)
  Dunit = g/cm3
  Dvalue = 3.13
  Group = -> [K_element008,I_element006]
  conduct = 2
  density = 1
  expand = 3
  formula = G4_POTASSIUM_IODIDE
  name = G4_POTASSIUM_IODIDE
  specific = 4
FEATURE [App::DocumentObjectGroupPython] K_element009  label="K_element : 2"  # scripted group (container) (typed FeaturePython)
  n = 2
  ref = K_element
FEATURE [App::DocumentObjectGroupPython] O_element085  label="O_element : 046"  # scripted group (container) (typed FeaturePython)
  n = 1
  ref = O_element
FEATURE [App::DocumentObjectGroupPython] G4_POTASSIUM_OXIDE  # scripted group (container) (typed FeaturePython)
  Dunit = g/cm3
  Dvalue = 2.32
  Group = -> [K_element009,O_element085]
  conduct = 2
  density = 1
  expand = 3
  formula = G4_POTASSIUM_OXIDE
  name = G4_POTASSIUM_OXIDE
  specific = 4
FEATURE [App::DocumentObjectGroupPython] C_element096  label="C_element : 054"  # scripted group (container) (typed FeaturePython)
  n = 3
  ref = C_element
FEATURE [App::DocumentObjectGroupPython] H_element088  label="H_element : 049"  # scripted group (container) (typed FeaturePython)
  n = 8
  ref = H_element
FEATURE [App::DocumentObjectGroupPython] G4_PROPANE  # scripted group (container) (typed FeaturePython)
  Dunit = g/cm3
  Dvalue = 0.00187939
  Group = -> [C_element096,H_element088]
  conduct = 2
  density = 1
  expand = 3
  formula = G4_PROPANE
  name = G4_PROPANE
  specific = 4
FEATURE [App::DocumentObjectGroupPython] C_element097  label="C_element : 055"  # scripted group (container) (typed FeaturePython)
  n = 3
  ref = C_element
FEATURE [App::DocumentObjectGroupPython] H_element089  label="H_element : 050"  # scripted group (container) (typed FeaturePython)
  n = 8
  ref = H_element
FEATURE [App::DocumentObjectGroupPython] G4_lPROPANE  # scripted group (container) (typed FeaturePython)
  Dunit = g/cm3
  Dvalue = 0.43
  Group = -> [C_element097,H_element089]
  conduct = 2
  density = 1
  expand = 3
  formula = G4_lPROPANE
  name = G4_lPROPANE
  specific = 4
FEATURE [App::DocumentObjectGroupPython] C_element098  label="C_element : 056"  # scripted group (container) (typed FeaturePython)
  n = 3
  ref = C_element
FEATURE [App::DocumentObjectGroupPython] H_element090  label="H_element : 051"  # scripted group (container) (typed FeaturePython)
  n = 8
  ref = H_element
FEATURE [App::DocumentObjectGroupPython] O_element086  label="O_element : 047"  # scripted group (container) (typed FeaturePython)
  n = 1
  ref = O_element
FEATURE [App::DocumentObjectGroupPython] G4_N_PROPYL_ALCOHOL  label="G4_N-PROPYL_ALCOHOL"  # scripted group (container) (typed FeaturePython)
  Dunit = g/cm3
  Dvalue = 0.8035
  Group = -> [C_element098,H_element090,O_element086]
  conduct = 2
  density = 1
  expand = 3
  formula = G4_N-PROPYL_ALCOHOL
  name = G4_N-PROPYL_ALCOHOL
  specific = 4
FEATURE [App::DocumentObjectGroupPython] C_element099  label="C_element : 057"  # scripted group (container) (typed FeaturePython)
  n = 5
  ref = C_element
FEATURE [App::DocumentObjectGroupPython] H_element091  label="H_element : 052"  # scripted group (container) (typed FeaturePython)
  n = 5
  ref = H_element
FEATURE [App::DocumentObjectGroupPython] N_element038  label="N_element : 017"  # scripted group (container) (typed FeaturePython)
  n = 1
  ref = N_element
FEATURE [App::DocumentObjectGroupPython] G4_PYRIDINE  # scripted group (container) (typed FeaturePython)
  Dunit = g/cm3
  Dvalue = 0.9819
  Group = -> [C_element099,H_element091,N_element038]
  conduct = 2
  density = 1
  expand = 3
  formula = G4_PYRIDINE
  name = G4_PYRIDINE
  specific = 4
FEATURE [App::DocumentObjectGroupPython] H_element092  label="H_element : 0.144"  # scripted group (container) (typed FeaturePython)
  n = 0.143711
FEATURE [App::DocumentObjectGroupPython] C_element100  label="C_element : 0.856"  # scripted group (container) (typed FeaturePython)
  n = 0.856289
FEATURE [App::DocumentObjectGroupPython] G4_RUBBER_BUTYL  # scripted group (container) (typed FeaturePython)
  Dunit = g/cm3
  Dvalue = 0.92
  Group = -> [H_element092,C_element100]
  conduct = 2
  density = 1
  expand = 3
  formula = G4_RUBBER_BUTYL
  name = G4_RUBBER_BUTYL
  specific = 4
FEATURE [App::DocumentObjectGroupPython] H_element093  label="H_element : 0.118"  # scripted group (container) (typed FeaturePython)
  n = 0.118371
FEATURE [App::DocumentObjectGroupPython] C_element101  label="C_element : 0.882"  # scripted group (container) (typed FeaturePython)
  n = 0.881629
FEATURE [App::DocumentObjectGroupPython] G4_RUBBER_NATURAL  # scripted group (container) (typed FeaturePython)
  Dunit = g/cm3
  Dvalue = 0.92
  Group = -> [H_element093,C_element101]
  conduct = 2
  density = 1
  expand = 3
  formula = G4_RUBBER_NATURAL
  name = G4_RUBBER_NATURAL
  specific = 4
FEATURE [App::DocumentObjectGroupPython] H_element094  label="H_element : 0.145"  # scripted group (container) (typed FeaturePython)
  n = 0.05692
FEATURE [App::DocumentObjectGroupPython] C_element102  label="C_element : 0.543"  # scripted group (container) (typed FeaturePython)
  n = 0.542646
FEATURE [App::DocumentObjectGroupPython] Cl_element021  label="Cl_element : 0.400"  # scripted group (container) (typed FeaturePython)
  n = 0.400434
FEATURE [App::DocumentObjectGroupPython] G4_RUBBER_NEOPRENE  # scripted group (container) (typed FeaturePython)
  Dunit = g/cm3
  Dvalue = 1.23
  Group = -> [H_element094,C_element102,Cl_element021]
  conduct = 2
  density = 1
  expand = 3
  formula = G4_RUBBER_NEOPRENE
  name = G4_RUBBER_NEOPRENE
  specific = 4
FEATURE [App::DocumentObjectGroupPython] Si_element006  label="Si_element : 1"  # scripted group (container) (typed FeaturePython)
  n = 1
  ref = Si_element
FEATURE [App::DocumentObjectGroupPython] O_element087  label="O_element : 048"  # scripted group (container) (typed FeaturePython)
  n = 2
  ref = O_element
FEATURE [App::DocumentObjectGroupPython] G4_SILICON_DIOXIDE  # scripted group (container) (typed FeaturePython)
  Dunit = g/cm3
  Dvalue = 2.32
  Group = -> [Si_element006,O_element087]
  conduct = 2
  density = 1
  expand = 3
  formula = G4_SILICON_DIOXIDE
  name = G4_SILICON_DIOXIDE
  specific = 4
FEATURE [App::DocumentObjectGroupPython] Ag_element002  label="Ag_element : 1"  # scripted group (container) (typed FeaturePython)
  n = 1
  ref = Ag_element
FEATURE [App::DocumentObjectGroupPython] Br_element005  label="Br_element : 003"  # scripted group (container) (typed FeaturePython)
  n = 1
  ref = Br_element
FEATURE [App::DocumentObjectGroupPython] G4_SILVER_BROMIDE  # scripted group (container) (typed FeaturePython)
  Dunit = g/cm3
  Dvalue = 6.473
  Group = -> [Ag_element002,Br_element005]
  conduct = 2
  density = 1
  expand = 3
  formula = G4_SILVER_BROMIDE
  name = G4_SILVER_BROMIDE
  specific = 4
FEATURE [App::DocumentObjectGroupPython] Ag_element003  label="Ag_element : 002"  # scripted group (container) (typed FeaturePython)
  n = 1
  ref = Ag_element
FEATURE [App::DocumentObjectGroupPython] Cl_element022  label="Cl_element : 011"  # scripted group (container) (typed FeaturePython)
  n = 1
  ref = Cl_element
FEATURE [App::DocumentObjectGroupPython] G4_SILVER_CHLORIDE  # scripted group (container) (typed FeaturePython)
  Dunit = g/cm3
  Dvalue = 5.56
  Group = -> [Ag_element003,Cl_element022]
  conduct = 2
  density = 1
  expand = 3
  formula = G4_SILVER_CHLORIDE
  name = G4_SILVER_CHLORIDE
  specific = 4
FEATURE [App::DocumentObjectGroupPython] Br_element006  label="Br_element : 0.423"  # scripted group (container) (typed FeaturePython)
  n = 0.422895
FEATURE [App::DocumentObjectGroupPython] Ag_element004  label="Ag_element : 0.574"  # scripted group (container) (typed FeaturePython)
  n = 0.573748
FEATURE [App::DocumentObjectGroupPython] I_element007  label="I_element : 0.649"  # scripted group (container) (typed FeaturePython)
  n = 0.003357
FEATURE [App::DocumentObjectGroupPython] G4_SILVER_HALIDES  # scripted group (container) (typed FeaturePython)
  Dunit = g/cm3
  Dvalue = 6.47
  Group = -> [Br_element006,Ag_element004,I_element007]
  conduct = 2
  density = 1
  expand = 3
  formula = G4_SILVER_HALIDES
  name = G4_SILVER_HALIDES
  specific = 4
FEATURE [App::DocumentObjectGroupPython] Ag_element005  label="Ag_element : 003"  # scripted group (container) (typed FeaturePython)
  n = 1
  ref = Ag_element
FEATURE [App::DocumentObjectGroupPython] I_element008  label="I_element : 004"  # scripted group (container) (typed FeaturePython)
  n = 1
  ref = I_element
FEATURE [App::DocumentObjectGroupPython] G4_SILVER_IODIDE  # scripted group (container) (typed FeaturePython)
  Dunit = g/cm3
  Dvalue = 6.01
  Group = -> [Ag_element005,I_element008]
  conduct = 2
  density = 1
  expand = 3
  formula = G4_SILVER_IODIDE
  name = G4_SILVER_IODIDE
  specific = 4
FEATURE [App::DocumentObjectGroupPython] H_element095  label="H_element : 0.100"  # scripted group (container) (typed FeaturePython)
  n = 0.1
FEATURE [App::DocumentObjectGroupPython] C_element103  label="C_element : 0.204"  # scripted group (container) (typed FeaturePython)
  n = 0.204
FEATURE [App::DocumentObjectGroupPython] N_element039  label="N_element : 0.759"  # scripted group (container) (typed FeaturePython)
  n = 0.042
FEATURE [App::DocumentObjectGroupPython] O_element088  label="O_element : 0.645"  # scripted group (container) (typed FeaturePython)
  n = 0.645
FEATURE [App::DocumentObjectGroupPython] Na_element013  label="Na_element : 0.100"  # scripted group (container) (typed FeaturePython)
  n = 0.002
FEATURE [App::DocumentObjectGroupPython] P_element009  label="P_element : 0.107"  # scripted group (container) (typed FeaturePython)
  n = 0.001
FEATURE [App::DocumentObjectGroupPython] S_element020  label="S_element : 0.021"  # scripted group (container) (typed FeaturePython)
  n = 0.002
FEATURE [App::DocumentObjectGroupPython] Cl_element023  label="Cl_element : 0.590"  # scripted group (container) (typed FeaturePython)
  n = 0.003
FEATURE [App::DocumentObjectGroupPython] K_element010  label="K_element : 0.001"  # scripted group (container) (typed FeaturePython)
  n = 0.001
FEATURE [App::DocumentObjectGroupPython] G4_SKIN_ICRP  # scripted group (container) (typed FeaturePython)
  Dunit = g/cm3
  Dvalue = 1.09
  Group = -> [H_element095,C_element103,N_element039,O_element088,Na_element013,P_element009,S_element020,Cl_element023,K_element010]
  conduct = 2
  density = 1
  expand = 3
  formula = G4_SKIN_ICRP
  name = G4_SKIN_ICRP
  specific = 4
FEATURE [App::DocumentObjectGroupPython] Na_element014  label="Na_element : 2"  # scripted group (container) (typed FeaturePython)
  n = 2
  ref = Na_element
FEATURE [App::DocumentObjectGroupPython] C_element104  label="C_element : 058"  # scripted group (container) (typed FeaturePython)
  n = 1
  ref = C_element
FEATURE [App::DocumentObjectGroupPython] O_element089  label="O_element : 049"  # scripted group (container) (typed FeaturePython)
  n = 3
  ref = O_element
FEATURE [App::DocumentObjectGroupPython] G4_SODIUM_CARBONATE  # scripted group (container) (typed FeaturePython)
  Dunit = g/cm3
  Dvalue = 2.532
  Group = -> [Na_element014,C_element104,O_element089]
  conduct = 2
  density = 1
  expand = 3
  formula = G4_SODIUM_CARBONATE
  name = G4_SODIUM_CARBONATE
  specific = 4
FEATURE [App::DocumentObjectGroupPython] Na_element015  label="Na_element : 1"  # scripted group (container) (typed FeaturePython)
  n = 1
  ref = Na_element
FEATURE [App::DocumentObjectGroupPython] I_element009  label="I_element : 005"  # scripted group (container) (typed FeaturePython)
  n = 1
  ref = I_element
FEATURE [App::DocumentObjectGroupPython] G4_SODIUM_IODIDE  # scripted group (container) (typed FeaturePython)
  Dunit = g/cm3
  Dvalue = 3.667
  Group = -> [Na_element015,I_element009]
  conduct = 2
  density = 1
  expand = 3
  formula = G4_SODIUM_IODIDE
  name = G4_SODIUM_IODIDE
  specific = 4
FEATURE [App::DocumentObjectGroupPython] Na_element016  label="Na_element : 003"  # scripted group (container) (typed FeaturePython)
  n = 2
  ref = Na_element
FEATURE [App::DocumentObjectGroupPython] O_element090  label="O_element : 050"  # scripted group (container) (typed FeaturePython)
  n = 1
  ref = O_element
FEATURE [App::DocumentObjectGroupPython] G4_SODIUM_MONOXIDE  # scripted group (container) (typed FeaturePython)
  Dunit = g/cm3
  Dvalue = 2.27
  Group = -> [Na_element016,O_element090]
  conduct = 2
  density = 1
  expand = 3
  formula = G4_SODIUM_MONOXIDE
  name = G4_SODIUM_MONOXIDE
  specific = 4
FEATURE [App::DocumentObjectGroupPython] Na_element017  label="Na_element : 004"  # scripted group (container) (typed FeaturePython)
  n = 1
  ref = Na_element
FEATURE [App::DocumentObjectGroupPython] N_element040  label="N_element : 018"  # scripted group (container) (typed FeaturePython)
  n = 1
  ref = N_element
FEATURE [App::DocumentObjectGroupPython] O_element091  label="O_element : 051"  # scripted group (container) (typed FeaturePython)
  n = 3
  ref = O_element
FEATURE [App::DocumentObjectGroupPython] G4_SODIUM_NITRATE  # scripted group (container) (typed FeaturePython)
  Dunit = g/cm3
  Dvalue = 2.261
  Group = -> [Na_element017,N_element040,O_element091]
  conduct = 2
  density = 1
  expand = 3
  formula = G4_SODIUM_NITRATE
  name = G4_SODIUM_NITRATE
  specific = 4
FEATURE [App::DocumentObjectGroupPython] C_element105  label="C_element : 059"  # scripted group (container) (typed FeaturePython)
  n = 14
  ref = C_element
FEATURE [App::DocumentObjectGroupPython] H_element096  label="H_element : 053"  # scripted group (container) (typed FeaturePython)
  n = 12
  ref = H_element
FEATURE [App::DocumentObjectGroupPython] G4_STILBENE  # scripted group (container) (typed FeaturePython)
  Dunit = g/cm3
  Dvalue = 0.9707
  Group = -> [C_element105,H_element096]
  conduct = 2
  density = 1
  expand = 3
  formula = G4_STILBENE
  name = G4_STILBENE
  specific = 4
FEATURE [App::DocumentObjectGroupPython] C_element106  label="C_element : 12"  # scripted group (container) (typed FeaturePython)
  n = 12
  ref = C_element
FEATURE [App::DocumentObjectGroupPython] H_element097  label="H_element : 22"  # scripted group (container) (typed FeaturePython)
  n = 22
  ref = H_element
FEATURE [App::DocumentObjectGroupPython] O_element092  label="O_element : 11"  # scripted group (container) (typed FeaturePython)
  n = 11
  ref = O_element
FEATURE [App::DocumentObjectGroupPython] G4_SUCROSE  # scripted group (container) (typed FeaturePython)
  Dunit = g/cm3
  Dvalue = 1.5805
  Group = -> [C_element106,H_element097,O_element092]
  conduct = 2
  density = 1
  expand = 3
  formula = G4_SUCROSE
  name = G4_SUCROSE
  specific = 4
FEATURE [App::DocumentObjectGroupPython] C_element107  label="C_element : 18"  # scripted group (container) (typed FeaturePython)
  n = 18
  ref = C_element
FEATURE [App::DocumentObjectGroupPython] H_element098  label="H_element : 054"  # scripted group (container) (typed FeaturePython)
  n = 14
  ref = H_element
FEATURE [App::DocumentObjectGroupPython] G4_TERPHENYL  # scripted group (container) (typed FeaturePython)
  Dunit = g/cm3
  Dvalue = 1.24
  Group = -> [C_element107,H_element098]
  conduct = 2
  density = 1
  expand = 3
  formula = G4_TERPHENYL
  name = G4_TERPHENYL
  specific = 4
FEATURE [App::DocumentObjectGroupPython] H_element099  label="H_element : 0.146"  # scripted group (container) (typed FeaturePython)
  n = 0.106
FEATURE [App::DocumentObjectGroupPython] C_element108  label="C_element : 0.883"  # scripted group (container) (typed FeaturePython)
  n = 0.099
FEATURE [App::DocumentObjectGroupPython] N_element041  label="N_element : 0.020"  # scripted group (container) (typed FeaturePython)
  n = 0.02
FEATURE [App::DocumentObjectGroupPython] O_element093  label="O_element : 0.766"  # scripted group (container) (typed FeaturePython)
  n = 0.766
FEATURE [App::DocumentObjectGroupPython] Na_element018  label="Na_element : 0.101"  # scripted group (container) (typed FeaturePython)
  n = 0.002
FEATURE [App::DocumentObjectGroupPython] P_element010  label="P_element : 0.108"  # scripted group (container) (typed FeaturePython)
  n = 0.001
FEATURE [App::DocumentObjectGroupPython] S_element021  label="S_element : 0.022"  # scripted group (container) (typed FeaturePython)
  n = 0.002
FEATURE [App::DocumentObjectGroupPython] Cl_element024  label="Cl_element : 0.002"  # scripted group (container) (typed FeaturePython)
  n = 0.002
FEATURE [App::DocumentObjectGroupPython] K_element011  label="K_element : 0.017"  # scripted group (container) (typed FeaturePython)
  n = 0.002
FEATURE [App::DocumentObjectGroupPython] G4_TESTIS_ICRP  # scripted group (container) (typed FeaturePython)
  Dunit = g/cm3
  Dvalue = 1.04
  Group = -> [H_element099,C_element108,N_element041,O_element093,Na_element018,P_element010,S_element021,Cl_element024,K_element011]
  conduct = 2
  density = 1
  expand = 3
  formula = G4_TESTIS_ICRP
  name = G4_TESTIS_ICRP
  specific = 4
FEATURE [App::DocumentObjectGroupPython] C_element109  label="C_element : 060"  # scripted group (container) (typed FeaturePython)
  n = 2
  ref = C_element
FEATURE [App::DocumentObjectGroupPython] Cl_element025  label="Cl_element : 012"  # scripted group (container) (typed FeaturePython)
  n = 4
  ref = Cl_element
FEATURE [App::DocumentObjectGroupPython] G4_TETRACHLOROETHYLENE  # scripted group (container) (typed FeaturePython)
  Dunit = g/cm3
  Dvalue = 1.625
  Group = -> [C_element109,Cl_element025]
  conduct = 2
  density = 1
  expand = 3
  formula = G4_TETRACHLOROETHYLENE
  name = G4_TETRACHLOROETHYLENE
  specific = 4
FEATURE [App::DocumentObjectGroupPython] Tl_element001  label="Tl_element : 1"  # scripted group (container) (typed FeaturePython)
  n = 1
  ref = Tl_element
FEATURE [App::DocumentObjectGroupPython] Cl_element026  label="Cl_element : 013"  # scripted group (container) (typed FeaturePython)
  n = 1
  ref = Cl_element
FEATURE [App::DocumentObjectGroupPython] G4_THALLIUM_CHLORIDE  # scripted group (container) (typed FeaturePython)
  Dunit = g/cm3
  Dvalue = 7.004
  Group = -> [Tl_element001,Cl_element026]
  conduct = 2
  density = 1
  expand = 3
  formula = G4_THALLIUM_CHLORIDE
  name = G4_THALLIUM_CHLORIDE
  specific = 4
FEATURE [App::DocumentObjectGroupPython] H_element100  label="H_element : 0.147"  # scripted group (container) (typed FeaturePython)
  n = 0.105
FEATURE [App::DocumentObjectGroupPython] C_element110  label="C_element : 0.256"  # scripted group (container) (typed FeaturePython)
  n = 0.256
FEATURE [App::DocumentObjectGroupPython] N_element042  label="N_element : 0.760"  # scripted group (container) (typed FeaturePython)
  n = 0.027
FEATURE [App::DocumentObjectGroupPython] O_element094  label="O_element : 0.602"  # scripted group (container) (typed FeaturePython)
  n = 0.602
FEATURE [App::DocumentObjectGroupPython] Na_element019  label="Na_element : 0.102"  # scripted group (container) (typed FeaturePython)
  n = 0.001
FEATURE [App::DocumentObjectGroupPython] P_element011  label="P_element : 0.109"  # scripted group (container) (typed FeaturePython)
  n = 0.002
FEATURE [App::DocumentObjectGroupPython] S_element022  label="S_element : 0.023"  # scripted group (container) (typed FeaturePython)
  n = 0.003
FEATURE [App::DocumentObjectGroupPython] Cl_element027  label="Cl_element : 0.591"  # scripted group (container) (typed FeaturePython)
  n = 0.002
FEATURE [App::DocumentObjectGroupPython] K_element012  label="K_element : 0.018"  # scripted group (container) (typed FeaturePython)
  n = 0.002
FEATURE [App::DocumentObjectGroupPython] G4_TISSUE_SOFT_ICRP  # scripted group (container) (typed FeaturePython)
  Dunit = g/cm3
  Dvalue = 1.03
  Group = -> [H_element100,C_element110,N_element042,O_element094,Na_element019,P_element011,S_element022,Cl_element027,K_element012]
  conduct = 2
  density = 1
  expand = 3
  formula = G4_TISSUE_SOFT_ICRP
  name = G4_TISSUE_SOFT_ICRP
  specific = 4
FEATURE [App::DocumentObjectGroupPython] H_element101  label="H_element : 0.148"  # scripted group (container) (typed FeaturePython)
  n = 0.101
FEATURE [App::DocumentObjectGroupPython] C_element111  label="C_element : 0.111"  # scripted group (container) (typed FeaturePython)
  n = 0.111
FEATURE [App::DocumentObjectGroupPython] N_element043  label="N_element : 0.026"  # scripted group (container) (typed FeaturePython)
  n = 0.026
FEATURE [App::DocumentObjectGroupPython] O_element095  label="O_element : 0.762"  # scripted group (container) (typed FeaturePython)
  n = 0.762
FEATURE [App::DocumentObjectGroupPython] G4_TISSUE_SOFT_ICRU_4  label="G4_TISSUE_SOFT_ICRU-4"  # scripted group (container) (typed FeaturePython)
  Dunit = g/cm3
  Dvalue = 1
  Group = -> [H_element101,C_element111,N_element043,O_element095]
  conduct = 2
  density = 1
  expand = 3
  formula = G4_TISSUE_SOFT_ICRU-4
  name = G4_TISSUE_SOFT_ICRU-4
  specific = 4
FEATURE [App::DocumentObjectGroupPython] H_element102  label="H_element : 0.149"  # scripted group (container) (typed FeaturePython)
  n = 0.101869
FEATURE [App::DocumentObjectGroupPython] C_element112  label="C_element : 0.456"  # scripted group (container) (typed FeaturePython)
  n = 0.456179
FEATURE [App::DocumentObjectGroupPython] N_element044  label="N_element : 0.761"  # scripted group (container) (typed FeaturePython)
  n = 0.035172
FEATURE [App::DocumentObjectGroupPython] O_element096  label="O_element : 0.407"  # scripted group (container) (typed FeaturePython)
  n = 0.40678
FEATURE [App::DocumentObjectGroupPython] G4_TISSUE_METHANE  label="G4_TISSUE-METHANE"  # scripted group (container) (typed FeaturePython)
  Dunit = g/cm3
  Dvalue = 0.00106409
  Group = -> [H_element102,C_element112,N_element044,O_element096]
  conduct = 2
  density = 1
  expand = 3
  formula = G4_TISSUE-METHANE
  name = G4_TISSUE-METHANE
  specific = 4
FEATURE [App::DocumentObjectGroupPython] H_element103  label="H_element : 0.103"  # scripted group (container) (typed FeaturePython)
  n = 0.102672
FEATURE [App::DocumentObjectGroupPython] C_element113  label="C_element : 0.569"  # scripted group (container) (typed FeaturePython)
  n = 0.56894
FEATURE [App::DocumentObjectGroupPython] N_element045  label="N_element : 0.762"  # scripted group (container) (typed FeaturePython)
  n = 0.035022
FEATURE [App::DocumentObjectGroupPython] O_element097  label="O_element : 0.293"  # scripted group (container) (typed FeaturePython)
  n = 0.293366
FEATURE [App::DocumentObjectGroupPython] G4_TISSUE_PROPANE  label="G4_TISSUE-PROPANE"  # scripted group (container) (typed FeaturePython)
  Dunit = g/cm3
  Dvalue = 0.00182628
  Group = -> [H_element103,C_element113,N_element045,O_element097]
  conduct = 2
  density = 1
  expand = 3
  formula = G4_TISSUE-PROPANE
  name = G4_TISSUE-PROPANE
  specific = 4
FEATURE [App::DocumentObjectGroupPython] Ti_element003  label="Ti_element : 1"  # scripted group (container) (typed FeaturePython)
  n = 1
  ref = Ti_element
FEATURE [App::DocumentObjectGroupPython] O_element098  label="O_element : 052"  # scripted group (container) (typed FeaturePython)
  n = 2
  ref = O_element
FEATURE [App::DocumentObjectGroupPython] G4_TITANIUM_DIOXIDE  # scripted group (container) (typed FeaturePython)
  Dunit = g/cm3
  Dvalue = 4.26
  Group = -> [Ti_element003,O_element098]
  conduct = 2
  density = 1
  expand = 3
  formula = G4_TITANIUM_DIOXIDE
  name = G4_TITANIUM_DIOXIDE
  specific = 4
FEATURE [App::DocumentObjectGroupPython] C_element114  label="C_element : 061"  # scripted group (container) (typed FeaturePython)
  n = 7
  ref = C_element
FEATURE [App::DocumentObjectGroupPython] H_element104  label="H_element : 055"  # scripted group (container) (typed FeaturePython)
  n = 8
  ref = H_element
FEATURE [App::DocumentObjectGroupPython] G4_TOLUENE  # scripted group (container) (typed FeaturePython)
  Dunit = g/cm3
  Dvalue = 0.8669
  Group = -> [C_element114,H_element104]
  conduct = 2
  density = 1
  expand = 3
  formula = G4_TOLUENE
  name = G4_TOLUENE
  specific = 4
FEATURE [App::DocumentObjectGroupPython] C_element115  label="C_element : 062"  # scripted group (container) (typed FeaturePython)
  n = 2
  ref = C_element
FEATURE [App::DocumentObjectGroupPython] H_element105  label="H_element : 056"  # scripted group (container) (typed FeaturePython)
  n = 1
  ref = H_element
FEATURE [App::DocumentObjectGroupPython] Cl_element028  label="Cl_element : 014"  # scripted group (container) (typed FeaturePython)
  n = 3
  ref = Cl_element
FEATURE [App::DocumentObjectGroupPython] G4_TRICHLOROETHYLENE  # scripted group (container) (typed FeaturePython)
  Dunit = g/cm3
  Dvalue = 1.46
  Group = -> [C_element115,H_element105,Cl_element028]
  conduct = 2
  density = 1
  expand = 3
  formula = G4_TRICHLOROETHYLENE
  name = G4_TRICHLOROETHYLENE
  specific = 4
FEATURE [App::DocumentObjectGroupPython] C_element116  label="C_element : 063"  # scripted group (container) (typed FeaturePython)
  n = 6
  ref = C_element
FEATURE [App::DocumentObjectGroupPython] H_element106  label="H_element : 15"  # scripted group (container) (typed FeaturePython)
  n = 15
  ref = H_element
FEATURE [App::DocumentObjectGroupPython] O_element099  label="O_element : 053"  # scripted group (container) (typed FeaturePython)
  n = 4
  ref = O_element
FEATURE [App::DocumentObjectGroupPython] P_element012  label="P_element : 1"  # scripted group (container) (typed FeaturePython)
  n = 1
  ref = P_element
FEATURE [App::DocumentObjectGroupPython] G4_TRIETHYL_PHOSPHATE  # scripted group (container) (typed FeaturePython)
  Dunit = g/cm3
  Dvalue = 1.07
  Group = -> [C_element116,H_element106,O_element099,P_element012]
  conduct = 2
  density = 1
  expand = 3
  formula = G4_TRIETHYL_PHOSPHATE
  name = G4_TRIETHYL_PHOSPHATE
  specific = 4
FEATURE [App::DocumentObjectGroupPython] W_element003  label="W_element : 003"  # scripted group (container) (typed FeaturePython)
  n = 1
  ref = W_element
FEATURE [App::DocumentObjectGroupPython] F_element017  label="F_element : 6"  # scripted group (container) (typed FeaturePython)
  n = 6
  ref = F_element
FEATURE [App::DocumentObjectGroupPython] G4_TUNGSTEN_HEXAFLUORIDE  # scripted group (container) (typed FeaturePython)
  Dunit = g/cm3
  Dvalue = 2.4
  Group = -> [W_element003,F_element017]
  conduct = 2
  density = 1
  expand = 3
  formula = G4_TUNGSTEN_HEXAFLUORIDE
  name = G4_TUNGSTEN_HEXAFLUORIDE
  specific = 4
FEATURE [App::DocumentObjectGroupPython] U_element001  label="U_element : 1"  # scripted group (container) (typed FeaturePython)
  n = 1
  ref = U_element
FEATURE [App::DocumentObjectGroupPython] C_element117  label="C_element : 064"  # scripted group (container) (typed FeaturePython)
  n = 2
  ref = C_element
FEATURE [App::DocumentObjectGroupPython] G4_URANIUM_DICARBIDE  # scripted group (container) (typed FeaturePython)
  Dunit = g/cm3
  Dvalue = 11.28
  Group = -> [U_element001,C_element117]
  conduct = 2
  density = 1
  expand = 3
  formula = G4_URANIUM_DICARBIDE
  name = G4_URANIUM_DICARBIDE
  specific = 4
FEATURE [App::DocumentObjectGroupPython] U_element002  label="U_element : 002"  # scripted group (container) (typed FeaturePython)
  n = 1
  ref = U_element
FEATURE [App::DocumentObjectGroupPython] C_element118  label="C_element : 065"  # scripted group (container) (typed FeaturePython)
  n = 1
  ref = C_element
FEATURE [App::DocumentObjectGroupPython] G4_URANIUM_MONOCARBIDE  # scripted group (container) (typed FeaturePython)
  Dunit = g/cm3
  Dvalue = 13.63
  Group = -> [U_element002,C_element118]
  conduct = 2
  density = 1
  expand = 3
  formula = G4_URANIUM_MONOCARBIDE
  name = G4_URANIUM_MONOCARBIDE
  specific = 4
FEATURE [App::DocumentObjectGroupPython] U_element003  label="U_element : 003"  # scripted group (container) (typed FeaturePython)
  n = 1
  ref = U_element
FEATURE [App::DocumentObjectGroupPython] O_element100  label="O_element : 054"  # scripted group (container) (typed FeaturePython)
  n = 2
  ref = O_element
FEATURE [App::DocumentObjectGroupPython] G4_URANIUM_OXIDE  # scripted group (container) (typed FeaturePython)
  Dunit = g/cm3
  Dvalue = 10.96
  Group = -> [U_element003,O_element100]
  conduct = 2
  density = 1
  expand = 3
  formula = G4_URANIUM_OXIDE
  name = G4_URANIUM_OXIDE
  specific = 4
FEATURE [App::DocumentObjectGroupPython] C_element119  label="C_element : 066"  # scripted group (container) (typed FeaturePython)
  n = 1
  ref = C_element
FEATURE [App::DocumentObjectGroupPython] H_element107  label="H_element : 057"  # scripted group (container) (typed FeaturePython)
  n = 4
  ref = H_element
FEATURE [App::DocumentObjectGroupPython] N_element046  label="N_element : 019"  # scripted group (container) (typed FeaturePython)
  n = 2
  ref = N_element
FEATURE [App::DocumentObjectGroupPython] O_element101  label="O_element : 055"  # scripted group (container) (typed FeaturePython)
  n = 1
  ref = O_element
FEATURE [App::DocumentObjectGroupPython] G4_UREA  # scripted group (container) (typed FeaturePython)
  Dunit = g/cm3
  Dvalue = 1.323
  Group = -> [C_element119,H_element107,N_element046,O_element101]
  conduct = 2
  density = 1
  expand = 3
  formula = G4_UREA
  name = G4_UREA
  specific = 4
FEATURE [App::DocumentObjectGroupPython] C_element120  label="C_element : 067"  # scripted group (container) (typed FeaturePython)
  n = 5
  ref = C_element
FEATURE [App::DocumentObjectGroupPython] H_element108  label="H_element : 058"  # scripted group (container) (typed FeaturePython)
  n = 11
  ref = H_element
FEATURE [App::DocumentObjectGroupPython] N_element047  label="N_element : 020"  # scripted group (container) (typed FeaturePython)
  n = 1
  ref = N_element
FEATURE [App::DocumentObjectGroupPython] O_element102  label="O_element : 056"  # scripted group (container) (typed FeaturePython)
  n = 2
  ref = O_element
FEATURE [App::DocumentObjectGroupPython] G4_VALINE  # scripted group (container) (typed FeaturePython)
  Dunit = g/cm3
  Dvalue = 1.23
  Group = -> [C_element120,H_element108,N_element047,O_element102]
  conduct = 2
  density = 1
  expand = 3
  formula = G4_VALINE
  name = G4_VALINE
  specific = 4
FEATURE [App::DocumentObjectGroupPython] H_element109  label="H_element : 0.009"  # scripted group (container) (typed FeaturePython)
  n = 0.009417
FEATURE [App::DocumentObjectGroupPython] C_element121  label="C_element : 0.281"  # scripted group (container) (typed FeaturePython)
  n = 0.280555
FEATURE [App::DocumentObjectGroupPython] F_element018  label="F_element : 0.710"  # scripted group (container) (typed FeaturePython)
  n = 0.710028
FEATURE [App::DocumentObjectGroupPython] G4_VITON  # scripted group (container) (typed FeaturePython)
  Dunit = g/cm3
  Dvalue = 1.8
  Group = -> [H_element109,C_element121,F_element018]
  conduct = 2
  density = 1
  expand = 3
  formula = G4_VITON
  name = G4_VITON
  specific = 4
FEATURE [App::DocumentObjectGroupPython] H_element110  label="H_element : 059"  # scripted group (container) (typed FeaturePython)
  n = 2
  ref = H_element
FEATURE [App::DocumentObjectGroupPython] O_element103  label="O_element : 057"  # scripted group (container) (typed FeaturePython)
  n = 1
  ref = O_element
FEATURE [App::DocumentObjectGroupPython] G4_WATER  # scripted group (container) (typed FeaturePython)
  Dunit = g/cm3
  Dvalue = 1
  Group = -> [H_element110,O_element103]
  conduct = 2
  density = 1
  expand = 3
  formula = G4_WATER
  name = G4_WATER
  specific = 4
FEATURE [App::DocumentObjectGroupPython] H_element111  label="H_element : 060"  # scripted group (container) (typed FeaturePython)
  n = 2
  ref = H_element
FEATURE [App::DocumentObjectGroupPython] O_element104  label="O_element : 058"  # scripted group (container) (typed FeaturePython)
  n = 1
  ref = O_element
FEATURE [App::DocumentObjectGroupPython] G4_WATER_VAPOR  # scripted group (container) (typed FeaturePython)
  Dunit = g/cm3
  Dvalue = 0.000756182
  Group = -> [H_element111,O_element104]
  conduct = 2
  density = 1
  expand = 3
  formula = G4_WATER_VAPOR
  name = G4_WATER_VAPOR
  specific = 4
FEATURE [App::DocumentObjectGroupPython] C_element122  label="C_element : 068"  # scripted group (container) (typed FeaturePython)
  n = 8
  ref = C_element
FEATURE [App::DocumentObjectGroupPython] H_element112  label="H_element : 061"  # scripted group (container) (typed FeaturePython)
  n = 10
  ref = H_element
FEATURE [App::DocumentObjectGroupPython] G4_XYLENE  # scripted group (container) (typed FeaturePython)
  Dunit = g/cm3
  Dvalue = 0.87
  Group = -> [C_element122,H_element112]
  conduct = 2
  density = 1
  expand = 3
  formula = G4_XYLENE
  name = G4_XYLENE
  specific = 4
FEATURE [App::DocumentObjectGroupPython] C_element123  label="C_element : 069"  # scripted group (container) (typed FeaturePython)
  n = 1
  ref = C_element
FEATURE [App::DocumentObjectGroupPython] G4_GRAPHITE  # scripted group (container) (typed FeaturePython)
  Dunit = g/cm3
  Dvalue = 2.21
  Group = -> [C_element123]
  conduct = 2
  density = 1
  expand = 3
  formula = G4_GRAPHITE
  name = G4_GRAPHITE
  specific = 4
FEATURE [App::DocumentObjectGroupPython] NIST  # scripted group (container) (typed FeaturePython)
  Group = -> [G4_A_150_TISSUE,G4_ACETONE,G4_ACETYLENE,G4_ADENINE,G4_ADIPOSE_TISSUE_ICRP,G4_AIR,G4_ALANINE,G4_ALUMINUM_OXIDE,G4_AMBER,G4_AMMONIA,G4_ANILINE,G4_ANTHRACENE,G4_B_100_BONE,G4_BAKELITE,G4_BARIUM_FLUORIDE,G4_BARIUM_SULFATE,G4_BENZENE,G4_BERYLLIUM_OXIDE,G4_BGO,G4_BLOOD_ICRP,G4_BONE_COMPACT_ICRU,G4_BONE_CORTICAL_ICRP,G4_BORON_CARBIDE,G4_BORON_OXIDE,G4_BRAIN_ICRP,G4_BUTANE,G4_N_BUTYL_ALCOHOL,G4_C_552,+152 more]
FEATURE [App::DocumentObjectGroupPython] H_element113  label="H_element : 062"  # scripted group (container) (typed FeaturePython)
  n = 1
  ref = H_element
FEATURE [App::DocumentObjectGroupPython] G4_H  # scripted group (container) (typed FeaturePython)
  Dunit = g/cm3
  Dvalue = 8.3748e-05
  Group = -> [H_element113]
  conduct = 2
  density = 1
  expand = 3
  formula = H
  name = G4_H
  specific = 4
FEATURE [App::DocumentObjectGroupPython] He_element001  label="He_element : 1"  # scripted group (container) (typed FeaturePython)
  n = 1
  ref = He_element
FEATURE [App::DocumentObjectGroupPython] G4_He  # scripted group (container) (typed FeaturePython)
  Dunit = g/cm3
  Dvalue = 0.000166322
  Group = -> [He_element001]
  conduct = 2
  density = 1
  expand = 3
  formula = He
  name = G4_He
  specific = 4
FEATURE [App::DocumentObjectGroupPython] Li_element008  label="Li_element : 008"  # scripted group (container) (typed FeaturePython)
  n = 1
  ref = Li_element
FEATURE [App::DocumentObjectGroupPython] G4_Li  # scripted group (container) (typed FeaturePython)
  Dunit = g/cm3
  Dvalue = 0.534
  Group = -> [Li_element008]
  conduct = 2
  density = 1
  expand = 3
  formula = Li
  name = G4_Li
  specific = 4
FEATURE [App::DocumentObjectGroupPython] Be_element002  label="Be_element : 002"  # scripted group (container) (typed FeaturePython)
  n = 1
  ref = Be_element
FEATURE [App::DocumentObjectGroupPython] G4_Be  # scripted group (container) (typed FeaturePython)
  Dunit = g/cm3
  Dvalue = 1.848
  Group = -> [Be_element002]
  conduct = 2
  density = 1
  expand = 3
  formula = Be
  name = G4_Be
  specific = 4
FEATURE [App::DocumentObjectGroupPython] B_element007  label="B_element : 007"  # scripted group (container) (typed FeaturePython)
  n = 1
  ref = B_element
FEATURE [App::DocumentObjectGroupPython] G4_B  # scripted group (container) (typed FeaturePython)
  Dunit = g/cm3
  Dvalue = 2.37
  Group = -> [B_element007]
  conduct = 2
  density = 1
  expand = 3
  formula = B
  name = G4_B
  specific = 4
FEATURE [App::DocumentObjectGroupPython] C_element124  label="C_element : 070"  # scripted group (container) (typed FeaturePython)
  n = 1
  ref = C_element
FEATURE [App::DocumentObjectGroupPython] G4_C  # scripted group (container) (typed FeaturePython)
  Dunit = g/cm3
  Dvalue = 2
  Group = -> [C_element124]
  conduct = 2
  density = 1
  expand = 3
  formula = C
  name = G4_C
  specific = 4
FEATURE [App::DocumentObjectGroupPython] N_element048  label="N_element : 021"  # scripted group (container) (typed FeaturePython)
  n = 1
  ref = N_element
FEATURE [App::DocumentObjectGroupPython] G4_N  # scripted group (container) (typed FeaturePython)
  Dunit = g/cm3
  Dvalue = 0.0011652
  Group = -> [N_element048]
  conduct = 2
  density = 1
  expand = 3
  formula = N
  name = G4_N
  specific = 4
FEATURE [App::DocumentObjectGroupPython] O_element105  label="O_element : 059"  # scripted group (container) (typed FeaturePython)
  n = 1
  ref = O_element
FEATURE [App::DocumentObjectGroupPython] G4_O  # scripted group (container) (typed FeaturePython)
  Dunit = g/cm3
  Dvalue = 0.00133151
  Group = -> [O_element105]
  conduct = 2
  density = 1
  expand = 3
  formula = O
  name = G4_O
  specific = 4
FEATURE [App::DocumentObjectGroupPython] F_element019  label="F_element : 008"  # scripted group (container) (typed FeaturePython)
  n = 1
  ref = F_element
FEATURE [App::DocumentObjectGroupPython] G4_F  # scripted group (container) (typed FeaturePython)
  Dunit = g/cm3
  Dvalue = 0.00158029
  Group = -> [F_element019]
  conduct = 2
  density = 1
  expand = 3
  formula = F
  name = G4_F
  specific = 4
FEATURE [App::DocumentObjectGroupPython] Ne_element001  label="Ne_element : 1"  # scripted group (container) (typed FeaturePython)
  n = 1
  ref = Ne_element
FEATURE [App::DocumentObjectGroupPython] G4_Ne  # scripted group (container) (typed FeaturePython)
  Dunit = g/cm3
  Dvalue = 0.000838505
  Group = -> [Ne_element001]
  conduct = 2
  density = 1
  expand = 3
  formula = Ne
  name = G4_Ne
  specific = 4
FEATURE [App::DocumentObjectGroupPython] Na_element020  label="Na_element : 005"  # scripted group (container) (typed FeaturePython)
  n = 1
  ref = Na_element
FEATURE [App::DocumentObjectGroupPython] G4_Na  # scripted group (container) (typed FeaturePython)
  Dunit = g/cm3
  Dvalue = 0.971
  Group = -> [Na_element020]
  conduct = 2
  density = 1
  expand = 3
  formula = Na
  name = G4_Na
  specific = 4
FEATURE [App::DocumentObjectGroupPython] Mg_element011  label="Mg_element : 005"  # scripted group (container) (typed FeaturePython)
  n = 1
  ref = Mg_element
FEATURE [App::DocumentObjectGroupPython] G4_Mg  # scripted group (container) (typed FeaturePython)
  Dunit = g/cm3
  Dvalue = 1.74
  Group = -> [Mg_element011]
  conduct = 2
  density = 1
  expand = 3
  formula = Mg
  name = G4_Mg
  specific = 4
FEATURE [App::DocumentObjectGroupPython] Al_element004  label="Al_element : 1"  # scripted group (container) (typed FeaturePython)
  n = 1
  ref = Al_element
FEATURE [App::DocumentObjectGroupPython] G4_Al  # scripted group (container) (typed FeaturePython)
  Dunit = g/cm3
  Dvalue = 2.699
  Group = -> [Al_element004]
  conduct = 2
  density = 1
  expand = 3
  formula = Al
  name = G4_Al
  specific = 4
FEATURE [App::DocumentObjectGroupPython] Si_element007  label="Si_element : 002"  # scripted group (container) (typed FeaturePython)
  n = 1
  ref = Si_element
FEATURE [App::DocumentObjectGroupPython] G4_Si  # scripted group (container) (typed FeaturePython)
  Dunit = g/cm3
  Dvalue = 2.33
  Group = -> [Si_element007]
  conduct = 2
  density = 1
  expand = 3
  formula = Si
  name = G4_Si
  specific = 4
FEATURE [App::DocumentObjectGroupPython] P_element013  label="P_element : 002"  # scripted group (container) (typed FeaturePython)
  n = 1
  ref = P_element
FEATURE [App::DocumentObjectGroupPython] G4_P  # scripted group (container) (typed FeaturePython)
  Dunit = g/cm3
  Dvalue = 2.2
  Group = -> [P_element013]
  conduct = 2
  density = 1
  expand = 3
  formula = P
  name = G4_P
  specific = 4
FEATURE [App::DocumentObjectGroupPython] S_element023  label="S_element : 007"  # scripted group (container) (typed FeaturePython)
  n = 1
  ref = S_element
FEATURE [App::DocumentObjectGroupPython] G4_S  # scripted group (container) (typed FeaturePython)
  Dunit = g/cm3
  Dvalue = 2
  Group = -> [S_element023]
  conduct = 2
  density = 1
  expand = 3
  formula = S
  name = G4_S
  specific = 4
FEATURE [App::DocumentObjectGroupPython] Cl_element029  label="Cl_element : 015"  # scripted group (container) (typed FeaturePython)
  n = 1
  ref = Cl_element
FEATURE [App::DocumentObjectGroupPython] G4_Cl  # scripted group (container) (typed FeaturePython)
  Dunit = g/cm3
  Dvalue = 0.00299473
  Group = -> [Cl_element029]
  conduct = 2
  density = 1
  expand = 3
  formula = Cl
  name = G4_Cl
  specific = 4
FEATURE [App::DocumentObjectGroupPython] Ar_element002  label="Ar_element : 1"  # scripted group (container) (typed FeaturePython)
  n = 1
  ref = Ar_element
FEATURE [App::DocumentObjectGroupPython] G4_Ar  # scripted group (container) (typed FeaturePython)
  Dunit = g/cm3
  Dvalue = 0.00166201
  Group = -> [Ar_element002]
  conduct = 2
  density = 1
  expand = 3
  formula = Ar
  name = G4_Ar
  specific = 4
FEATURE [App::DocumentObjectGroupPython] K_element013  label="K_element : 003"  # scripted group (container) (typed FeaturePython)
  n = 1
  ref = K_element
FEATURE [App::DocumentObjectGroupPython] G4_K  # scripted group (container) (typed FeaturePython)
  Dunit = g/cm3
  Dvalue = 0.862
  Group = -> [K_element013]
  conduct = 2
  density = 1
  expand = 3
  formula = K
  name = G4_K
  specific = 4
FEATURE [App::DocumentObjectGroupPython] Ca_element014  label="Ca_element : 007"  # scripted group (container) (typed FeaturePython)
  n = 1
  ref = Ca_element
FEATURE [App::DocumentObjectGroupPython] G4_Ca  # scripted group (container) (typed FeaturePython)
  Dunit = g/cm3
  Dvalue = 1.55
  Group = -> [Ca_element014]
  conduct = 2
  density = 1
  expand = 3
  formula = Ca
  name = G4_Ca
  specific = 4
FEATURE [App::DocumentObjectGroupPython] Sc_element001  label="Sc_element : 1"  # scripted group (container) (typed FeaturePython)
  n = 1
  ref = Sc_element
FEATURE [App::DocumentObjectGroupPython] G4_Sc  # scripted group (container) (typed FeaturePython)
  Dunit = g/cm3
  Dvalue = 2.989
  Group = -> [Sc_element001]
  conduct = 2
  density = 1
  expand = 3
  formula = Sc
  name = G4_Sc
  specific = 4
FEATURE [App::DocumentObjectGroupPython] Ti_element004  label="Ti_element : 002"  # scripted group (container) (typed FeaturePython)
  n = 1
  ref = Ti_element
FEATURE [App::DocumentObjectGroupPython] G4_Ti  # scripted group (container) (typed FeaturePython)
  Dunit = g/cm3
  Dvalue = 4.54
  Group = -> [Ti_element004]
  conduct = 2
  density = 1
  expand = 3
  formula = Ti
  name = G4_Ti
  specific = 4
FEATURE [App::DocumentObjectGroupPython] V_element001  label="V_element : 1"  # scripted group (container) (typed FeaturePython)
  n = 1
  ref = V_element
FEATURE [App::DocumentObjectGroupPython] G4_V  # scripted group (container) (typed FeaturePython)
  Dunit = g/cm3
  Dvalue = 6.11
  Group = -> [V_element001]
  conduct = 2
  density = 1
  expand = 3
  formula = V
  name = G4_V
  specific = 4
FEATURE [App::DocumentObjectGroupPython] Cr_element001  label="Cr_element : 1"  # scripted group (container) (typed FeaturePython)
  n = 1
  ref = Cr_element
FEATURE [App::DocumentObjectGroupPython] G4_Cr  # scripted group (container) (typed FeaturePython)
  Dunit = g/cm3
  Dvalue = 7.18
  Group = -> [Cr_element001]
  conduct = 2
  density = 1
  expand = 3
  formula = Cr
  name = G4_Cr
  specific = 4
FEATURE [App::DocumentObjectGroupPython] Mn_element001  label="Mn_element : 1"  # scripted group (container) (typed FeaturePython)
  n = 1
  ref = Mn_element
FEATURE [App::DocumentObjectGroupPython] G4_Mn  # scripted group (container) (typed FeaturePython)
  Dunit = g/cm3
  Dvalue = 7.44
  Group = -> [Mn_element001]
  conduct = 2
  density = 1
  expand = 3
  formula = Mn
  name = G4_Mn
  specific = 4
FEATURE [App::DocumentObjectGroupPython] Fe_element007  label="Fe_element : 004"  # scripted group (container) (typed FeaturePython)
  n = 1
  ref = Fe_element
FEATURE [App::DocumentObjectGroupPython] G4_Fe  # scripted group (container) (typed FeaturePython)
  Dunit = g/cm3
  Dvalue = 7.874
  Group = -> [Fe_element007]
  conduct = 2
  density = 1
  expand = 3
  formula = Fe
  name = G4_Fe
  specific = 4
FEATURE [App::DocumentObjectGroupPython] Co_element001  label="Co_element : 1"  # scripted group (container) (typed FeaturePython)
  n = 1
  ref = Co_element
FEATURE [App::DocumentObjectGroupPython] G4_Co  # scripted group (container) (typed FeaturePython)
  Dunit = g/cm3
  Dvalue = 8.9
  Group = -> [Co_element001]
  conduct = 2
  density = 1
  expand = 3
  formula = Co
  name = G4_Co
  specific = 4
FEATURE [App::DocumentObjectGroupPython] Ni_element001  label="Ni_element : 1"  # scripted group (container) (typed FeaturePython)
  n = 1
  ref = Ni_element
FEATURE [App::DocumentObjectGroupPython] G4_Ni  # scripted group (container) (typed FeaturePython)
  Dunit = g/cm3
  Dvalue = 8.902
  Group = -> [Ni_element001]
  conduct = 2
  density = 1
  expand = 3
  formula = Ni
  name = G4_Ni
  specific = 4
FEATURE [App::DocumentObjectGroupPython] Cu_element001  label="Cu_element : 1"  # scripted group (container) (typed FeaturePython)
  n = 1
  ref = Cu_element
FEATURE [App::DocumentObjectGroupPython] G4_Cu  # scripted group (container) (typed FeaturePython)
  Dunit = g/cm3
  Dvalue = 8.96
  Group = -> [Cu_element001]
  conduct = 2
  density = 1
  expand = 3
  formula = Cu
  name = G4_Cu
  specific = 4
FEATURE [App::DocumentObjectGroupPython] Zn_element001  label="Zn_element : 1"  # scripted group (container) (typed FeaturePython)
  n = 1
  ref = Zn_element
FEATURE [App::DocumentObjectGroupPython] G4_Zn  # scripted group (container) (typed FeaturePython)
  Dunit = g/cm3
  Dvalue = 7.133
  Group = -> [Zn_element001]
  conduct = 2
  density = 1
  expand = 3
  formula = Zn
  name = G4_Zn
  specific = 4
FEATURE [App::DocumentObjectGroupPython] Ga_element002  label="Ga_element : 002"  # scripted group (container) (typed FeaturePython)
  n = 1
  ref = Ga_element
FEATURE [App::DocumentObjectGroupPython] G4_Ga  # scripted group (container) (typed FeaturePython)
  Dunit = g/cm3
  Dvalue = 5.904
  Group = -> [Ga_element002]
  conduct = 2
  density = 1
  expand = 3
  formula = Ga
  name = G4_Ga
  specific = 4
FEATURE [App::DocumentObjectGroupPython] Ge_element002  label="Ge_element : 1"  # scripted group (container) (typed FeaturePython)
  n = 1
  ref = Ge_element
FEATURE [App::DocumentObjectGroupPython] G4_Ge  # scripted group (container) (typed FeaturePython)
  Dunit = g/cm3
  Dvalue = 5.323
  Group = -> [Ge_element002]
  conduct = 2
  density = 1
  expand = 3
  formula = Ge
  name = G4_Ge
  specific = 4
FEATURE [App::DocumentObjectGroupPython] As_element003  label="As_element : 002"  # scripted group (container) (typed FeaturePython)
  n = 1
  ref = As_element
FEATURE [App::DocumentObjectGroupPython] G4_As  # scripted group (container) (typed FeaturePython)
  Dunit = g/cm3
  Dvalue = 5.73
  Group = -> [As_element003]
  conduct = 2
  density = 1
  expand = 3
  formula = As
  name = G4_As
  specific = 4
FEATURE [App::DocumentObjectGroupPython] Se_element001  label="Se_element : 1"  # scripted group (container) (typed FeaturePython)
  n = 1
  ref = Se_element
FEATURE [App::DocumentObjectGroupPython] G4_Se  # scripted group (container) (typed FeaturePython)
  Dunit = g/cm3
  Dvalue = 4.5
  Group = -> [Se_element001]
  conduct = 2
  density = 1
  expand = 3
  formula = Se
  name = G4_Se
  specific = 4
FEATURE [App::DocumentObjectGroupPython] Br_element007  label="Br_element : 004"  # scripted group (container) (typed FeaturePython)
  n = 1
  ref = Br_element
FEATURE [App::DocumentObjectGroupPython] G4_Br  # scripted group (container) (typed FeaturePython)
  Dunit = g/cm3
  Dvalue = 0.0070721
  Group = -> [Br_element007]
  conduct = 2
  density = 1
  expand = 3
  formula = Br
  name = G4_Br
  specific = 4
FEATURE [App::DocumentObjectGroupPython] Kr_element001  label="Kr_element : 1"  # scripted group (container) (typed FeaturePython)
  n = 1
  ref = Kr_element
FEATURE [App::DocumentObjectGroupPython] G4_Kr  # scripted group (container) (typed FeaturePython)
  Dunit = g/cm3
  Dvalue = 0.00347832
  Group = -> [Kr_element001]
  conduct = 2
  density = 1
  expand = 3
  formula = Kr
  name = G4_Kr
  specific = 4
FEATURE [App::DocumentObjectGroupPython] Rb_element001  label="Rb_element : 1"  # scripted group (container) (typed FeaturePython)
  n = 1
  ref = Rb_element
FEATURE [App::DocumentObjectGroupPython] G4_Rb  # scripted group (container) (typed FeaturePython)
  Dunit = g/cm3
  Dvalue = 1.532
  Group = -> [Rb_element001]
  conduct = 2
  density = 1
  expand = 3
  formula = Rb
  name = G4_Rb
  specific = 4
FEATURE [App::DocumentObjectGroupPython] Sr_element001  label="Sr_element : 1"  # scripted group (container) (typed FeaturePython)
  n = 1
  ref = Sr_element
FEATURE [App::DocumentObjectGroupPython] G4_Sr  # scripted group (container) (typed FeaturePython)
  Dunit = g/cm3
  Dvalue = 2.54
  Group = -> [Sr_element001]
  conduct = 2
  density = 1
  expand = 3
  formula = Sr
  name = G4_Sr
  specific = 4
FEATURE [App::DocumentObjectGroupPython] Y_element001  label="Y_element : 1"  # scripted group (container) (typed FeaturePython)
  n = 1
  ref = Y_element
FEATURE [App::DocumentObjectGroupPython] G4_Y  # scripted group (container) (typed FeaturePython)
  Dunit = g/cm3
  Dvalue = 4.469
  Group = -> [Y_element001]
  conduct = 2
  density = 1
  expand = 3
  formula = Y
  name = G4_Y
  specific = 4
FEATURE [App::DocumentObjectGroupPython] Zr_element001  label="Zr_element : 1"  # scripted group (container) (typed FeaturePython)
  n = 1
  ref = Zr_element
FEATURE [App::DocumentObjectGroupPython] G4_Zr  # scripted group (container) (typed FeaturePython)
  Dunit = g/cm3
  Dvalue = 6.506
  Group = -> [Zr_element001]
  conduct = 2
  density = 1
  expand = 3
  formula = Zr
  name = G4_Zr
  specific = 4
FEATURE [App::DocumentObjectGroupPython] Nb_element001  label="Nb_element : 1"  # scripted group (container) (typed FeaturePython)
  n = 1
  ref = Nb_element
FEATURE [App::DocumentObjectGroupPython] G4_Nb  # scripted group (container) (typed FeaturePython)
  Dunit = g/cm3
  Dvalue = 8.57
  Group = -> [Nb_element001]
  conduct = 2
  density = 1
  expand = 3
  formula = Nb
  name = G4_Nb
  specific = 4
FEATURE [App::DocumentObjectGroupPython] Mo_element001  label="Mo_element : 1"  # scripted group (container) (typed FeaturePython)
  n = 1
  ref = Mo_element
FEATURE [App::DocumentObjectGroupPython] G4_Mo  # scripted group (container) (typed FeaturePython)
  Dunit = g/cm3
  Dvalue = 10.22
  Group = -> [Mo_element001]
  conduct = 2
  density = 1
  expand = 3
  formula = Mo
  name = G4_Mo
  specific = 4
FEATURE [App::DocumentObjectGroupPython] Tc_element001  label="Tc_element : 1"  # scripted group (container) (typed FeaturePython)
  n = 1
  ref = Tc_element
FEATURE [App::DocumentObjectGroupPython] G4_Tc  # scripted group (container) (typed FeaturePython)
  Dunit = g/cm3
  Dvalue = 11.5
  Group = -> [Tc_element001]
  conduct = 2
  density = 1
  expand = 3
  formula = Tc
  name = G4_Tc
  specific = 4
FEATURE [App::DocumentObjectGroupPython] Ru_element001  label="Ru_element : 1"  # scripted group (container) (typed FeaturePython)
  n = 1
  ref = Ru_element
FEATURE [App::DocumentObjectGroupPython] G4_Ru  # scripted group (container) (typed FeaturePython)
  Dunit = g/cm3
  Dvalue = 12.41
  Group = -> [Ru_element001]
  conduct = 2
  density = 1
  expand = 3
  formula = Ru
  name = G4_Ru
  specific = 4
FEATURE [App::DocumentObjectGroupPython] Rh_element001  label="Rh_element : 1"  # scripted group (container) (typed FeaturePython)
  n = 1
  ref = Rh_element
FEATURE [App::DocumentObjectGroupPython] G4_Rh  # scripted group (container) (typed FeaturePython)
  Dunit = g/cm3
  Dvalue = 12.41
  Group = -> [Rh_element001]
  conduct = 2
  density = 1
  expand = 3
  formula = Rh
  name = G4_Rh
  specific = 4
FEATURE [App::DocumentObjectGroupPython] Pd_element001  label="Pd_element : 1"  # scripted group (container) (typed FeaturePython)
  n = 1
  ref = Pd_element
FEATURE [App::DocumentObjectGroupPython] G4_Pd  # scripted group (container) (typed FeaturePython)
  Dunit = g/cm3
  Dvalue = 12.02
  Group = -> [Pd_element001]
  conduct = 2
  density = 1
  expand = 3
  formula = Pd
  name = G4_Pd
  specific = 4
FEATURE [App::DocumentObjectGroupPython] Ag_element006  label="Ag_element : 004"  # scripted group (container) (typed FeaturePython)
  n = 1
  ref = Ag_element
FEATURE [App::DocumentObjectGroupPython] G4_Ag  # scripted group (container) (typed FeaturePython)
  Dunit = g/cm3
  Dvalue = 10.5
  Group = -> [Ag_element006]
  conduct = 2
  density = 1
  expand = 3
  formula = Ag
  name = G4_Ag
  specific = 4
FEATURE [App::DocumentObjectGroupPython] Cd_element003  label="Cd_element : 003"  # scripted group (container) (typed FeaturePython)
  n = 1
  ref = Cd_element
FEATURE [App::DocumentObjectGroupPython] G4_Cd  # scripted group (container) (typed FeaturePython)
  Dunit = g/cm3
  Dvalue = 8.65
  Group = -> [Cd_element003]
  conduct = 2
  density = 1
  expand = 3
  formula = Cd
  name = G4_Cd
  specific = 4
FEATURE [App::DocumentObjectGroupPython] In_element001  label="In_element : 1"  # scripted group (container) (typed FeaturePython)
  n = 1
  ref = In_element
FEATURE [App::DocumentObjectGroupPython] G4_In  # scripted group (container) (typed FeaturePython)
  Dunit = g/cm3
  Dvalue = 7.31
  Group = -> [In_element001]
  conduct = 2
  density = 1
  expand = 3
  formula = In
  name = G4_In
  specific = 4
FEATURE [App::DocumentObjectGroupPython] Sn_element001  label="Sn_element : 1"  # scripted group (container) (typed FeaturePython)
  n = 1
  ref = Sn_element
FEATURE [App::DocumentObjectGroupPython] G4_Sn  # scripted group (container) (typed FeaturePython)
  Dunit = g/cm3
  Dvalue = 7.31
  Group = -> [Sn_element001]
  conduct = 2
  density = 1
  expand = 3
  formula = Sn
  name = G4_Sn
  specific = 4
FEATURE [App::DocumentObjectGroupPython] Sb_element001  label="Sb_element : 1"  # scripted group (container) (typed FeaturePython)
  n = 1
  ref = Sb_element
FEATURE [App::DocumentObjectGroupPython] G4_Sb  # scripted group (container) (typed FeaturePython)
  Dunit = g/cm3
  Dvalue = 6.691
  Group = -> [Sb_element001]
  conduct = 2
  density = 1
  expand = 3
  formula = Sb
  name = G4_Sb
  specific = 4
FEATURE [App::DocumentObjectGroupPython] Te_element002  label="Te_element : 002"  # scripted group (container) (typed FeaturePython)
  n = 1
  ref = Te_element
FEATURE [App::DocumentObjectGroupPython] G4_Te  # scripted group (container) (typed FeaturePython)
  Dunit = g/cm3
  Dvalue = 6.24
  Group = -> [Te_element002]
  conduct = 2
  density = 1
  expand = 3
  formula = Te
  name = G4_Te
  specific = 4
FEATURE [App::DocumentObjectGroupPython] I_element010  label="I_element : 006"  # scripted group (container) (typed FeaturePython)
  n = 1
  ref = I_element
FEATURE [App::DocumentObjectGroupPython] G4_I  # scripted group (container) (typed FeaturePython)
  Dunit = g/cm3
  Dvalue = 4.93
  Group = -> [I_element010]
  conduct = 2
  density = 1
  expand = 3
  formula = I
  name = G4_I
  specific = 4
FEATURE [App::DocumentObjectGroupPython] Xe_element001  label="Xe_element : 1"  # scripted group (container) (typed FeaturePython)
  n = 1
  ref = Xe_element
FEATURE [App::DocumentObjectGroupPython] G4_Xe  # scripted group (container) (typed FeaturePython)
  Dunit = g/cm3
  Dvalue = 0.00548536
  Group = -> [Xe_element001]
  conduct = 2
  density = 1
  expand = 3
  formula = Xe
  name = G4_Xe
  specific = 4
FEATURE [App::DocumentObjectGroupPython] Cs_element003  label="Cs_element : 003"  # scripted group (container) (typed FeaturePython)
  n = 1
  ref = Cs_element
FEATURE [App::DocumentObjectGroupPython] G4_Cs  # scripted group (container) (typed FeaturePython)
  Dunit = g/cm3
  Dvalue = 1.873
  Group = -> [Cs_element003]
  conduct = 2
  density = 1
  expand = 3
  formula = Cs
  name = G4_Cs
  specific = 4
FEATURE [App::DocumentObjectGroupPython] Ba_element003  label="Ba_element : 003"  # scripted group (container) (typed FeaturePython)
  n = 1
  ref = Ba_element
FEATURE [App::DocumentObjectGroupPython] G4_Ba  # scripted group (container) (typed FeaturePython)
  Dunit = g/cm3
  Dvalue = 3.5
  Group = -> [Ba_element003]
  conduct = 2
  density = 1
  expand = 3
  formula = Ba
  name = G4_Ba
  specific = 4
FEATURE [App::DocumentObjectGroupPython] La_element003  label="La_element : 003"  # scripted group (container) (typed FeaturePython)
  n = 1
  ref = La_element
FEATURE [App::DocumentObjectGroupPython] G4_La  # scripted group (container) (typed FeaturePython)
  Dunit = g/cm3
  Dvalue = 6.154
  Group = -> [La_element003]
  conduct = 2
  density = 1
  expand = 3
  formula = La
  name = G4_La
  specific = 4
FEATURE [App::DocumentObjectGroupPython] Ce_element002  label="Ce_element : 1"  # scripted group (container) (typed FeaturePython)
  n = 1
  ref = Ce_element
FEATURE [App::DocumentObjectGroupPython] G4_Ce  # scripted group (container) (typed FeaturePython)
  Dunit = g/cm3
  Dvalue = 6.657
  Group = -> [Ce_element002]
  conduct = 2
  density = 1
  expand = 3
  formula = Ce
  name = G4_Ce
  specific = 4
FEATURE [App::DocumentObjectGroupPython] Pr_element001  label="Pr_element : 1"  # scripted group (container) (typed FeaturePython)
  n = 1
  ref = Pr_element
FEATURE [App::DocumentObjectGroupPython] G4_Pr  # scripted group (container) (typed FeaturePython)
  Dunit = g/cm3
  Dvalue = 6.71
  Group = -> [Pr_element001]
  conduct = 2
  density = 1
  expand = 3
  formula = Pr
  name = G4_Pr
  specific = 4
FEATURE [App::DocumentObjectGroupPython] Nd_element001  label="Nd_element : 1"  # scripted group (container) (typed FeaturePython)
  n = 1
  ref = Nd_element
FEATURE [App::DocumentObjectGroupPython] G4_Nd  # scripted group (container) (typed FeaturePython)
  Dunit = g/cm3
  Dvalue = 6.9
  Group = -> [Nd_element001]
  conduct = 2
  density = 1
  expand = 3
  formula = Nd
  name = G4_Nd
  specific = 4
FEATURE [App::DocumentObjectGroupPython] Pm_element001  label="Pm_element : 1"  # scripted group (container) (typed FeaturePython)
  n = 1
  ref = Pm_element
FEATURE [App::DocumentObjectGroupPython] G4_Pm  # scripted group (container) (typed FeaturePython)
  Dunit = g/cm3
  Dvalue = 7.22
  Group = -> [Pm_element001]
  conduct = 2
  density = 1
  expand = 3
  formula = Pm
  name = G4_Pm
  specific = 4
FEATURE [App::DocumentObjectGroupPython] Sm_element001  label="Sm_element : 1"  # scripted group (container) (typed FeaturePython)
  n = 1
  ref = Sm_element
FEATURE [App::DocumentObjectGroupPython] G4_Sm  # scripted group (container) (typed FeaturePython)
  Dunit = g/cm3
  Dvalue = 7.46
  Group = -> [Sm_element001]
  conduct = 2
  density = 1
  expand = 3
  formula = Sm
  name = G4_Sm
  specific = 4
FEATURE [App::DocumentObjectGroupPython] Eu_element001  label="Eu_element : 1"  # scripted group (container) (typed FeaturePython)
  n = 1
  ref = Eu_element
FEATURE [App::DocumentObjectGroupPython] G4_Eu  # scripted group (container) (typed FeaturePython)
  Dunit = g/cm3
  Dvalue = 5.243
  Group = -> [Eu_element001]
  conduct = 2
  density = 1
  expand = 3
  formula = Eu
  name = G4_Eu
  specific = 4
FEATURE [App::DocumentObjectGroupPython] Gd_element002  label="Gd_element : 1"  # scripted group (container) (typed FeaturePython)
  n = 1
  ref = Gd_element
FEATURE [App::DocumentObjectGroupPython] G4_Gd  # scripted group (container) (typed FeaturePython)
  Dunit = g/cm3
  Dvalue = 7.9004
  Group = -> [Gd_element002]
  conduct = 2
  density = 1
  expand = 3
  formula = Gd
  name = G4_Gd
  specific = 4
FEATURE [App::DocumentObjectGroupPython] Tb_element001  label="Tb_element : 1"  # scripted group (container) (typed FeaturePython)
  n = 1
  ref = Tb_element
FEATURE [App::DocumentObjectGroupPython] G4_Tb  # scripted group (container) (typed FeaturePython)
  Dunit = g/cm3
  Dvalue = 8.229
  Group = -> [Tb_element001]
  conduct = 2
  density = 1
  expand = 3
  formula = Tb
  name = G4_Tb
  specific = 4
FEATURE [App::DocumentObjectGroupPython] Dy_element001  label="Dy_element : 1"  # scripted group (container) (typed FeaturePython)
  n = 1
  ref = Dy_element
FEATURE [App::DocumentObjectGroupPython] G4_Dy  # scripted group (container) (typed FeaturePython)
  Dunit = g/cm3
  Dvalue = 8.55
  Group = -> [Dy_element001]
  conduct = 2
  density = 1
  expand = 3
  formula = Dy
  name = G4_Dy
  specific = 4
FEATURE [App::DocumentObjectGroupPython] Ho_element001  label="Ho_element : 1"  # scripted group (container) (typed FeaturePython)
  n = 1
  ref = Ho_element
FEATURE [App::DocumentObjectGroupPython] G4_Ho  # scripted group (container) (typed FeaturePython)
  Dunit = g/cm3
  Dvalue = 8.795
  Group = -> [Ho_element001]
  conduct = 2
  density = 1
  expand = 3
  formula = Ho
  name = G4_Ho
  specific = 4
FEATURE [App::DocumentObjectGroupPython] Er_element001  label="Er_element : 1"  # scripted group (container) (typed FeaturePython)
  n = 1
  ref = Er_element
FEATURE [App::DocumentObjectGroupPython] G4_Er  # scripted group (container) (typed FeaturePython)
  Dunit = g/cm3
  Dvalue = 9.066
  Group = -> [Er_element001]
  conduct = 2
  density = 1
  expand = 3
  formula = Er
  name = G4_Er
  specific = 4
FEATURE [App::DocumentObjectGroupPython] Tm_element001  label="Tm_element : 1"  # scripted group (container) (typed FeaturePython)
  n = 1
  ref = Tm_element
FEATURE [App::DocumentObjectGroupPython] G4_Tm  # scripted group (container) (typed FeaturePython)
  Dunit = g/cm3
  Dvalue = 9.321
  Group = -> [Tm_element001]
  conduct = 2
  density = 1
  expand = 3
  formula = Tm
  name = G4_Tm
  specific = 4
FEATURE [App::DocumentObjectGroupPython] Yb_element001  label="Yb_element : 1"  # scripted group (container) (typed FeaturePython)
  n = 1
  ref = Yb_element
FEATURE [App::DocumentObjectGroupPython] G4_Yb  # scripted group (container) (typed FeaturePython)
  Dunit = g/cm3
  Dvalue = 6.73
  Group = -> [Yb_element001]
  conduct = 2
  density = 1
  expand = 3
  formula = Yb
  name = G4_Yb
  specific = 4
FEATURE [App::DocumentObjectGroupPython] Lu_element001  label="Lu_element : 1"  # scripted group (container) (typed FeaturePython)
  n = 1
  ref = Lu_element
FEATURE [App::DocumentObjectGroupPython] G4_Lu  # scripted group (container) (typed FeaturePython)
  Dunit = g/cm3
  Dvalue = 9.84
  Group = -> [Lu_element001]
  conduct = 2
  density = 1
  expand = 3
  formula = Lu
  name = G4_Lu
  specific = 4
FEATURE [App::DocumentObjectGroupPython] Hf_element001  label="Hf_element : 1"  # scripted group (container) (typed FeaturePython)
  n = 1
  ref = Hf_element
FEATURE [App::DocumentObjectGroupPython] G4_Hf  # scripted group (container) (typed FeaturePython)
  Dunit = g/cm3
  Dvalue = 13.31
  Group = -> [Hf_element001]
  conduct = 2
  density = 1
  expand = 3
  formula = Hf
  name = G4_Hf
  specific = 4
FEATURE [App::DocumentObjectGroupPython] Ta_element001  label="Ta_element : 1"  # scripted group (container) (typed FeaturePython)
  n = 1
  ref = Ta_element
FEATURE [App::DocumentObjectGroupPython] G4_Ta  # scripted group (container) (typed FeaturePython)
  Dunit = g/cm3
  Dvalue = 16.654
  Group = -> [Ta_element001]
  conduct = 2
  density = 1
  expand = 3
  formula = Ta
  name = G4_Ta
  specific = 4
FEATURE [App::DocumentObjectGroupPython] W_element004  label="W_element : 004"  # scripted group (container) (typed FeaturePython)
  n = 1
  ref = W_element
FEATURE [App::DocumentObjectGroupPython] G4_W  # scripted group (container) (typed FeaturePython)
  Dunit = g/cm3
  Dvalue = 19.3
  Group = -> [W_element004]
  conduct = 2
  density = 1
  expand = 3
  formula = W
  name = G4_W
  specific = 4
FEATURE [App::DocumentObjectGroupPython] Re_element001  label="Re_element : 1"  # scripted group (container) (typed FeaturePython)
  n = 1
  ref = Re_element
FEATURE [App::DocumentObjectGroupPython] G4_Re  # scripted group (container) (typed FeaturePython)
  Dunit = g/cm3
  Dvalue = 21.02
  Group = -> [Re_element001]
  conduct = 2
  density = 1
  expand = 3
  formula = Re
  name = G4_Re
  specific = 4
FEATURE [App::DocumentObjectGroupPython] Os_element001  label="Os_element : 1"  # scripted group (container) (typed FeaturePython)
  n = 1
  ref = Os_element
FEATURE [App::DocumentObjectGroupPython] G4_Os  # scripted group (container) (typed FeaturePython)
  Dunit = g/cm3
  Dvalue = 22.57
  Group = -> [Os_element001]
  conduct = 2
  density = 1
  expand = 3
  formula = Os
  name = G4_Os
  specific = 4
FEATURE [App::DocumentObjectGroupPython] Ir_element001  label="Ir_element : 1"  # scripted group (container) (typed FeaturePython)
  n = 1
  ref = Ir_element
FEATURE [App::DocumentObjectGroupPython] G4_Ir  # scripted group (container) (typed FeaturePython)
  Dunit = g/cm3
  Dvalue = 22.42
  Group = -> [Ir_element001]
  conduct = 2
  density = 1
  expand = 3
  formula = Ir
  name = G4_Ir
  specific = 4
FEATURE [App::DocumentObjectGroupPython] Pt_element001  label="Pt_element : 1"  # scripted group (container) (typed FeaturePython)
  n = 1
  ref = Pt_element
FEATURE [App::DocumentObjectGroupPython] G4_Pt  # scripted group (container) (typed FeaturePython)
  Dunit = g/cm3
  Dvalue = 21.45
  Group = -> [Pt_element001]
  conduct = 2
  density = 1
  expand = 3
  formula = Pt
  name = G4_Pt
  specific = 4
FEATURE [App::DocumentObjectGroupPython] Au_element001  label="Au_element : 1"  # scripted group (container) (typed FeaturePython)
  n = 1
  ref = Au_element
FEATURE [App::DocumentObjectGroupPython] G4_Au  # scripted group (container) (typed FeaturePython)
  Dunit = g/cm3
  Dvalue = 19.32
  Group = -> [Au_element001]
  conduct = 2
  density = 1
  expand = 3
  formula = Au
  name = G4_Au
  specific = 4
FEATURE [App::DocumentObjectGroupPython] Hg_element002  label="Hg_element : 002"  # scripted group (container) (typed FeaturePython)
  n = 1
  ref = Hg_element
FEATURE [App::DocumentObjectGroupPython] G4_Hg  # scripted group (container) (typed FeaturePython)
  Dunit = g/cm3
  Dvalue = 13.546
  Group = -> [Hg_element002]
  conduct = 2
  density = 1
  expand = 3
  formula = Hg
  name = G4_Hg
  specific = 4
FEATURE [App::DocumentObjectGroupPython] Tl_element002  label="Tl_element : 002"  # scripted group (container) (typed FeaturePython)
  n = 1
  ref = Tl_element
FEATURE [App::DocumentObjectGroupPython] G4_Tl  # scripted group (container) (typed FeaturePython)
  Dunit = g/cm3
  Dvalue = 11.72
  Group = -> [Tl_element002]
  conduct = 2
  density = 1
  expand = 3
  formula = Tl
  name = G4_Tl
  specific = 4
FEATURE [App::DocumentObjectGroupPython] Pb_element003  label="Pb_element : 1"  # scripted group (container) (typed FeaturePython)
  n = 1
  ref = Pb_element
FEATURE [App::DocumentObjectGroupPython] G4_Pb  # scripted group (container) (typed FeaturePython)
  Dunit = g/cm3
  Dvalue = 11.35
  Group = -> [Pb_element003]
  conduct = 2
  density = 1
  expand = 3
  formula = Pb
  name = G4_Pb
  specific = 4
FEATURE [App::DocumentObjectGroupPython] Bi_element002  label="Bi_element : 1"  # scripted group (container) (typed FeaturePython)
  n = 1
  ref = Bi_element
FEATURE [App::DocumentObjectGroupPython] G4_Bi  # scripted group (container) (typed FeaturePython)
  Dunit = g/cm3
  Dvalue = 9.747
  Group = -> [Bi_element002]
  conduct = 2
  density = 1
  expand = 3
  formula = Bi
  name = G4_Bi
  specific = 4
FEATURE [App::DocumentObjectGroupPython] Po_element001  label="Po_element : 1"  # scripted group (container) (typed FeaturePython)
  n = 1
  ref = Po_element
FEATURE [App::DocumentObjectGroupPython] G4_Po  # scripted group (container) (typed FeaturePython)
  Dunit = g/cm3
  Dvalue = 9.32
  Group = -> [Po_element001]
  conduct = 2
  density = 1
  expand = 3
  formula = Po
  name = G4_Po
  specific = 4
FEATURE [App::DocumentObjectGroupPython] At_element001  label="At_element : 1"  # scripted group (container) (typed FeaturePython)
  n = 1
  ref = At_element
FEATURE [App::DocumentObjectGroupPython] G4_At  # scripted group (container) (typed FeaturePython)
  Dunit = g/cm3
  Dvalue = 9.32
  Group = -> [At_element001]
  conduct = 2
  density = 1
  expand = 3
  formula = At
  name = G4_At
  specific = 4
FEATURE [App::DocumentObjectGroupPython] Rn_element001  label="Rn_element : 1"  # scripted group (container) (typed FeaturePython)
  n = 1
  ref = Rn_element
FEATURE [App::DocumentObjectGroupPython] G4_Rn  # scripted group (container) (typed FeaturePython)
  Dunit = g/cm3
  Dvalue = 0.00900662
  Group = -> [Rn_element001]
  conduct = 2
  density = 1
  expand = 3
  formula = Rn
  name = G4_Rn
  specific = 4
FEATURE [App::DocumentObjectGroupPython] Fr_element001  label="Fr_element : 1"  # scripted group (container) (typed FeaturePython)
  n = 1
  ref = Fr_element
FEATURE [App::DocumentObjectGroupPython] G4_Fr  # scripted group (container) (typed FeaturePython)
  Dunit = g/cm3
  Dvalue = 1
  Group = -> [Fr_element001]
  conduct = 2
  density = 1
  expand = 3
  formula = Fr
  name = G4_Fr
  specific = 4
FEATURE [App::DocumentObjectGroupPython] Ra_element001  label="Ra_element : 1"  # scripted group (container) (typed FeaturePython)
  n = 1
  ref = Ra_element
FEATURE [App::DocumentObjectGroupPython] G4_Ra  # scripted group (container) (typed FeaturePython)
  Dunit = g/cm3
  Dvalue = 5
  Group = -> [Ra_element001]
  conduct = 2
  density = 1
  expand = 3
  formula = Ra
  name = G4_Ra
  specific = 4
FEATURE [App::DocumentObjectGroupPython] Ac_element001  label="Ac_element : 1"  # scripted group (container) (typed FeaturePython)
  n = 1
  ref = Ac_element
FEATURE [App::DocumentObjectGroupPython] G4_Ac  # scripted group (container) (typed FeaturePython)
  Dunit = g/cm3
  Dvalue = 10.07
  Group = -> [Ac_element001]
  conduct = 2
  density = 1
  expand = 3
  formula = Ac
  name = G4_Ac
  specific = 4
FEATURE [App::DocumentObjectGroupPython] Th_element001  label="Th_element : 1"  # scripted group (container) (typed FeaturePython)
  n = 1
  ref = Th_element
FEATURE [App::DocumentObjectGroupPython] G4_Th  # scripted group (container) (typed FeaturePython)
  Dunit = g/cm3
  Dvalue = 11.72
  Group = -> [Th_element001]
  conduct = 2
  density = 1
  expand = 3
  formula = Th
  name = G4_Th
  specific = 4
FEATURE [App::DocumentObjectGroupPython] Pa_element001  label="Pa_element : 1"  # scripted group (container) (typed FeaturePython)
  n = 1
  ref = Pa_element
FEATURE [App::DocumentObjectGroupPython] G4_Pa  # scripted group (container) (typed FeaturePython)
  Dunit = g/cm3
  Dvalue = 15.37
  Group = -> [Pa_element001]
  conduct = 2
  density = 1
  expand = 3
  formula = Pa
  name = G4_Pa
  specific = 4
FEATURE [App::DocumentObjectGroupPython] U_element004  label="U_element : 004"  # scripted group (container) (typed FeaturePython)
  n = 1
  ref = U_element
FEATURE [App::DocumentObjectGroupPython] G4_U  # scripted group (container) (typed FeaturePython)
  Dunit = g/cm3
  Dvalue = 18.95
  Group = -> [U_element004]
  conduct = 2
  density = 1
  expand = 3
  formula = U
  name = G4_U
  specific = 4
FEATURE [App::DocumentObjectGroupPython] Np_element001  label="Np_element : 1"  # scripted group (container) (typed FeaturePython)
  n = 1
  ref = Np_element
FEATURE [App::DocumentObjectGroupPython] G4_Np  # scripted group (container) (typed FeaturePython)
  Dunit = g/cm3
  Dvalue = 20.25
  Group = -> [Np_element001]
  conduct = 2
  density = 1
  expand = 3
  formula = Np
  name = G4_Np
  specific = 4
FEATURE [App::DocumentObjectGroupPython] Pu_element002  label="Pu_element : 002"  # scripted group (container) (typed FeaturePython)
  n = 1
  ref = Pu_element
FEATURE [App::DocumentObjectGroupPython] G4_Pu  # scripted group (container) (typed FeaturePython)
  Dunit = g/cm3
  Dvalue = 19.84
  Group = -> [Pu_element002]
  conduct = 2
  density = 1
  expand = 3
  formula = Pu
  name = G4_Pu
  specific = 4
FEATURE [App::DocumentObjectGroupPython] Am_element001  label="Am_element : 1"  # scripted group (container) (typed FeaturePython)
  n = 1
  ref = Am_element
FEATURE [App::DocumentObjectGroupPython] G4_Am  # scripted group (container) (typed FeaturePython)
  Dunit = g/cm3
  Dvalue = 13.67
  Group = -> [Am_element001]
  conduct = 2
  density = 1
  expand = 3
  formula = Am
  name = G4_Am
  specific = 4
FEATURE [App::DocumentObjectGroupPython] Cm_element001  label="Cm_element : 1"  # scripted group (container) (typed FeaturePython)
  n = 1
  ref = Cm_element
FEATURE [App::DocumentObjectGroupPython] G4_Cm  # scripted group (container) (typed FeaturePython)
  Dunit = g/cm3
  Dvalue = 13.51
  Group = -> [Cm_element001]
  conduct = 2
  density = 1
  expand = 3
  formula = Cm
  name = G4_Cm
  specific = 4
FEATURE [App::DocumentObjectGroupPython] Bk_element001  label="Bk_element : 1"  # scripted group (container) (typed FeaturePython)
  n = 1
  ref = Bk_element
FEATURE [App::DocumentObjectGroupPython] G4_Bk  # scripted group (container) (typed FeaturePython)
  Dunit = g/cm3
  Dvalue = 14
  Group = -> [Bk_element001]
  conduct = 2
  density = 1
  expand = 3
  formula = Bk
  name = G4_Bk
  specific = 4
FEATURE [App::DocumentObjectGroupPython] Cf_element001  label="Cf_element : 1"  # scripted group (container) (typed FeaturePython)
  n = 1
  ref = Cf_element
FEATURE [App::DocumentObjectGroupPython] G4_Cf  # scripted group (container) (typed FeaturePython)
  Dunit = g/cm3
  Dvalue = 10
  Group = -> [Cf_element001]
  conduct = 2
  density = 1
  expand = 3
  formula = Cf
  name = G4_Cf
  specific = 4
FEATURE [App::DocumentObjectGroupPython] Element  # scripted group (container) (typed FeaturePython)
  Group = -> [G4_H,G4_He,G4_Li,G4_Be,G4_B,G4_C,G4_N,G4_O,G4_F,G4_Ne,G4_Na,G4_Mg,G4_Al,G4_Si,G4_P,G4_S,G4_Cl,G4_Ar,G4_K,G4_Ca,G4_Sc,G4_Ti,G4_V,G4_Cr,G4_Mn,G4_Fe,G4_Co,G4_Ni,G4_Cu,G4_Zn,G4_Ga,G4_Ge,G4_As,G4_Se,G4_Br,G4_Kr,G4_Rb,G4_Sr,G4_Y,G4_Zr,G4_Nb,G4_Mo,G4_Tc,G4_Ru,G4_Rh,G4_Pd,G4_Ag,G4_Cd,G4_In,G4_Sn,G4_Sb,G4_Te,G4_I,G4_Xe,G4_Cs,G4_Ba,G4_La,G4_Ce,G4_Pr,G4_Nd,G4_Pm,G4_Sm,G4_Eu,G4_Gd,G4_Tb,G4_Dy,G4_Ho,G4_Er,+30 more]
FEATURE [App::DocumentObjectGroupPython] H_element114  label="H_element : 063"  # scripted group (container) (typed FeaturePython)
  n = 2
  ref = H_element
FEATURE [App::DocumentObjectGroupPython] G4_lH2  # scripted group (container) (typed FeaturePython)
  Dunit = g/cm3
  Dvalue = 0.0708
  Group = -> [H_element114]
  conduct = 2
  density = 1
  expand = 3
  formula = G4_lH2
  name = G4_lH2
  specific = 4
FEATURE [App::DocumentObjectGroupPython] N_element049  label="N_element : 022"  # scripted group (container) (typed FeaturePython)
  n = 2
  ref = N_element
FEATURE [App::DocumentObjectGroupPython] G4_lN2  # scripted group (container) (typed FeaturePython)
  Dunit = g/cm3
  Dvalue = 0.807
  Group = -> [N_element049]
  conduct = 2
  density = 1
  expand = 3
  formula = G4_lN2
  name = G4_lN2
  specific = 4
FEATURE [App::DocumentObjectGroupPython] O_element106  label="O_element : 060"  # scripted group (container) (typed FeaturePython)
  n = 2
  ref = O_element
FEATURE [App::DocumentObjectGroupPython] G4_lO2  # scripted group (container) (typed FeaturePython)
  Dunit = g/cm3
  Dvalue = 1.141
  Group = -> [O_element106]
  conduct = 2
  density = 1
  expand = 3
  formula = G4_lO2
  name = G4_lO2
  specific = 4
FEATURE [App::DocumentObjectGroupPython] Ar_element003  label="Ar_element : 002"  # scripted group (container) (typed FeaturePython)
  n = 1
  ref = Ar_element
FEATURE [App::DocumentObjectGroupPython] G4_lAr  # scripted group (container) (typed FeaturePython)
  Dunit = g/cm3
  Dvalue = 1.396
  Group = -> [Ar_element003]
  conduct = 2
  density = 1
  expand = 3
  formula = G4_lAr
  name = G4_lAr
  specific = 4
FEATURE [App::DocumentObjectGroupPython] Br_element008  label="Br_element : 005"  # scripted group (container) (typed FeaturePython)
  n = 1
  ref = Br_element
FEATURE [App::DocumentObjectGroupPython] G4_lBr  # scripted group (container) (typed FeaturePython)
  Dunit = g/cm3
  Dvalue = 3.1028
  Group = -> [Br_element008]
  conduct = 2
  density = 1
  expand = 3
  formula = G4_lBr
  name = G4_lBr
  specific = 4
FEATURE [App::DocumentObjectGroupPython] Kr_element002  label="Kr_element : 002"  # scripted group (container) (typed FeaturePython)
  n = 1
  ref = Kr_element
FEATURE [App::DocumentObjectGroupPython] G4_lKr  # scripted group (container) (typed FeaturePython)
  Dunit = g/cm3
  Dvalue = 2.418
  Group = -> [Kr_element002]
  conduct = 2
  density = 1
  expand = 3
  formula = G4_lKr
  name = G4_lKr
  specific = 4
FEATURE [App::DocumentObjectGroupPython] Xe_element002  label="Xe_element : 002"  # scripted group (container) (typed FeaturePython)
  n = 1
  ref = Xe_element
FEATURE [App::DocumentObjectGroupPython] G4_lXe  # scripted group (container) (typed FeaturePython)
  Dunit = g/cm3
  Dvalue = 2.953
  Group = -> [Xe_element002]
  conduct = 2
  density = 1
  expand = 3
  formula = G4_lXe
  name = G4_lXe
  specific = 4
FEATURE [App::DocumentObjectGroupPython] O_element107  label="O_element : 061"  # scripted group (container) (typed FeaturePython)
  n = 4
  ref = O_element
FEATURE [App::DocumentObjectGroupPython] Pb_element004  label="Pb_element : 002"  # scripted group (container) (typed FeaturePython)
  n = 1
  ref = Pb_element
FEATURE [App::DocumentObjectGroupPython] W_element005  label="W_element : 005"  # scripted group (container) (typed FeaturePython)
  n = 1
  ref = W_element
FEATURE [App::DocumentObjectGroupPython] G4_PbWO4  # scripted group (container) (typed FeaturePython)
  Dunit = g/cm3
  Dvalue = 8.28
  Group = -> [O_element107,Pb_element004,W_element005]
  conduct = 2
  density = 1
  expand = 3
  formula = G4_PbWO4
  name = G4_PbWO4
  specific = 4
FEATURE [App::DocumentObjectGroupPython] H_element115  label="H_element : 064"  # scripted group (container) (typed FeaturePython)
  n = 1
  ref = H_element
FEATURE [App::DocumentObjectGroupPython] G4_Galactic  # scripted group (container) (typed FeaturePython)
  Dunit = g/cm3
  Dvalue = 0
  Group = -> [H_element115]
  conduct = 2
  density = 1
  expand = 3
  formula = G4_Galactic
  name = G4_Galactic
  specific = 4
FEATURE [App::DocumentObjectGroupPython] C_element125  label="C_element : 071"  # scripted group (container) (typed FeaturePython)
  n = 1
  ref = C_element
FEATURE [App::DocumentObjectGroupPython] G4_GRAPHITE_POROUS  # scripted group (container) (typed FeaturePython)
  Dunit = g/cm3
  Dvalue = 1.7
  Group = -> [C_element125]
  conduct = 2
  density = 1
  expand = 3
  formula = G4_GRAPHITE_POROUS
  name = G4_GRAPHITE_POROUS
  specific = 4
FEATURE [App::DocumentObjectGroupPython] H_element116  label="H_element : 0.150"  # scripted group (container) (typed FeaturePython)
  n = 0.080538
FEATURE [App::DocumentObjectGroupPython] C_element126  label="C_element : 0.600"  # scripted group (container) (typed FeaturePython)
  n = 0.599848
FEATURE [App::DocumentObjectGroupPython] O_element108  label="O_element : 0.320"  # scripted group (container) (typed FeaturePython)
  n = 0.319614
FEATURE [App::DocumentObjectGroupPython] G4_LUCITE  # scripted group (container) (typed FeaturePython)
  Dunit = g/cm3
  Dvalue = 1.19
  Group = -> [H_element116,C_element126,O_element108]
  conduct = 2
  density = 1
  expand = 3
  formula = G4_LUCITE
  name = G4_LUCITE
  specific = 4
FEATURE [App::DocumentObjectGroupPython] Cu_element002  label="Cu_element : 62"  # scripted group (container) (typed FeaturePython)
  n = 62
  ref = Cu_element
FEATURE [App::DocumentObjectGroupPython] Zn_element002  label="Zn_element : 35"  # scripted group (container) (typed FeaturePython)
  n = 35
  ref = Zn_element
FEATURE [App::DocumentObjectGroupPython] Pb_element005  label="Pb_element : 3"  # scripted group (container) (typed FeaturePython)
  n = 3
  ref = Pb_element
FEATURE [App::DocumentObjectGroupPython] G4_BRASS  # scripted group (container) (typed FeaturePython)
  Dunit = g/cm3
  Dvalue = 8.52
  Group = -> [Cu_element002,Zn_element002,Pb_element005]
  conduct = 2
  density = 1
  expand = 3
  formula = G4_BRASS
  name = G4_BRASS
  specific = 4
FEATURE [App::DocumentObjectGroupPython] Cu_element003  label="Cu_element : 89"  # scripted group (container) (typed FeaturePython)
  n = 89
  ref = Cu_element
FEATURE [App::DocumentObjectGroupPython] Zn_element003  label="Zn_element : 9"  # scripted group (container) (typed FeaturePython)
  n = 9
  ref = Zn_element
FEATURE [App::DocumentObjectGroupPython] Pb_element006  label="Pb_element : 2"  # scripted group (container) (typed FeaturePython)
  n = 2
  ref = Pb_element
FEATURE [App::DocumentObjectGroupPython] G4_BRONZE  # scripted group (container) (typed FeaturePython)
  Dunit = g/cm3
  Dvalue = 8.82
  Group = -> [Cu_element003,Zn_element003,Pb_element006]
  conduct = 2
  density = 1
  expand = 3
  formula = G4_BRONZE
  name = G4_BRONZE
  specific = 4
FEATURE [App::DocumentObjectGroupPython] Fe_element008  label="Fe_element : 74"  # scripted group (container) (typed FeaturePython)
  n = 74
  ref = Fe_element
FEATURE [App::DocumentObjectGroupPython] Cr_element002  label="Cr_element : 18"  # scripted group (container) (typed FeaturePython)
  n = 18
  ref = Cr_element
FEATURE [App::DocumentObjectGroupPython] Ni_element002  label="Ni_element : 8"  # scripted group (container) (typed FeaturePython)
  n = 8
  ref = Ni_element
FEATURE [App::DocumentObjectGroupPython] G4_STAINLESS_STEEL  label="G4_STAINLESS-STEEL"  # scripted group (container) (typed FeaturePython)
  Dunit = g/cm3
  Dvalue = 8
  Group = -> [Fe_element008,Cr_element002,Ni_element002]
  conduct = 2
  density = 1
  expand = 3
  formula = G4_STAINLESS-STEEL
  name = G4_STAINLESS-STEEL
  specific = 4
FEATURE [App::DocumentObjectGroupPython] H_element117  label="H_element : 065"  # scripted group (container) (typed FeaturePython)
  n = 18
  ref = H_element
FEATURE [App::DocumentObjectGroupPython] C_element127  label="C_element : 072"  # scripted group (container) (typed FeaturePython)
  n = 12
  ref = C_element
FEATURE [App::DocumentObjectGroupPython] O_element109  label="O_element : 062"  # scripted group (container) (typed FeaturePython)
  n = 7
  ref = O_element
FEATURE [App::DocumentObjectGroupPython] G4_CR39  # scripted group (container) (typed FeaturePython)
  Dunit = g/cm3
  Dvalue = 1.32
  Group = -> [H_element117,C_element127,O_element109]
  conduct = 2
  density = 1
  expand = 3
  formula = G4_CR39
  name = G4_CR39
  specific = 4
FEATURE [App::DocumentObjectGroupPython] H_element118  label="H_element : 38"  # scripted group (container) (typed FeaturePython)
  n = 38
  ref = H_element
FEATURE [App::DocumentObjectGroupPython] C_element128  label="C_element : 073"  # scripted group (container) (typed FeaturePython)
  n = 18
  ref = C_element
FEATURE [App::DocumentObjectGroupPython] O_element110  label="O_element : 063"  # scripted group (container) (typed FeaturePython)
  n = 1
  ref = O_element
FEATURE [App::DocumentObjectGroupPython] G4_OCTADECANOL  # scripted group (container) (typed FeaturePython)
  Dunit = g/cm3
  Dvalue = 0.812
  Group = -> [H_element118,C_element128,O_element110]
  conduct = 2
  density = 1
  expand = 3
  formula = G4_OCTADECANOL
  name = G4_OCTADECANOL
  specific = 4
FEATURE [App::DocumentObjectGroupPython] HEP  # scripted group (container) (typed FeaturePython)
  Group = -> [G4_lH2,G4_lN2,G4_lO2,G4_lAr,G4_lBr,G4_lKr,G4_lXe,G4_PbWO4,G4_Galactic,G4_GRAPHITE_POROUS,G4_LUCITE,G4_BRASS,G4_BRONZE,G4_STAINLESS_STEEL,G4_CR39,G4_OCTADECANOL]
FEATURE [App::DocumentObjectGroupPython] C_element129  label="C_element : 074"  # scripted group (container) (typed FeaturePython)
  n = 14
  ref = C_element
FEATURE [App::DocumentObjectGroupPython] H_element119  label="H_element : 066"  # scripted group (container) (typed FeaturePython)
  n = 10
  ref = H_element
FEATURE [App::DocumentObjectGroupPython] O_element111  label="O_element : 064"  # scripted group (container) (typed FeaturePython)
  n = 2
  ref = O_element
FEATURE [App::DocumentObjectGroupPython] N_element050  label="N_element : 023"  # scripted group (container) (typed FeaturePython)
  n = 2
  ref = N_element
FEATURE [App::DocumentObjectGroupPython] G4_KEVLAR  # scripted group (container) (typed FeaturePython)
  Dunit = g/cm3
  Dvalue = 1.44
  Group = -> [C_element129,H_element119,O_element111,N_element050]
  conduct = 2
  density = 1
  expand = 3
  formula = G4_KEVLAR
  name = G4_KEVLAR
  specific = 4
FEATURE [App::DocumentObjectGroupPython] C_element130  label="C_element : 075"  # scripted group (container) (typed FeaturePython)
  n = 10
  ref = C_element
FEATURE [App::DocumentObjectGroupPython] H_element120  label="H_element : 067"  # scripted group (container) (typed FeaturePython)
  n = 8
  ref = H_element
FEATURE [App::DocumentObjectGroupPython] O_element112  label="O_element : 065"  # scripted group (container) (typed FeaturePython)
  n = 4
  ref = O_element
FEATURE [App::DocumentObjectGroupPython] G4_DACRON  # scripted group (container) (typed FeaturePython)
  Dunit = g/cm3
  Dvalue = 1.4
  Group = -> [C_element130,H_element120,O_element112]
  conduct = 2
  density = 1
  expand = 3
  formula = G4_DACRON
  name = G4_DACRON
  specific = 4
FEATURE [App::DocumentObjectGroupPython] C_element131  label="C_element : 076"  # scripted group (container) (typed FeaturePython)
  n = 4
  ref = C_element
FEATURE [App::DocumentObjectGroupPython] H_element121  label="H_element : 068"  # scripted group (container) (typed FeaturePython)
  n = 5
  ref = H_element
FEATURE [App::DocumentObjectGroupPython] Cl_element030  label="Cl_element : 016"  # scripted group (container) (typed FeaturePython)
  n = 1
  ref = Cl_element
FEATURE [App::DocumentObjectGroupPython] G4_NEOPRENE  # scripted group (container) (typed FeaturePython)
  Dunit = g/cm3
  Dvalue = 1.23
  Group = -> [C_element131,H_element121,Cl_element030]
  conduct = 2
  density = 1
  expand = 3
  formula = G4_NEOPRENE
  name = G4_NEOPRENE
  specific = 4
FEATURE [App::DocumentObjectGroupPython] Space  # scripted group (container) (typed FeaturePython)
  Group = -> [G4_KEVLAR,G4_DACRON,G4_NEOPRENE]
FEATURE [App::DocumentObjectGroupPython] H_element122  label="H_element : 069"  # scripted group (container) (typed FeaturePython)
  n = 5
  ref = H_element
FEATURE [App::DocumentObjectGroupPython] C_element132  label="C_element : 077"  # scripted group (container) (typed FeaturePython)
  n = 4
  ref = C_element
FEATURE [App::DocumentObjectGroupPython] N_element051  label="N_element : 3"  # scripted group (container) (typed FeaturePython)
  n = 3
  ref = N_element
FEATURE [App::DocumentObjectGroupPython] O_element113  label="O_element : 066"  # scripted group (container) (typed FeaturePython)
  n = 1
  ref = O_element
FEATURE [App::DocumentObjectGroupPython] G4_CYTOSINE  # scripted group (container) (typed FeaturePython)
  Dunit = g/cm3
  Dvalue = 1.55
  Group = -> [H_element122,C_element132,N_element051,O_element113]
  conduct = 2
  density = 1
  expand = 3
  formula = G4_CYTOSINE
  name = G4_CYTOSINE
  specific = 4
FEATURE [App::DocumentObjectGroupPython] H_element123  label="H_element : 070"  # scripted group (container) (typed FeaturePython)
  n = 6
  ref = H_element
FEATURE [App::DocumentObjectGroupPython] C_element133  label="C_element : 078"  # scripted group (container) (typed FeaturePython)
  n = 5
  ref = C_element
FEATURE [App::DocumentObjectGroupPython] N_element052  label="N_element : 024"  # scripted group (container) (typed FeaturePython)
  n = 2
  ref = N_element
FEATURE [App::DocumentObjectGroupPython] O_element114  label="O_element : 067"  # scripted group (container) (typed FeaturePython)
  n = 2
  ref = O_element
FEATURE [App::DocumentObjectGroupPython] G4_THYMINE  # scripted group (container) (typed FeaturePython)
  Dunit = g/cm3
  Dvalue = 1.23
  Group = -> [H_element123,C_element133,N_element052,O_element114]
  conduct = 2
  density = 1
  expand = 3
  formula = G4_THYMINE
  name = G4_THYMINE
  specific = 4
FEATURE [App::DocumentObjectGroupPython] H_element124  label="H_element : 071"  # scripted group (container) (typed FeaturePython)
  n = 4
  ref = H_element
FEATURE [App::DocumentObjectGroupPython] C_element134  label="C_element : 079"  # scripted group (container) (typed FeaturePython)
  n = 4
  ref = C_element
FEATURE [App::DocumentObjectGroupPython] N_element053  label="N_element : 025"  # scripted group (container) (typed FeaturePython)
  n = 2
  ref = N_element
FEATURE [App::DocumentObjectGroupPython] O_element115  label="O_element : 068"  # scripted group (container) (typed FeaturePython)
  n = 2
  ref = O_element
FEATURE [App::DocumentObjectGroupPython] G4_URACIL  # scripted group (container) (typed FeaturePython)
  Dunit = g/cm3
  Dvalue = 1.32
  Group = -> [H_element124,C_element134,N_element053,O_element115]
  conduct = 2
  density = 1
  expand = 3
  formula = G4_URACIL
  name = G4_URACIL
  specific = 4
FEATURE [App::DocumentObjectGroupPython] H_element125  label="H_element : 072"  # scripted group (container) (typed FeaturePython)
  n = 4
  ref = H_element
FEATURE [App::DocumentObjectGroupPython] C_element135  label="C_element : 080"  # scripted group (container) (typed FeaturePython)
  n = 5
  ref = C_element
FEATURE [App::DocumentObjectGroupPython] N_element054  label="N_element : 026"  # scripted group (container) (typed FeaturePython)
  n = 5
  ref = N_element
FEATURE [App::DocumentObjectGroupPython] G4_DNA_ADENINE  # scripted group (container) (typed FeaturePython)
  Dunit = g/cm3
  Dvalue = 1
  Group = -> [H_element125,C_element135,N_element054]
  conduct = 2
  density = 1
  expand = 3
  formula = G4_DNA_ADENINE
  name = G4_DNA_ADENINE
  specific = 4
FEATURE [App::DocumentObjectGroupPython] H_element126  label="H_element : 073"  # scripted group (container) (typed FeaturePython)
  n = 4
  ref = H_element
FEATURE [App::DocumentObjectGroupPython] C_element136  label="C_element : 081"  # scripted group (container) (typed FeaturePython)
  n = 5
  ref = C_element
FEATURE [App::DocumentObjectGroupPython] N_element055  label="N_element : 027"  # scripted group (container) (typed FeaturePython)
  n = 5
  ref = N_element
FEATURE [App::DocumentObjectGroupPython] O_element116  label="O_element : 069"  # scripted group (container) (typed FeaturePython)
  n = 1
  ref = O_element
FEATURE [App::DocumentObjectGroupPython] G4_DNA_GUANINE  # scripted group (container) (typed FeaturePython)
  Dunit = g/cm3
  Dvalue = 1
  Group = -> [H_element126,C_element136,N_element055,O_element116]
  conduct = 2
  density = 1
  expand = 3
  formula = G4_DNA_GUANINE
  name = G4_DNA_GUANINE
  specific = 4
FEATURE [App::DocumentObjectGroupPython] H_element127  label="H_element : 074"  # scripted group (container) (typed FeaturePython)
  n = 4
  ref = H_element
FEATURE [App::DocumentObjectGroupPython] C_element137  label="C_element : 082"  # scripted group (container) (typed FeaturePython)
  n = 4
  ref = C_element
FEATURE [App::DocumentObjectGroupPython] N_element056  label="N_element : 028"  # scripted group (container) (typed FeaturePython)
  n = 3
  ref = N_element
FEATURE [App::DocumentObjectGroupPython] O_element117  label="O_element : 070"  # scripted group (container) (typed FeaturePython)
  n = 1
  ref = O_element
FEATURE [App::DocumentObjectGroupPython] G4_DNA_CYTOSINE  # scripted group (container) (typed FeaturePython)
  Dunit = g/cm3
  Dvalue = 1
  Group = -> [H_element127,C_element137,N_element056,O_element117]
  conduct = 2
  density = 1
  expand = 3
  formula = G4_DNA_CYTOSINE
  name = G4_DNA_CYTOSINE
  specific = 4
FEATURE [App::DocumentObjectGroupPython] H_element128  label="H_element : 075"  # scripted group (container) (typed FeaturePython)
  n = 5
  ref = H_element
FEATURE [App::DocumentObjectGroupPython] C_element138  label="C_element : 083"  # scripted group (container) (typed FeaturePython)
  n = 5
  ref = C_element
FEATURE [App::DocumentObjectGroupPython] N_element057  label="N_element : 029"  # scripted group (container) (typed FeaturePython)
  n = 2
  ref = N_element
FEATURE [App::DocumentObjectGroupPython] O_element118  label="O_element : 071"  # scripted group (container) (typed FeaturePython)
  n = 2
  ref = O_element
FEATURE [App::DocumentObjectGroupPython] G4_DNA_THYMINE  # scripted group (container) (typed FeaturePython)
  Dunit = g/cm3
  Dvalue = 1
  Group = -> [H_element128,C_element138,N_element057,O_element118]
  conduct = 2
  density = 1
  expand = 3
  formula = G4_DNA_THYMINE
  name = G4_DNA_THYMINE
  specific = 4
FEATURE [App::DocumentObjectGroupPython] H_element129  label="H_element : 076"  # scripted group (container) (typed FeaturePython)
  n = 3
  ref = H_element
FEATURE [App::DocumentObjectGroupPython] C_element139  label="C_element : 084"  # scripted group (container) (typed FeaturePython)
  n = 4
  ref = C_element
FEATURE [App::DocumentObjectGroupPython] N_element058  label="N_element : 030"  # scripted group (container) (typed FeaturePython)
  n = 2
  ref = N_element
FEATURE [App::DocumentObjectGroupPython] O_element119  label="O_element : 072"  # scripted group (container) (typed FeaturePython)
  n = 2
  ref = O_element
FEATURE [App::DocumentObjectGroupPython] G4_DNA_URACIL  # scripted group (container) (typed FeaturePython)
  Dunit = g/cm3
  Dvalue = 1
  Group = -> [H_element129,C_element139,N_element058,O_element119]
  conduct = 2
  density = 1
  expand = 3
  formula = G4_DNA_URACIL
  name = G4_DNA_URACIL
  specific = 4
FEATURE [App::DocumentObjectGroupPython] H_element130  label="H_element : 077"  # scripted group (container) (typed FeaturePython)
  n = 10
  ref = H_element
FEATURE [App::DocumentObjectGroupPython] C_element140  label="C_element : 085"  # scripted group (container) (typed FeaturePython)
  n = 10
  ref = C_element
FEATURE [App::DocumentObjectGroupPython] N_element059  label="N_element : 031"  # scripted group (container) (typed FeaturePython)
  n = 5
  ref = N_element
FEATURE [App::DocumentObjectGroupPython] O_element120  label="O_element : 073"  # scripted group (container) (typed FeaturePython)
  n = 4
  ref = O_element
FEATURE [App::DocumentObjectGroupPython] G4_DNA_ADENOSINE  # scripted group (container) (typed FeaturePython)
  Dunit = g/cm3
  Dvalue = 1
  Group = -> [H_element130,C_element140,N_element059,O_element120]
  conduct = 2
  density = 1
  expand = 3
  formula = G4_DNA_ADENOSINE
  name = G4_DNA_ADENOSINE
  specific = 4
FEATURE [App::DocumentObjectGroupPython] H_element131  label="H_element : 078"  # scripted group (container) (typed FeaturePython)
  n = 10
  ref = H_element
FEATURE [App::DocumentObjectGroupPython] C_element141  label="C_element : 086"  # scripted group (container) (typed FeaturePython)
  n = 10
  ref = C_element
FEATURE [App::DocumentObjectGroupPython] N_element060  label="N_element : 032"  # scripted group (container) (typed FeaturePython)
  n = 5
  ref = N_element
FEATURE [App::DocumentObjectGroupPython] O_element121  label="O_element : 074"  # scripted group (container) (typed FeaturePython)
  n = 5
  ref = O_element
FEATURE [App::DocumentObjectGroupPython] G4_DNA_GUANOSINE  # scripted group (container) (typed FeaturePython)
  Dunit = g/cm3
  Dvalue = 1
  Group = -> [H_element131,C_element141,N_element060,O_element121]
  conduct = 2
  density = 1
  expand = 3
  formula = G4_DNA_GUANOSINE
  name = G4_DNA_GUANOSINE
  specific = 4
FEATURE [App::DocumentObjectGroupPython] H_element132  label="H_element : 079"  # scripted group (container) (typed FeaturePython)
  n = 10
  ref = H_element
FEATURE [App::DocumentObjectGroupPython] C_element142  label="C_element : 087"  # scripted group (container) (typed FeaturePython)
  n = 9
  ref = C_element
FEATURE [App::DocumentObjectGroupPython] N_element061  label="N_element : 033"  # scripted group (container) (typed FeaturePython)
  n = 3
  ref = N_element
FEATURE [App::DocumentObjectGroupPython] O_element122  label="O_element : 075"  # scripted group (container) (typed FeaturePython)
  n = 5
  ref = O_element
FEATURE [App::DocumentObjectGroupPython] G4_DNA_CYTIDINE  # scripted group (container) (typed FeaturePython)
  Dunit = g/cm3
  Dvalue = 1
  Group = -> [H_element132,C_element142,N_element061,O_element122]
  conduct = 2
  density = 1
  expand = 3
  formula = G4_DNA_CYTIDINE
  name = G4_DNA_CYTIDINE
  specific = 4
FEATURE [App::DocumentObjectGroupPython] H_element133  label="H_element : 080"  # scripted group (container) (typed FeaturePython)
  n = 9
  ref = H_element
FEATURE [App::DocumentObjectGroupPython] C_element143  label="C_element : 088"  # scripted group (container) (typed FeaturePython)
  n = 9
  ref = C_element
FEATURE [App::DocumentObjectGroupPython] N_element062  label="N_element : 034"  # scripted group (container) (typed FeaturePython)
  n = 2
  ref = N_element
FEATURE [App::DocumentObjectGroupPython] O_element123  label="O_element : 076"  # scripted group (container) (typed FeaturePython)
  n = 6
  ref = O_element
FEATURE [App::DocumentObjectGroupPython] G4_DNA_URIDINE  # scripted group (container) (typed FeaturePython)
  Dunit = g/cm3
  Dvalue = 1
  Group = -> [H_element133,C_element143,N_element062,O_element123]
  conduct = 2
  density = 1
  expand = 3
  formula = G4_DNA_URIDINE
  name = G4_DNA_URIDINE
  specific = 4
FEATURE [App::DocumentObjectGroupPython] H_element134  label="H_element : 081"  # scripted group (container) (typed FeaturePython)
  n = 11
  ref = H_element
FEATURE [App::DocumentObjectGroupPython] C_element144  label="C_element : 089"  # scripted group (container) (typed FeaturePython)
  n = 10
  ref = C_element
FEATURE [App::DocumentObjectGroupPython] N_element063  label="N_element : 035"  # scripted group (container) (typed FeaturePython)
  n = 2
  ref = N_element
FEATURE [App::DocumentObjectGroupPython] O_element124  label="O_element : 077"  # scripted group (container) (typed FeaturePython)
  n = 6
  ref = O_element
FEATURE [App::DocumentObjectGroupPython] G4_DNA_METHYLURIDINE  # scripted group (container) (typed FeaturePython)
  Dunit = g/cm3
  Dvalue = 1
  Group = -> [H_element134,C_element144,N_element063,O_element124]
  conduct = 2
  density = 1
  expand = 3
  formula = G4_DNA_METHYLURIDINE
  name = G4_DNA_METHYLURIDINE
  specific = 4
FEATURE [App::DocumentObjectGroupPython] P_element014  label="P_element : 003"  # scripted group (container) (typed FeaturePython)
  n = 1
  ref = P_element
FEATURE [App::DocumentObjectGroupPython] O_element125  label="O_element : 078"  # scripted group (container) (typed FeaturePython)
  n = 3
  ref = O_element
FEATURE [App::DocumentObjectGroupPython] G4_DNA_MONOPHOSPHATE  # scripted group (container) (typed FeaturePython)
  Dunit = g/cm3
  Dvalue = 1
  Group = -> [P_element014,O_element125]
  conduct = 2
  density = 1
  expand = 3
  formula = G4_DNA_MONOPHOSPHATE
  name = G4_DNA_MONOPHOSPHATE
  specific = 4
FEATURE [App::DocumentObjectGroupPython] H_element135  label="H_element : 082"  # scripted group (container) (typed FeaturePython)
  n = 10
  ref = H_element
FEATURE [App::DocumentObjectGroupPython] C_element145  label="C_element : 090"  # scripted group (container) (typed FeaturePython)
  n = 10
  ref = C_element
FEATURE [App::DocumentObjectGroupPython] N_element064  label="N_element : 036"  # scripted group (container) (typed FeaturePython)
  n = 5
  ref = N_element
FEATURE [App::DocumentObjectGroupPython] O_element126  label="O_element : 079"  # scripted group (container) (typed FeaturePython)
  n = 7
  ref = O_element
FEATURE [App::DocumentObjectGroupPython] P_element015  label="P_element : 004"  # scripted group (container) (typed FeaturePython)
  n = 1
  ref = P_element
FEATURE [App::DocumentObjectGroupPython] G4_DNA_A  # scripted group (container) (typed FeaturePython)
  Dunit = g/cm3
  Dvalue = 1
  Group = -> [H_element135,C_element145,N_element064,O_element126,P_element015]
  conduct = 2
  density = 1
  expand = 3
  formula = G4_DNA_A
  name = G4_DNA_A
  specific = 4
FEATURE [App::DocumentObjectGroupPython] H_element136  label="H_element : 083"  # scripted group (container) (typed FeaturePython)
  n = 10
  ref = H_element
FEATURE [App::DocumentObjectGroupPython] C_element146  label="C_element : 091"  # scripted group (container) (typed FeaturePython)
  n = 10
  ref = C_element
FEATURE [App::DocumentObjectGroupPython] N_element065  label="N_element : 037"  # scripted group (container) (typed FeaturePython)
  n = 5
  ref = N_element
FEATURE [App::DocumentObjectGroupPython] O_element127  label="O_element : 8"  # scripted group (container) (typed FeaturePython)
  n = 8
  ref = O_element
FEATURE [App::DocumentObjectGroupPython] P_element016  label="P_element : 005"  # scripted group (container) (typed FeaturePython)
  n = 1
  ref = P_element
FEATURE [App::DocumentObjectGroupPython] G4_DNA_G  # scripted group (container) (typed FeaturePython)
  Dunit = g/cm3
  Dvalue = 1
  Group = -> [H_element136,C_element146,N_element065,O_element127,P_element016]
  conduct = 2
  density = 1
  expand = 3
  formula = G4_DNA_G
  name = G4_DNA_G
  specific = 4
FEATURE [App::DocumentObjectGroupPython] H_element137  label="H_element : 084"  # scripted group (container) (typed FeaturePython)
  n = 10
  ref = H_element
FEATURE [App::DocumentObjectGroupPython] C_element147  label="C_element : 092"  # scripted group (container) (typed FeaturePython)
  n = 9
  ref = C_element
FEATURE [App::DocumentObjectGroupPython] N_element066  label="N_element : 038"  # scripted group (container) (typed FeaturePython)
  n = 3
  ref = N_element
FEATURE [App::DocumentObjectGroupPython] O_element128  label="O_element : 080"  # scripted group (container) (typed FeaturePython)
  n = 8
  ref = O_element
FEATURE [App::DocumentObjectGroupPython] P_element017  label="P_element : 006"  # scripted group (container) (typed FeaturePython)
  n = 1
  ref = P_element
FEATURE [App::DocumentObjectGroupPython] G4_DNA_C  # scripted group (container) (typed FeaturePython)
  Dunit = g/cm3
  Dvalue = 1
  Group = -> [H_element137,C_element147,N_element066,O_element128,P_element017]
  conduct = 2
  density = 1
  expand = 3
  formula = G4_DNA_C
  name = G4_DNA_C
  specific = 4
FEATURE [App::DocumentObjectGroupPython] H_element138  label="H_element : 085"  # scripted group (container) (typed FeaturePython)
  n = 9
  ref = H_element
FEATURE [App::DocumentObjectGroupPython] C_element148  label="C_element : 093"  # scripted group (container) (typed FeaturePython)
  n = 9
  ref = C_element
FEATURE [App::DocumentObjectGroupPython] N_element067  label="N_element : 039"  # scripted group (container) (typed FeaturePython)
  n = 2
  ref = N_element
FEATURE [App::DocumentObjectGroupPython] O_element129  label="O_element : 9"  # scripted group (container) (typed FeaturePython)
  n = 9
  ref = O_element
FEATURE [App::DocumentObjectGroupPython] P_element018  label="P_element : 007"  # scripted group (container) (typed FeaturePython)
  n = 1
  ref = P_element
FEATURE [App::DocumentObjectGroupPython] G4_DNA_U  # scripted group (container) (typed FeaturePython)
  Dunit = g/cm3
  Dvalue = 1
  Group = -> [H_element138,C_element148,N_element067,O_element129,P_element018]
  conduct = 2
  density = 1
  expand = 3
  formula = G4_DNA_U
  name = G4_DNA_U
  specific = 4
FEATURE [App::DocumentObjectGroupPython] H_element139  label="H_element : 086"  # scripted group (container) (typed FeaturePython)
  n = 11
  ref = H_element
FEATURE [App::DocumentObjectGroupPython] C_element149  label="C_element : 094"  # scripted group (container) (typed FeaturePython)
  n = 10
  ref = C_element
FEATURE [App::DocumentObjectGroupPython] N_element068  label="N_element : 040"  # scripted group (container) (typed FeaturePython)
  n = 2
  ref = N_element
FEATURE [App::DocumentObjectGroupPython] O_element130  label="O_element : 081"  # scripted group (container) (typed FeaturePython)
  n = 9
  ref = O_element
FEATURE [App::DocumentObjectGroupPython] P_element019  label="P_element : 008"  # scripted group (container) (typed FeaturePython)
  n = 1
  ref = P_element
FEATURE [App::DocumentObjectGroupPython] G4_DNA_MU  # scripted group (container) (typed FeaturePython)
  Dunit = g/cm3
  Dvalue = 1
  Group = -> [H_element139,C_element149,N_element068,O_element130,P_element019]
  conduct = 2
  density = 1
  expand = 3
  formula = G4_DNA_MU
  name = G4_DNA_MU
  specific = 4
FEATURE [App::DocumentObjectGroupPython] BioChemical  # scripted group (container) (typed FeaturePython)
  Group = -> [G4_CYTOSINE,G4_THYMINE,G4_URACIL,G4_DNA_ADENINE,G4_DNA_GUANINE,G4_DNA_CYTOSINE,G4_DNA_THYMINE,G4_DNA_URACIL,G4_DNA_ADENOSINE,G4_DNA_GUANOSINE,G4_DNA_CYTIDINE,G4_DNA_URIDINE,G4_DNA_METHYLURIDINE,G4_DNA_MONOPHOSPHATE,G4_DNA_A,G4_DNA_G,G4_DNA_C,G4_DNA_U,G4_DNA_MU]
FEATURE [App::DocumentObjectGroupPython] G4Materials  # scripted group (container) (typed FeaturePython)
  Group = -> [NIST,Element,HEP,Space,BioChemical]
  version = 1
FEATURE [App::DocumentObjectGroupPython] Geant4  # scripted group (container) (typed FeaturePython)
  Group = -> [G4Isotopes,G4Elements,G4Materials]
FEATURE [App::DocumentObjectGroupPython] Materials  # scripted group (container) (typed FeaturePython)
  Group = -> [Geant4]
FEATURE [Part::FeaturePython] GDMLBox_WorldBox  # WARN: FeaturePython — macro-defined, semantics opaque (R4)
  lunit = 2
  material = 5
  x = 187.2
  y = 130
  z = 189.8
FEATURE [Part::FeaturePython] GDMLCone_Cone  # WARN: FeaturePython — macro-defined, semantics opaque (R4)
  Placement = pos=(20,0,0) rot=(0,0,1;0rad)
  aunit = 0
  deltaphi = 2
  lunit = 2
  material = 176
  rmax1 = 3
  rmax2 = 7
  rmin1 = 1
  rmin2 = 4
  startphi = 0
  z = 10
FEATURE [Part::FeaturePython] GDMLTorus_Torus  # WARN: FeaturePython — macro-defined, semantics opaque (R4)
  aunit = deg
  deltaphi = 360
  lunit = 2
  material = 0
  rmax = 8
  rmin = 0
  rtor = 28.9
  startphi = 0
FEATURE [Part::FeaturePython] GDMLTube_Tube  # WARN: FeaturePython — macro-defined, semantics opaque (R4)
  aunit = 1
  deltaphi = 360
  lunit = 2
  material = 0
  rmax = 28.9
  rmin = 0
  startphi = 0
  z = 16
FEATURE [Part::FeaturePython] GDMLTube_Tube001  label="GDMLTube_T_1"  # WARN: FeaturePython — macro-defined, semantics opaque (R4)
  Placement = pos=(0,0,-34) rot=(0,0,-1;0.349066rad)
  aunit = 1
  deltaphi = 360
  lunit = 2
  material = 0
  rmax = 36.9
  rmin = 0
  startphi = 0
  z = 68
FEATURE [Part::FeaturePython] GDMLTube_Tube002  # WARN: FeaturePython — macro-defined, semantics opaque (R4)
  aunit = 1
  deltaphi = 360
  lunit = 2
  material = 109
  rmax = 8
  rmin = 5
  startphi = 0
  z = 30
FEATURE [App::Part] LV_Tube  label="Tube"
  Group = -> [GDMLTube_Tube002,GDMLCone_Cone]
  Origin = -> Origin006
  Placement = pos=(57,0,0) rot=(0,1,0;1.5708rad)
FEATURE [Part::Fuse] Union
  Base = -> GDMLTorus_Torus
  Placement = pos=(0,0,0) rot=(0,0,1;0.523599rad)
  Tool = -> GDMLTube_Tube
FEATURE [Part::Fuse] Union001  label="U1"
  Base = -> Union
  Placement = pos=(0,0,34) rot=(0,0,1;0rad)
  Tool = -> GDMLTube_Tube001
  material = 211
FEATURE [App::Part] Bool_Union001  label="Detector"
  Group = -> [GDMLTorus_Torus,GDMLTube_Tube,Union,GDMLTube_Tube001,Union001]
  Origin = -> Origin005
FEATURE [App::Part] Part  label="DetectorAssembly"
  Group = -> [Bool_Union001,LV_Tube]
  Origin = -> Origin007
FEATURE [Part::Box] Box  label="Cube"
  AttacherType = Attacher::AttachEngine3D
  Height = 10
  Length = 50
  Placement = pos=(0,0,5) rot=(0,0,1;0rad)
  Width = 20
  material = 441
FEATURE [Part::Box] Box001  label="Cube001"
  AttacherType = Attacher::AttachEngine3D
  Height = 10
  Length = 50
  Placement = pos=(0,25,5) rot=(0,0,1;0rad)
  Width = 20
  material = 441
FEATURE [Part::Box] Box002  label="Cube002"
  AttacherType = Attacher::AttachEngine3D
  Height = 10
  Length = 50
  Placement = pos=(0,-25,5) rot=(0,0,1;0rad)
  Width = 20
  material = 261
FEATURE [App::Part] Part001  label="shieldAssembly"
  Group = -> [Box,Box001,Box002]
  Origin = -> Origin008
  Placement = pos=(0,0,58) rot=(0,0,1;0rad)
FEATURE [App::Part] worldVOL
  Group = -> [GDMLBox_WorldBox,Part,Part001]
  Origin = -> Origin
